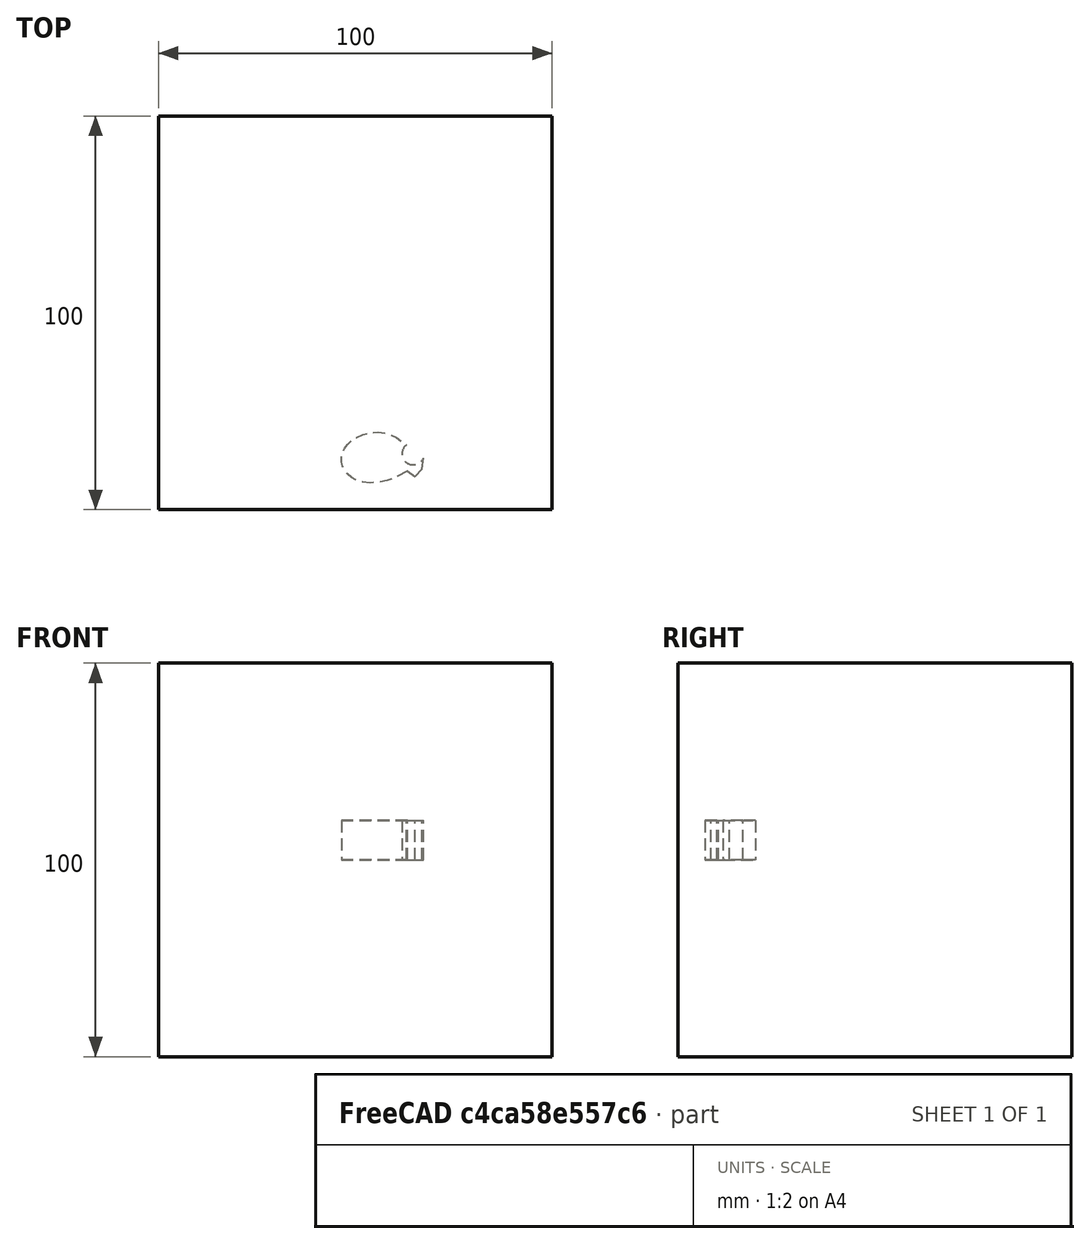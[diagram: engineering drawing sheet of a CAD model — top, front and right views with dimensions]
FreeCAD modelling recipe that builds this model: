
FCSTD DOCUMENT  (FreeCAD 0.19RUnknown)
Label: mirrorTest-3b
License: All rights reserved
LicenseURL: http://en.wikipedia.org/wiki/All_rights_reserved
objects: App::DocumentObjectGroupPython×1248, Part::Mirroring×2, App::Part×2, Part::FeaturePython×1, Sketcher::SketchObject×1, Part::Extrusion×1
note: 5 computed .brp shape members not serialized (recipe doc carries the construction recipe); baked Part::Feature solids carry a one-line shape summary decoded from their .brp

FEATURE [App::DocumentObjectGroupPython] HALFPI  # scripted group (container) (typed FeaturePython)
  name = HALFPI
  value = pi/2.
FEATURE [App::DocumentObjectGroupPython] PI  # scripted group (container) (typed FeaturePython)
  name = PI
  value = 1.*pi
FEATURE [App::DocumentObjectGroupPython] TWOPI  # scripted group (container) (typed FeaturePython)
  name = TWOPI
  value = 2.*pi
FEATURE [App::DocumentObjectGroupPython] Constants  # scripted group (container) (typed FeaturePython)
  Group = -> [HALFPI,PI,TWOPI]
FEATURE [App::DocumentObjectGroupPython] Variables  # scripted group (container) (typed FeaturePython)
FEATURE [App::DocumentObjectGroupPython] Quantities  # scripted group (container) (typed FeaturePython)
FEATURE [App::DocumentObjectGroupPython] Isotopes  # scripted group (container) (typed FeaturePython)
FEATURE [App::DocumentObjectGroupPython] Elements  # scripted group (container) (typed FeaturePython)
FEATURE [App::DocumentObjectGroupPython] G4Isotopes  # scripted group (container) (typed FeaturePython)
FEATURE [App::DocumentObjectGroupPython] H_element  # scripted group (container) (typed FeaturePython)
  Z = 1
  atom_value = 1.008
  formula = H
  name = H_element
FEATURE [App::DocumentObjectGroupPython] He_element  # scripted group (container) (typed FeaturePython)
  Z = 2
  atom_value = 4.0026
  formula = He
  name = He_element
FEATURE [App::DocumentObjectGroupPython] Li_element  # scripted group (container) (typed FeaturePython)
  Z = 3
  atom_value = 6.94
  formula = Li
  name = Li_element
FEATURE [App::DocumentObjectGroupPython] Be_element  # scripted group (container) (typed FeaturePython)
  Z = 4
  atom_value = 9.01218
  formula = Be
  name = Be_element
FEATURE [App::DocumentObjectGroupPython] B_element  # scripted group (container) (typed FeaturePython)
  Z = 5
  atom_value = 10.81
  formula = B
  name = B_element
FEATURE [App::DocumentObjectGroupPython] C_element  # scripted group (container) (typed FeaturePython)
  Z = 6
  atom_value = 12.011
  formula = C
  name = C_element
FEATURE [App::DocumentObjectGroupPython] N_element  # scripted group (container) (typed FeaturePython)
  Z = 7
  atom_value = 14.007
  formula = N
  name = N_element
FEATURE [App::DocumentObjectGroupPython] O_element  # scripted group (container) (typed FeaturePython)
  Z = 8
  atom_value = 15.999
  formula = O
  name = O_element
FEATURE [App::DocumentObjectGroupPython] F_element  # scripted group (container) (typed FeaturePython)
  Z = 9
  atom_value = 18.9984
  formula = F
  name = F_element
FEATURE [App::DocumentObjectGroupPython] Ne_element  # scripted group (container) (typed FeaturePython)
  Z = 10
  atom_value = 20.1797
  formula = Ne
  name = Ne_element
FEATURE [App::DocumentObjectGroupPython] Na_element  # scripted group (container) (typed FeaturePython)
  Z = 11
  atom_value = 22.9898
  formula = Na
  name = Na_element
FEATURE [App::DocumentObjectGroupPython] Mg_element  # scripted group (container) (typed FeaturePython)
  Z = 12
  atom_value = 24.305
  formula = Mg
  name = Mg_element
FEATURE [App::DocumentObjectGroupPython] Al_element  # scripted group (container) (typed FeaturePython)
  Z = 13
  atom_value = 26.9815
  formula = Al
  name = Al_element
FEATURE [App::DocumentObjectGroupPython] Si_element  # scripted group (container) (typed FeaturePython)
  Z = 14
  atom_value = 28.085
  formula = Si
  name = Si_element
FEATURE [App::DocumentObjectGroupPython] P_element  # scripted group (container) (typed FeaturePython)
  Z = 15
  atom_value = 30.9738
  formula = P
  name = P_element
FEATURE [App::DocumentObjectGroupPython] S_element  # scripted group (container) (typed FeaturePython)
  Z = 16
  atom_value = 32.06
  formula = S
  name = S_element
FEATURE [App::DocumentObjectGroupPython] Cl_element  # scripted group (container) (typed FeaturePython)
  Z = 17
  atom_value = 35.45
  formula = Cl
  name = Cl_element
FEATURE [App::DocumentObjectGroupPython] Ar_element  # scripted group (container) (typed FeaturePython)
  Z = 18
  atom_value = 39.95
  formula = Ar
  name = Ar_element
FEATURE [App::DocumentObjectGroupPython] K_element  # scripted group (container) (typed FeaturePython)
  Z = 19
  atom_value = 39.0983
  formula = K
  name = K_element
FEATURE [App::DocumentObjectGroupPython] Ca_element  # scripted group (container) (typed FeaturePython)
  Z = 20
  atom_value = 40.078
  formula = Ca
  name = Ca_element
FEATURE [App::DocumentObjectGroupPython] Sc_element  # scripted group (container) (typed FeaturePython)
  Z = 21
  atom_value = 44.9559
  formula = Sc
  name = Sc_element
FEATURE [App::DocumentObjectGroupPython] Ti_element  # scripted group (container) (typed FeaturePython)
  Z = 22
  atom_value = 47.867
  formula = Ti
  name = Ti_element
FEATURE [App::DocumentObjectGroupPython] V_element  # scripted group (container) (typed FeaturePython)
  Z = 23
  atom_value = 50.9415
  formula = V
  name = V_element
FEATURE [App::DocumentObjectGroupPython] Cr_element  # scripted group (container) (typed FeaturePython)
  Z = 24
  atom_value = 51.9961
  formula = Cr
  name = Cr_element
FEATURE [App::DocumentObjectGroupPython] Mn_element  # scripted group (container) (typed FeaturePython)
  Z = 25
  atom_value = 54.938
  formula = Mn
  name = Mn_element
FEATURE [App::DocumentObjectGroupPython] Fe_element  # scripted group (container) (typed FeaturePython)
  Z = 26
  atom_value = 55.845
  formula = Fe
  name = Fe_element
FEATURE [App::DocumentObjectGroupPython] Co_element  # scripted group (container) (typed FeaturePython)
  Z = 27
  atom_value = 58.9332
  formula = Co
  name = Co_element
FEATURE [App::DocumentObjectGroupPython] Ni_element  # scripted group (container) (typed FeaturePython)
  Z = 28
  atom_value = 58.6934
  formula = Ni
  name = Ni_element
FEATURE [App::DocumentObjectGroupPython] Cu_element  # scripted group (container) (typed FeaturePython)
  Z = 29
  atom_value = 63.546
  formula = Cu
  name = Cu_element
FEATURE [App::DocumentObjectGroupPython] Zn_element  # scripted group (container) (typed FeaturePython)
  Z = 30
  atom_value = 65.38
  formula = Zn
  name = Zn_element
FEATURE [App::DocumentObjectGroupPython] Ga_element  # scripted group (container) (typed FeaturePython)
  Z = 31
  atom_value = 69.723
  formula = Ga
  name = Ga_element
FEATURE [App::DocumentObjectGroupPython] Ge_element  # scripted group (container) (typed FeaturePython)
  Z = 32
  atom_value = 72.63
  formula = Ge
  name = Ge_element
FEATURE [App::DocumentObjectGroupPython] As_element  # scripted group (container) (typed FeaturePython)
  Z = 33
  atom_value = 74.9216
  formula = As
  name = As_element
FEATURE [App::DocumentObjectGroupPython] Se_element  # scripted group (container) (typed FeaturePython)
  Z = 34
  atom_value = 78.971
  formula = Se
  name = Se_element
FEATURE [App::DocumentObjectGroupPython] Br_element  # scripted group (container) (typed FeaturePython)
  Z = 35
  atom_value = 79.904
  formula = Br
  name = Br_element
FEATURE [App::DocumentObjectGroupPython] Kr_element  # scripted group (container) (typed FeaturePython)
  Z = 36
  atom_value = 83.798
  formula = Kr
  name = Kr_element
FEATURE [App::DocumentObjectGroupPython] Rb_element  # scripted group (container) (typed FeaturePython)
  Z = 37
  atom_value = 85.4678
  formula = Rb
  name = Rb_element
FEATURE [App::DocumentObjectGroupPython] Sr_element  # scripted group (container) (typed FeaturePython)
  Z = 38
  atom_value = 87.62
  formula = Sr
  name = Sr_element
FEATURE [App::DocumentObjectGroupPython] Y_element  # scripted group (container) (typed FeaturePython)
  Z = 39
  atom_value = 88.9058
  formula = Y
  name = Y_element
FEATURE [App::DocumentObjectGroupPython] Zr_element  # scripted group (container) (typed FeaturePython)
  Z = 40
  atom_value = 91.224
  formula = Zr
  name = Zr_element
FEATURE [App::DocumentObjectGroupPython] Nb_element  # scripted group (container) (typed FeaturePython)
  Z = 41
  atom_value = 92.9064
  formula = Nb
  name = Nb_element
FEATURE [App::DocumentObjectGroupPython] Mo_element  # scripted group (container) (typed FeaturePython)
  Z = 42
  atom_value = 95.95
  formula = Mo
  name = Mo_element
FEATURE [App::DocumentObjectGroupPython] Tc_element  # scripted group (container) (typed FeaturePython)
  Z = 43
  atom_value = 97
  formula = Tc
  name = Tc_element
FEATURE [App::DocumentObjectGroupPython] Ru_element  # scripted group (container) (typed FeaturePython)
  Z = 44
  atom_value = 101.07
  formula = Ru
  name = Ru_element
FEATURE [App::DocumentObjectGroupPython] Rh_element  # scripted group (container) (typed FeaturePython)
  Z = 45
  atom_value = 102.905
  formula = Rh
  name = Rh_element
FEATURE [App::DocumentObjectGroupPython] Pd_element  # scripted group (container) (typed FeaturePython)
  Z = 46
  atom_value = 106.42
  formula = Pd
  name = Pd_element
FEATURE [App::DocumentObjectGroupPython] Ag_element  # scripted group (container) (typed FeaturePython)
  Z = 47
  atom_value = 107.868
  formula = Ag
  name = Ag_element
FEATURE [App::DocumentObjectGroupPython] Cd_element  # scripted group (container) (typed FeaturePython)
  Z = 48
  atom_value = 112.414
  formula = Cd
  name = Cd_element
FEATURE [App::DocumentObjectGroupPython] In_element  # scripted group (container) (typed FeaturePython)
  Z = 49
  atom_value = 114.818
  formula = In
  name = In_element
FEATURE [App::DocumentObjectGroupPython] Sn_element  # scripted group (container) (typed FeaturePython)
  Z = 50
  atom_value = 118.71
  formula = Sn
  name = Sn_element
FEATURE [App::DocumentObjectGroupPython] Sb_element  # scripted group (container) (typed FeaturePython)
  Z = 51
  atom_value = 121.76
  formula = Sb
  name = Sb_element
FEATURE [App::DocumentObjectGroupPython] Te_element  # scripted group (container) (typed FeaturePython)
  Z = 52
  atom_value = 127.6
  formula = Te
  name = Te_element
FEATURE [App::DocumentObjectGroupPython] I_element  # scripted group (container) (typed FeaturePython)
  Z = 53
  atom_value = 126.904
  formula = I
  name = I_element
FEATURE [App::DocumentObjectGroupPython] Xe_element  # scripted group (container) (typed FeaturePython)
  Z = 54
  atom_value = 131.293
  formula = Xe
  name = Xe_element
FEATURE [App::DocumentObjectGroupPython] Cs_element  # scripted group (container) (typed FeaturePython)
  Z = 55
  atom_value = 132.905
  formula = Cs
  name = Cs_element
FEATURE [App::DocumentObjectGroupPython] Ba_element  # scripted group (container) (typed FeaturePython)
  Z = 56
  atom_value = 137.327
  formula = Ba
  name = Ba_element
FEATURE [App::DocumentObjectGroupPython] La_element  # scripted group (container) (typed FeaturePython)
  Z = 57
  atom_value = 138.905
  formula = La
  name = La_element
FEATURE [App::DocumentObjectGroupPython] Ce_element  # scripted group (container) (typed FeaturePython)
  Z = 58
  atom_value = 140.116
  formula = Ce
  name = Ce_element
FEATURE [App::DocumentObjectGroupPython] Pr_element  # scripted group (container) (typed FeaturePython)
  Z = 59
  atom_value = 140.908
  formula = Pr
  name = Pr_element
FEATURE [App::DocumentObjectGroupPython] Nd_element  # scripted group (container) (typed FeaturePython)
  Z = 60
  atom_value = 144.242
  formula = Nd
  name = Nd_element
FEATURE [App::DocumentObjectGroupPython] Pm_element  # scripted group (container) (typed FeaturePython)
  Z = 61
  atom_value = 145
  formula = Pm
  name = Pm_element
FEATURE [App::DocumentObjectGroupPython] Sm_element  # scripted group (container) (typed FeaturePython)
  Z = 62
  atom_value = 150.36
  formula = Sm
  name = Sm_element
FEATURE [App::DocumentObjectGroupPython] Eu_element  # scripted group (container) (typed FeaturePython)
  Z = 63
  atom_value = 151.964
  formula = Eu
  name = Eu_element
FEATURE [App::DocumentObjectGroupPython] Gd_element  # scripted group (container) (typed FeaturePython)
  Z = 64
  atom_value = 157.25
  formula = Gd
  name = Gd_element
FEATURE [App::DocumentObjectGroupPython] Tb_element  # scripted group (container) (typed FeaturePython)
  Z = 65
  atom_value = 158.925
  formula = Tb
  name = Tb_element
FEATURE [App::DocumentObjectGroupPython] Dy_element  # scripted group (container) (typed FeaturePython)
  Z = 66
  atom_value = 162.5
  formula = Dy
  name = Dy_element
FEATURE [App::DocumentObjectGroupPython] Ho_element  # scripted group (container) (typed FeaturePython)
  Z = 67
  atom_value = 164.93
  formula = Ho
  name = Ho_element
FEATURE [App::DocumentObjectGroupPython] Er_element  # scripted group (container) (typed FeaturePython)
  Z = 68
  atom_value = 167.259
  formula = Er
  name = Er_element
FEATURE [App::DocumentObjectGroupPython] Tm_element  # scripted group (container) (typed FeaturePython)
  Z = 69
  atom_value = 168.934
  formula = Tm
  name = Tm_element
FEATURE [App::DocumentObjectGroupPython] Yb_element  # scripted group (container) (typed FeaturePython)
  Z = 70
  atom_value = 173.045
  formula = Yb
  name = Yb_element
FEATURE [App::DocumentObjectGroupPython] Lu_element  # scripted group (container) (typed FeaturePython)
  Z = 71
  atom_value = 174.967
  formula = Lu
  name = Lu_element
FEATURE [App::DocumentObjectGroupPython] Hf_element  # scripted group (container) (typed FeaturePython)
  Z = 72
  atom_value = 178.49
  formula = Hf
  name = Hf_element
FEATURE [App::DocumentObjectGroupPython] Ta_element  # scripted group (container) (typed FeaturePython)
  Z = 73
  atom_value = 180.948
  formula = Ta
  name = Ta_element
FEATURE [App::DocumentObjectGroupPython] W_element  # scripted group (container) (typed FeaturePython)
  Z = 74
  atom_value = 183.84
  formula = W
  name = W_element
FEATURE [App::DocumentObjectGroupPython] Re_element  # scripted group (container) (typed FeaturePython)
  Z = 75
  atom_value = 186.207
  formula = Re
  name = Re_element
FEATURE [App::DocumentObjectGroupPython] Os_element  # scripted group (container) (typed FeaturePython)
  Z = 76
  atom_value = 190.23
  formula = Os
  name = Os_element
FEATURE [App::DocumentObjectGroupPython] Ir_element  # scripted group (container) (typed FeaturePython)
  Z = 77
  atom_value = 192.217
  formula = Ir
  name = Ir_element
FEATURE [App::DocumentObjectGroupPython] Pt_element  # scripted group (container) (typed FeaturePython)
  Z = 78
  atom_value = 195.084
  formula = Pt
  name = Pt_element
FEATURE [App::DocumentObjectGroupPython] Au_element  # scripted group (container) (typed FeaturePython)
  Z = 79
  atom_value = 196.967
  formula = Au
  name = Au_element
FEATURE [App::DocumentObjectGroupPython] Hg_element  # scripted group (container) (typed FeaturePython)
  Z = 80
  atom_value = 200.592
  formula = Hg
  name = Hg_element
FEATURE [App::DocumentObjectGroupPython] Tl_element  # scripted group (container) (typed FeaturePython)
  Z = 81
  atom_value = 204.38
  formula = Tl
  name = Tl_element
FEATURE [App::DocumentObjectGroupPython] Pb_element  # scripted group (container) (typed FeaturePython)
  Z = 82
  atom_value = 207.2
  formula = Pb
  name = Pb_element
FEATURE [App::DocumentObjectGroupPython] Bi_element  # scripted group (container) (typed FeaturePython)
  Z = 83
  atom_value = 208.98
  formula = Bi
  name = Bi_element
FEATURE [App::DocumentObjectGroupPython] Po_element  # scripted group (container) (typed FeaturePython)
  Z = 84
  atom_value = 209
  formula = Po
  name = Po_element
FEATURE [App::DocumentObjectGroupPython] At_element  # scripted group (container) (typed FeaturePython)
  Z = 85
  atom_value = 210
  formula = At
  name = At_element
FEATURE [App::DocumentObjectGroupPython] Rn_element  # scripted group (container) (typed FeaturePython)
  Z = 86
  atom_value = 222
  formula = Rn
  name = Rn_element
FEATURE [App::DocumentObjectGroupPython] Fr_element  # scripted group (container) (typed FeaturePython)
  Z = 87
  atom_value = 223
  formula = Fr
  name = Fr_element
FEATURE [App::DocumentObjectGroupPython] Ra_element  # scripted group (container) (typed FeaturePython)
  Z = 88
  atom_value = 226
  formula = Ra
  name = Ra_element
FEATURE [App::DocumentObjectGroupPython] Ac_element  # scripted group (container) (typed FeaturePython)
  Z = 89
  atom_value = 227
  formula = Ac
  name = Ac_element
FEATURE [App::DocumentObjectGroupPython] Th_element  # scripted group (container) (typed FeaturePython)
  Z = 90
  atom_value = 232.038
  formula = Th
  name = Th_element
FEATURE [App::DocumentObjectGroupPython] Pa_element  # scripted group (container) (typed FeaturePython)
  Z = 91
  atom_value = 231.036
  formula = Pa
  name = Pa_element
FEATURE [App::DocumentObjectGroupPython] U_element  # scripted group (container) (typed FeaturePython)
  Z = 92
  atom_value = 238.029
  formula = U
  name = U_element
FEATURE [App::DocumentObjectGroupPython] Np_element  # scripted group (container) (typed FeaturePython)
  Z = 93
  atom_value = 237
  formula = Np
  name = Np_element
FEATURE [App::DocumentObjectGroupPython] Pu_element  # scripted group (container) (typed FeaturePython)
  Z = 94
  atom_value = 244
  formula = Pu
  name = Pu_element
FEATURE [App::DocumentObjectGroupPython] Am_element  # scripted group (container) (typed FeaturePython)
  Z = 95
  atom_value = 243
  formula = Am
  name = Am_element
FEATURE [App::DocumentObjectGroupPython] Cm_element  # scripted group (container) (typed FeaturePython)
  Z = 96
  atom_value = 247
  formula = Cm
  name = Cm_element
FEATURE [App::DocumentObjectGroupPython] Bk_element  # scripted group (container) (typed FeaturePython)
  Z = 97
  atom_value = 247
  formula = Bk
  name = Bk_element
FEATURE [App::DocumentObjectGroupPython] Cf_element  # scripted group (container) (typed FeaturePython)
  Z = 98
  atom_value = 251
  formula = Cf
  name = Cf_element
FEATURE [App::DocumentObjectGroupPython] G4Elements  # scripted group (container) (typed FeaturePython)
  Group = -> [H_element,He_element,Li_element,Be_element,B_element,C_element,N_element,O_element,F_element,Ne_element,Na_element,Mg_element,Al_element,Si_element,P_element,S_element,Cl_element,Ar_element,K_element,Ca_element,Sc_element,Ti_element,V_element,Cr_element,Mn_element,Fe_element,Co_element,Ni_element,Cu_element,Zn_element,Ga_element,Ge_element,As_element,Se_element,Br_element,Kr_element,Rb_element,+61 more]
FEATURE [App::DocumentObjectGroupPython] H_element001  label="H_element : 0.101"  # scripted group (container) (typed FeaturePython)
  n = 0.101327
FEATURE [App::DocumentObjectGroupPython] C_element001  label="C_element : 0.775"  # scripted group (container) (typed FeaturePython)
  n = 0.7755
FEATURE [App::DocumentObjectGroupPython] N_element001  label="N_element : 0.035"  # scripted group (container) (typed FeaturePython)
  n = 0.035057
FEATURE [App::DocumentObjectGroupPython] O_element001  label="O_element : 0.052"  # scripted group (container) (typed FeaturePython)
  n = 0.0523159
FEATURE [App::DocumentObjectGroupPython] F_element001  label="F_element : 0.017"  # scripted group (container) (typed FeaturePython)
  n = 0.017422
FEATURE [App::DocumentObjectGroupPython] Ca_element001  label="Ca_element : 0.018"  # scripted group (container) (typed FeaturePython)
  n = 0.018378
FEATURE [App::DocumentObjectGroupPython] G4_A_150_TISSUE  label="G4_A-150_TISSUE"  # scripted group (container) (typed FeaturePython)
  Dunit = g/cm3
  Dvalue = 1.127
  Group = -> [H_element001,C_element001,N_element001,O_element001,F_element001,Ca_element001]
  conduct = 2
  density = 1
  expand = 3
  formula = G4_A-150_TISSUE
  name = G4_A-150_TISSUE
  specific = 4
FEATURE [App::DocumentObjectGroupPython] C_element002  label="C_element : 3"  # scripted group (container) (typed FeaturePython)
  n = 3
  ref = C_element
FEATURE [App::DocumentObjectGroupPython] H_element002  label="H_element : 6"  # scripted group (container) (typed FeaturePython)
  n = 6
  ref = H_element
FEATURE [App::DocumentObjectGroupPython] O_element002  label="O_element : 1"  # scripted group (container) (typed FeaturePython)
  n = 1
  ref = O_element
FEATURE [App::DocumentObjectGroupPython] G4_ACETONE  # scripted group (container) (typed FeaturePython)
  Dunit = g/cm3
  Dvalue = 0.7899
  Group = -> [C_element002,H_element002,O_element002]
  conduct = 2
  density = 1
  expand = 3
  formula = G4_ACETONE
  name = G4_ACETONE
  specific = 4
FEATURE [App::DocumentObjectGroupPython] C_element003  label="C_element : 2"  # scripted group (container) (typed FeaturePython)
  n = 2
  ref = C_element
FEATURE [App::DocumentObjectGroupPython] H_element003  label="H_element : 2"  # scripted group (container) (typed FeaturePython)
  n = 2
  ref = H_element
FEATURE [App::DocumentObjectGroupPython] G4_ACETYLENE  # scripted group (container) (typed FeaturePython)
  Dunit = g/cm3
  Dvalue = 0.0010967
  Group = -> [C_element003,H_element003]
  conduct = 2
  density = 1
  expand = 3
  formula = G4_ACETYLENE
  name = G4_ACETYLENE
  specific = 4
FEATURE [App::DocumentObjectGroupPython] C_element004  label="C_element : 5"  # scripted group (container) (typed FeaturePython)
  n = 5
  ref = C_element
FEATURE [App::DocumentObjectGroupPython] H_element004  label="H_element : 5"  # scripted group (container) (typed FeaturePython)
  n = 5
  ref = H_element
FEATURE [App::DocumentObjectGroupPython] N_element002  label="N_element : 5"  # scripted group (container) (typed FeaturePython)
  n = 5
  ref = N_element
FEATURE [App::DocumentObjectGroupPython] G4_ADENINE  # scripted group (container) (typed FeaturePython)
  Dunit = g/cm3
  Dvalue = 1.6
  Group = -> [C_element004,H_element004,N_element002]
  conduct = 2
  density = 1
  expand = 3
  formula = G4_ADENINE
  name = G4_ADENINE
  specific = 4
FEATURE [App::DocumentObjectGroupPython] H_element005  label="H_element : 0.114"  # scripted group (container) (typed FeaturePython)
  n = 0.114
FEATURE [App::DocumentObjectGroupPython] C_element005  label="C_element : 0.598"  # scripted group (container) (typed FeaturePython)
  n = 0.598
FEATURE [App::DocumentObjectGroupPython] N_element003  label="N_element : 0.007"  # scripted group (container) (typed FeaturePython)
  n = 0.007
FEATURE [App::DocumentObjectGroupPython] O_element003  label="O_element : 0.278"  # scripted group (container) (typed FeaturePython)
  n = 0.278
FEATURE [App::DocumentObjectGroupPython] Na_element001  label="Na_element : 0.001"  # scripted group (container) (typed FeaturePython)
  n = 0.001
FEATURE [App::DocumentObjectGroupPython] S_element001  label="S_element : 0.001"  # scripted group (container) (typed FeaturePython)
  n = 0.001
FEATURE [App::DocumentObjectGroupPython] Cl_element001  label="Cl_element : 0.001"  # scripted group (container) (typed FeaturePython)
  n = 0.001
FEATURE [App::DocumentObjectGroupPython] G4_ADIPOSE_TISSUE_ICRP  # scripted group (container) (typed FeaturePython)
  Dunit = g/cm3
  Dvalue = 0.95
  Group = -> [H_element005,C_element005,N_element003,O_element003,Na_element001,S_element001,Cl_element001]
  conduct = 2
  density = 1
  expand = 3
  formula = G4_ADIPOSE_TISSUE_ICRP
  name = G4_ADIPOSE_TISSUE_ICRP
  specific = 4
FEATURE [App::DocumentObjectGroupPython] C_element006  label="C_element : 0.000"  # scripted group (container) (typed FeaturePython)
  n = 0.000124
FEATURE [App::DocumentObjectGroupPython] N_element004  label="N_element : 0.755"  # scripted group (container) (typed FeaturePython)
  n = 0.755268
FEATURE [App::DocumentObjectGroupPython] O_element004  label="O_element : 0.232"  # scripted group (container) (typed FeaturePython)
  n = 0.231781
FEATURE [App::DocumentObjectGroupPython] Ar_element001  label="Ar_element : 0.013"  # scripted group (container) (typed FeaturePython)
  n = 0.012827
FEATURE [App::DocumentObjectGroupPython] G4_AIR  # scripted group (container) (typed FeaturePython)
  Dunit = g/cm3
  Dvalue = 0.00120479
  Group = -> [C_element006,N_element004,O_element004,Ar_element001]
  conduct = 2
  density = 1
  expand = 3
  formula = G4_AIR
  name = G4_AIR
  specific = 4
FEATURE [App::DocumentObjectGroupPython] C_element007  label="C_element : 006"  # scripted group (container) (typed FeaturePython)
  n = 3
  ref = C_element
FEATURE [App::DocumentObjectGroupPython] H_element006  label="H_element : 7"  # scripted group (container) (typed FeaturePython)
  n = 7
  ref = H_element
FEATURE [App::DocumentObjectGroupPython] N_element005  label="N_element : 1"  # scripted group (container) (typed FeaturePython)
  n = 1
  ref = N_element
FEATURE [App::DocumentObjectGroupPython] O_element005  label="O_element : 2"  # scripted group (container) (typed FeaturePython)
  n = 2
  ref = O_element
FEATURE [App::DocumentObjectGroupPython] G4_ALANINE  # scripted group (container) (typed FeaturePython)
  Dunit = g/cm3
  Dvalue = 1.42
  Group = -> [C_element007,H_element006,N_element005,O_element005]
  conduct = 2
  density = 1
  expand = 3
  formula = G4_ALANINE
  name = G4_ALANINE
  specific = 4
FEATURE [App::DocumentObjectGroupPython] Al_element001  label="Al_element : 2"  # scripted group (container) (typed FeaturePython)
  n = 2
  ref = Al_element
FEATURE [App::DocumentObjectGroupPython] O_element006  label="O_element : 3"  # scripted group (container) (typed FeaturePython)
  n = 3
  ref = O_element
FEATURE [App::DocumentObjectGroupPython] G4_ALUMINUM_OXIDE  # scripted group (container) (typed FeaturePython)
  Dunit = g/cm3
  Dvalue = 3.97
  Group = -> [Al_element001,O_element006]
  conduct = 2
  density = 1
  expand = 3
  formula = G4_ALUMINUM_OXIDE
  name = G4_ALUMINUM_OXIDE
  specific = 4
FEATURE [App::DocumentObjectGroupPython] H_element007  label="H_element : 0.106"  # scripted group (container) (typed FeaturePython)
  n = 0.10593
FEATURE [App::DocumentObjectGroupPython] C_element008  label="C_element : 0.789"  # scripted group (container) (typed FeaturePython)
  n = 0.788974
FEATURE [App::DocumentObjectGroupPython] O_element007  label="O_element : 0.105"  # scripted group (container) (typed FeaturePython)
  n = 0.105096
FEATURE [App::DocumentObjectGroupPython] G4_AMBER  # scripted group (container) (typed FeaturePython)
  Dunit = g/cm3
  Dvalue = 1.1
  Group = -> [H_element007,C_element008,O_element007]
  conduct = 2
  density = 1
  expand = 3
  formula = G4_AMBER
  name = G4_AMBER
  specific = 4
FEATURE [App::DocumentObjectGroupPython] N_element006  label="N_element : 006"  # scripted group (container) (typed FeaturePython)
  n = 1
  ref = N_element
FEATURE [App::DocumentObjectGroupPython] H_element008  label="H_element : 3"  # scripted group (container) (typed FeaturePython)
  n = 3
  ref = H_element
FEATURE [App::DocumentObjectGroupPython] G4_AMMONIA  # scripted group (container) (typed FeaturePython)
  Dunit = g/cm3
  Dvalue = 0.000826019
  Group = -> [N_element006,H_element008]
  conduct = 2
  density = 1
  expand = 3
  formula = G4_AMMONIA
  name = G4_AMMONIA
  specific = 4
FEATURE [App::DocumentObjectGroupPython] C_element009  label="C_element : 6"  # scripted group (container) (typed FeaturePython)
  n = 6
  ref = C_element
FEATURE [App::DocumentObjectGroupPython] H_element009  label="H_element : 008"  # scripted group (container) (typed FeaturePython)
  n = 7
  ref = H_element
FEATURE [App::DocumentObjectGroupPython] N_element007  label="N_element : 007"  # scripted group (container) (typed FeaturePython)
  n = 1
  ref = N_element
FEATURE [App::DocumentObjectGroupPython] G4_ANILINE  # scripted group (container) (typed FeaturePython)
  Dunit = g/cm3
  Dvalue = 1.0235
  Group = -> [C_element009,H_element009,N_element007]
  conduct = 2
  density = 1
  expand = 3
  formula = G4_ANILINE
  name = G4_ANILINE
  specific = 4
FEATURE [App::DocumentObjectGroupPython] C_element010  label="C_element : 14"  # scripted group (container) (typed FeaturePython)
  n = 14
  ref = C_element
FEATURE [App::DocumentObjectGroupPython] H_element010  label="H_element : 10"  # scripted group (container) (typed FeaturePython)
  n = 10
  ref = H_element
FEATURE [App::DocumentObjectGroupPython] G4_ANTHRACENE  # scripted group (container) (typed FeaturePython)
  Dunit = g/cm3
  Dvalue = 1.283
  Group = -> [C_element010,H_element010]
  conduct = 2
  density = 1
  expand = 3
  formula = G4_ANTHRACENE
  name = G4_ANTHRACENE
  specific = 4
FEATURE [App::DocumentObjectGroupPython] H_element011  label="H_element : 0.065"  # scripted group (container) (typed FeaturePython)
  n = 0.0654709
FEATURE [App::DocumentObjectGroupPython] C_element011  label="C_element : 0.537"  # scripted group (container) (typed FeaturePython)
  n = 0.536944
FEATURE [App::DocumentObjectGroupPython] N_element008  label="N_element : 0.021"  # scripted group (container) (typed FeaturePython)
  n = 0.0215
FEATURE [App::DocumentObjectGroupPython] O_element008  label="O_element : 0.032"  # scripted group (container) (typed FeaturePython)
  n = 0.032085
FEATURE [App::DocumentObjectGroupPython] F_element002  label="F_element : 0.167"  # scripted group (container) (typed FeaturePython)
  n = 0.167411
FEATURE [App::DocumentObjectGroupPython] Ca_element002  label="Ca_element : 0.177"  # scripted group (container) (typed FeaturePython)
  n = 0.176589
FEATURE [App::DocumentObjectGroupPython] G4_B_100_BONE  label="G4_B-100_BONE"  # scripted group (container) (typed FeaturePython)
  Dunit = g/cm3
  Dvalue = 1.45
  Group = -> [H_element011,C_element011,N_element008,O_element008,F_element002,Ca_element002]
  conduct = 2
  density = 1
  expand = 3
  formula = G4_B-100_BONE
  name = G4_B-100_BONE
  specific = 4
FEATURE [App::DocumentObjectGroupPython] H_element012  label="H_element : 0.057"  # scripted group (container) (typed FeaturePython)
  n = 0.057441
FEATURE [App::DocumentObjectGroupPython] C_element012  label="C_element : 0.790"  # scripted group (container) (typed FeaturePython)
  n = 0.774591
FEATURE [App::DocumentObjectGroupPython] O_element009  label="O_element : 0.168"  # scripted group (container) (typed FeaturePython)
  n = 0.167968
FEATURE [App::DocumentObjectGroupPython] G4_BAKELITE  # scripted group (container) (typed FeaturePython)
  Dunit = g/cm3
  Dvalue = 1.25
  Group = -> [H_element012,C_element012,O_element009]
  conduct = 2
  density = 1
  expand = 3
  formula = G4_BAKELITE
  name = G4_BAKELITE
  specific = 4
FEATURE [App::DocumentObjectGroupPython] Ba_element001  label="Ba_element : 1"  # scripted group (container) (typed FeaturePython)
  n = 1
  ref = Ba_element
FEATURE [App::DocumentObjectGroupPython] F_element003  label="F_element : 2"  # scripted group (container) (typed FeaturePython)
  n = 2
  ref = F_element
FEATURE [App::DocumentObjectGroupPython] G4_BARIUM_FLUORIDE  # scripted group (container) (typed FeaturePython)
  Dunit = g/cm3
  Dvalue = 4.89
  Group = -> [Ba_element001,F_element003]
  conduct = 2
  density = 1
  expand = 3
  formula = G4_BARIUM_FLUORIDE
  name = G4_BARIUM_FLUORIDE
  specific = 4
FEATURE [App::DocumentObjectGroupPython] Ba_element002  label="Ba_element : 002"  # scripted group (container) (typed FeaturePython)
  n = 1
  ref = Ba_element
FEATURE [App::DocumentObjectGroupPython] S_element002  label="S_element : 1"  # scripted group (container) (typed FeaturePython)
  n = 1
  ref = S_element
FEATURE [App::DocumentObjectGroupPython] O_element010  label="O_element : 4"  # scripted group (container) (typed FeaturePython)
  n = 4
  ref = O_element
FEATURE [App::DocumentObjectGroupPython] G4_BARIUM_SULFATE  # scripted group (container) (typed FeaturePython)
  Dunit = g/cm3
  Dvalue = 4.5
  Group = -> [Ba_element002,S_element002,O_element010]
  conduct = 2
  density = 1
  expand = 3
  formula = G4_BARIUM_SULFATE
  name = G4_BARIUM_SULFATE
  specific = 4
FEATURE [App::DocumentObjectGroupPython] C_element013  label="C_element : 007"  # scripted group (container) (typed FeaturePython)
  n = 6
  ref = C_element
FEATURE [App::DocumentObjectGroupPython] H_element013  label="H_element : 009"  # scripted group (container) (typed FeaturePython)
  n = 6
  ref = H_element
FEATURE [App::DocumentObjectGroupPython] G4_BENZENE  # scripted group (container) (typed FeaturePython)
  Dunit = g/cm3
  Dvalue = 0.87865
  Group = -> [C_element013,H_element013]
  conduct = 2
  density = 1
  expand = 3
  formula = G4_BENZENE
  name = G4_BENZENE
  specific = 4
FEATURE [App::DocumentObjectGroupPython] Be_element001  label="Be_element : 1"  # scripted group (container) (typed FeaturePython)
  n = 1
  ref = Be_element
FEATURE [App::DocumentObjectGroupPython] O_element011  label="O_element : 005"  # scripted group (container) (typed FeaturePython)
  n = 1
  ref = O_element
FEATURE [App::DocumentObjectGroupPython] G4_BERYLLIUM_OXIDE  # scripted group (container) (typed FeaturePython)
  Dunit = g/cm3
  Dvalue = 3.01
  Group = -> [Be_element001,O_element011]
  conduct = 2
  density = 1
  expand = 3
  formula = G4_BERYLLIUM_OXIDE
  name = G4_BERYLLIUM_OXIDE
  specific = 4
FEATURE [App::DocumentObjectGroupPython] Bi_element001  label="Bi_element : 4"  # scripted group (container) (typed FeaturePython)
  n = 4
  ref = Bi_element
FEATURE [App::DocumentObjectGroupPython] Ge_element001  label="Ge_element : 3"  # scripted group (container) (typed FeaturePython)
  n = 3
  ref = Ge_element
FEATURE [App::DocumentObjectGroupPython] O_element012  label="O_element : 12"  # scripted group (container) (typed FeaturePython)
  n = 12
  ref = O_element
FEATURE [App::DocumentObjectGroupPython] G4_BGO  # scripted group (container) (typed FeaturePython)
  Dunit = g/cm3
  Dvalue = 7.13
  Group = -> [Bi_element001,Ge_element001,O_element012]
  conduct = 2
  density = 1
  expand = 3
  formula = G4_BGO
  name = G4_BGO
  specific = 4
FEATURE [App::DocumentObjectGroupPython] H_element014  label="H_element : 0.102"  # scripted group (container) (typed FeaturePython)
  n = 0.102
FEATURE [App::DocumentObjectGroupPython] C_element014  label="C_element : 0.110"  # scripted group (container) (typed FeaturePython)
  n = 0.11
FEATURE [App::DocumentObjectGroupPython] N_element009  label="N_element : 0.033"  # scripted group (container) (typed FeaturePython)
  n = 0.033
FEATURE [App::DocumentObjectGroupPython] O_element013  label="O_element : 0.745"  # scripted group (container) (typed FeaturePython)
  n = 0.745
FEATURE [App::DocumentObjectGroupPython] Na_element002  label="Na_element : 0.002"  # scripted group (container) (typed FeaturePython)
  n = 0.001
FEATURE [App::DocumentObjectGroupPython] P_element001  label="P_element : 0.001"  # scripted group (container) (typed FeaturePython)
  n = 0.001
FEATURE [App::DocumentObjectGroupPython] S_element003  label="S_element : 0.002"  # scripted group (container) (typed FeaturePython)
  n = 0.002
FEATURE [App::DocumentObjectGroupPython] Cl_element002  label="Cl_element : 0.003"  # scripted group (container) (typed FeaturePython)
  n = 0.003
FEATURE [App::DocumentObjectGroupPython] K_element001  label="K_element : 0.002"  # scripted group (container) (typed FeaturePython)
  n = 0.002
FEATURE [App::DocumentObjectGroupPython] Fe_element001  label="Fe_element : 0.001"  # scripted group (container) (typed FeaturePython)
  n = 0.001
FEATURE [App::DocumentObjectGroupPython] G4_BLOOD_ICRP  # scripted group (container) (typed FeaturePython)
  Dunit = g/cm3
  Dvalue = 1.06
  Group = -> [H_element014,C_element014,N_element009,O_element013,Na_element002,P_element001,S_element003,Cl_element002,K_element001,Fe_element001]
  conduct = 2
  density = 1
  expand = 3
  formula = G4_BLOOD_ICRP
  name = G4_BLOOD_ICRP
  specific = 4
FEATURE [App::DocumentObjectGroupPython] H_element015  label="H_element : 0.064"  # scripted group (container) (typed FeaturePython)
  n = 0.064
FEATURE [App::DocumentObjectGroupPython] C_element015  label="C_element : 0.278"  # scripted group (container) (typed FeaturePython)
  n = 0.278
FEATURE [App::DocumentObjectGroupPython] N_element010  label="N_element : 0.027"  # scripted group (container) (typed FeaturePython)
  n = 0.027
FEATURE [App::DocumentObjectGroupPython] O_element014  label="O_element : 0.410"  # scripted group (container) (typed FeaturePython)
  n = 0.41
FEATURE [App::DocumentObjectGroupPython] Mg_element001  label="Mg_element : 0.002"  # scripted group (container) (typed FeaturePython)
  n = 0.002
FEATURE [App::DocumentObjectGroupPython] P_element002  label="P_element : 0.070"  # scripted group (container) (typed FeaturePython)
  n = 0.07
FEATURE [App::DocumentObjectGroupPython] S_element004  label="S_element : 0.003"  # scripted group (container) (typed FeaturePython)
  n = 0.002
FEATURE [App::DocumentObjectGroupPython] Ca_element003  label="Ca_element : 0.147"  # scripted group (container) (typed FeaturePython)
  n = 0.147
FEATURE [App::DocumentObjectGroupPython] G4_BONE_COMPACT_ICRU  # scripted group (container) (typed FeaturePython)
  Dunit = g/cm3
  Dvalue = 1.85
  Group = -> [H_element015,C_element015,N_element010,O_element014,Mg_element001,P_element002,S_element004,Ca_element003]
  conduct = 2
  density = 1
  expand = 3
  formula = G4_BONE_COMPACT_ICRU
  name = G4_BONE_COMPACT_ICRU
  specific = 4
FEATURE [App::DocumentObjectGroupPython] H_element016  label="H_element : 0.034"  # scripted group (container) (typed FeaturePython)
  n = 0.034
FEATURE [App::DocumentObjectGroupPython] C_element016  label="C_element : 0.155"  # scripted group (container) (typed FeaturePython)
  n = 0.155
FEATURE [App::DocumentObjectGroupPython] N_element011  label="N_element : 0.042"  # scripted group (container) (typed FeaturePython)
  n = 0.042
FEATURE [App::DocumentObjectGroupPython] O_element015  label="O_element : 0.435"  # scripted group (container) (typed FeaturePython)
  n = 0.435
FEATURE [App::DocumentObjectGroupPython] Na_element003  label="Na_element : 0.003"  # scripted group (container) (typed FeaturePython)
  n = 0.001
FEATURE [App::DocumentObjectGroupPython] Mg_element002  label="Mg_element : 0.003"  # scripted group (container) (typed FeaturePython)
  n = 0.002
FEATURE [App::DocumentObjectGroupPython] P_element003  label="P_element : 0.103"  # scripted group (container) (typed FeaturePython)
  n = 0.103
FEATURE [App::DocumentObjectGroupPython] S_element005  label="S_element : 0.004"  # scripted group (container) (typed FeaturePython)
  n = 0.003
FEATURE [App::DocumentObjectGroupPython] Ca_element004  label="Ca_element : 0.225"  # scripted group (container) (typed FeaturePython)
  n = 0.225
FEATURE [App::DocumentObjectGroupPython] G4_BONE_CORTICAL_ICRP  # scripted group (container) (typed FeaturePython)
  Dunit = g/cm3
  Dvalue = 1.92
  Group = -> [H_element016,C_element016,N_element011,O_element015,Na_element003,Mg_element002,P_element003,S_element005,Ca_element004]
  conduct = 2
  density = 1
  expand = 3
  formula = G4_BONE_CORTICAL_ICRP
  name = G4_BONE_CORTICAL_ICRP
  specific = 4
FEATURE [App::DocumentObjectGroupPython] B_element001  label="B_element : 4"  # scripted group (container) (typed FeaturePython)
  n = 4
  ref = B_element
FEATURE [App::DocumentObjectGroupPython] C_element017  label="C_element : 1"  # scripted group (container) (typed FeaturePython)
  n = 1
  ref = C_element
FEATURE [App::DocumentObjectGroupPython] G4_BORON_CARBIDE  # scripted group (container) (typed FeaturePython)
  Dunit = g/cm3
  Dvalue = 2.52
  Group = -> [B_element001,C_element017]
  conduct = 2
  density = 1
  expand = 3
  formula = G4_BORON_CARBIDE
  name = G4_BORON_CARBIDE
  specific = 4
FEATURE [App::DocumentObjectGroupPython] B_element002  label="B_element : 2"  # scripted group (container) (typed FeaturePython)
  n = 2
  ref = B_element
FEATURE [App::DocumentObjectGroupPython] O_element016  label="O_element : 006"  # scripted group (container) (typed FeaturePython)
  n = 3
  ref = O_element
FEATURE [App::DocumentObjectGroupPython] G4_BORON_OXIDE  # scripted group (container) (typed FeaturePython)
  Dunit = g/cm3
  Dvalue = 1.812
  Group = -> [B_element002,O_element016]
  conduct = 2
  density = 1
  expand = 3
  formula = G4_BORON_OXIDE
  name = G4_BORON_OXIDE
  specific = 4
FEATURE [App::DocumentObjectGroupPython] H_element017  label="H_element : 0.107"  # scripted group (container) (typed FeaturePython)
  n = 0.107
FEATURE [App::DocumentObjectGroupPython] C_element018  label="C_element : 0.145"  # scripted group (container) (typed FeaturePython)
  n = 0.145
FEATURE [App::DocumentObjectGroupPython] N_element012  label="N_element : 0.022"  # scripted group (container) (typed FeaturePython)
  n = 0.022
FEATURE [App::DocumentObjectGroupPython] O_element017  label="O_element : 0.712"  # scripted group (container) (typed FeaturePython)
  n = 0.712
FEATURE [App::DocumentObjectGroupPython] Na_element004  label="Na_element : 0.004"  # scripted group (container) (typed FeaturePython)
  n = 0.002
FEATURE [App::DocumentObjectGroupPython] P_element004  label="P_element : 0.004"  # scripted group (container) (typed FeaturePython)
  n = 0.004
FEATURE [App::DocumentObjectGroupPython] S_element006  label="S_element : 0.005"  # scripted group (container) (typed FeaturePython)
  n = 0.002
FEATURE [App::DocumentObjectGroupPython] Cl_element003  label="Cl_element : 0.004"  # scripted group (container) (typed FeaturePython)
  n = 0.003
FEATURE [App::DocumentObjectGroupPython] K_element002  label="K_element : 0.003"  # scripted group (container) (typed FeaturePython)
  n = 0.003
FEATURE [App::DocumentObjectGroupPython] G4_BRAIN_ICRP  # scripted group (container) (typed FeaturePython)
  Dunit = g/cm3
  Dvalue = 1.04
  Group = -> [H_element017,C_element018,N_element012,O_element017,Na_element004,P_element004,S_element006,Cl_element003,K_element002]
  conduct = 2
  density = 1
  expand = 3
  formula = G4_BRAIN_ICRP
  name = G4_BRAIN_ICRP
  specific = 4
FEATURE [App::DocumentObjectGroupPython] C_element019  label="C_element : 4"  # scripted group (container) (typed FeaturePython)
  n = 4
  ref = C_element
FEATURE [App::DocumentObjectGroupPython] H_element018  label="H_element : 010"  # scripted group (container) (typed FeaturePython)
  n = 10
  ref = H_element
FEATURE [App::DocumentObjectGroupPython] G4_BUTANE  # scripted group (container) (typed FeaturePython)
  Dunit = g/cm3
  Dvalue = 0.00249343
  Group = -> [C_element019,H_element018]
  conduct = 2
  density = 1
  expand = 3
  formula = G4_BUTANE
  name = G4_BUTANE
  specific = 4
FEATURE [App::DocumentObjectGroupPython] C_element020  label="C_element : 008"  # scripted group (container) (typed FeaturePython)
  n = 4
  ref = C_element
FEATURE [App::DocumentObjectGroupPython] H_element019  label="H_element : 011"  # scripted group (container) (typed FeaturePython)
  n = 10
  ref = H_element
FEATURE [App::DocumentObjectGroupPython] O_element018  label="O_element : 007"  # scripted group (container) (typed FeaturePython)
  n = 1
  ref = O_element
FEATURE [App::DocumentObjectGroupPython] G4_N_BUTYL_ALCOHOL  label="G4_N-BUTYL_ALCOHOL"  # scripted group (container) (typed FeaturePython)
  Dunit = g/cm3
  Dvalue = 0.8098
  Group = -> [C_element020,H_element019,O_element018]
  conduct = 2
  density = 1
  expand = 3
  formula = G4_N-BUTYL_ALCOHOL
  name = G4_N-BUTYL_ALCOHOL
  specific = 4
FEATURE [App::DocumentObjectGroupPython] H_element020  label="H_element : 0.025"  # scripted group (container) (typed FeaturePython)
  n = 0.02468
FEATURE [App::DocumentObjectGroupPython] C_element021  label="C_element : 0.502"  # scripted group (container) (typed FeaturePython)
  n = 0.501611
FEATURE [App::DocumentObjectGroupPython] O_element019  label="O_element : 0.005"  # scripted group (container) (typed FeaturePython)
  n = 0.004527
FEATURE [App::DocumentObjectGroupPython] F_element004  label="F_element : 0.465"  # scripted group (container) (typed FeaturePython)
  n = 0.465209
FEATURE [App::DocumentObjectGroupPython] Si_element001  label="Si_element : 0.004"  # scripted group (container) (typed FeaturePython)
  n = 0.003973
FEATURE [App::DocumentObjectGroupPython] G4_C_552  label="G4_C-552"  # scripted group (container) (typed FeaturePython)
  Dunit = g/cm3
  Dvalue = 1.76
  Group = -> [H_element020,C_element021,O_element019,F_element004,Si_element001]
  conduct = 2
  density = 1
  expand = 3
  formula = G4_C-552
  name = G4_C-552
  specific = 4
FEATURE [App::DocumentObjectGroupPython] Cd_element001  label="Cd_element : 1"  # scripted group (container) (typed FeaturePython)
  n = 1
  ref = Cd_element
FEATURE [App::DocumentObjectGroupPython] Te_element001  label="Te_element : 1"  # scripted group (container) (typed FeaturePython)
  n = 1
  ref = Te_element
FEATURE [App::DocumentObjectGroupPython] G4_CADMIUM_TELLURIDE  # scripted group (container) (typed FeaturePython)
  Dunit = g/cm3
  Dvalue = 6.2
  Group = -> [Cd_element001,Te_element001]
  conduct = 2
  density = 1
  expand = 3
  formula = G4_CADMIUM_TELLURIDE
  name = G4_CADMIUM_TELLURIDE
  specific = 4
FEATURE [App::DocumentObjectGroupPython] Cd_element002  label="Cd_element : 002"  # scripted group (container) (typed FeaturePython)
  n = 1
  ref = Cd_element
FEATURE [App::DocumentObjectGroupPython] W_element001  label="W_element : 1"  # scripted group (container) (typed FeaturePython)
  n = 1
  ref = W_element
FEATURE [App::DocumentObjectGroupPython] O_element020  label="O_element : 008"  # scripted group (container) (typed FeaturePython)
  n = 4
  ref = O_element
FEATURE [App::DocumentObjectGroupPython] G4_CADMIUM_TUNGSTATE  # scripted group (container) (typed FeaturePython)
  Dunit = g/cm3
  Dvalue = 7.9
  Group = -> [Cd_element002,W_element001,O_element020]
  conduct = 2
  density = 1
  expand = 3
  formula = G4_CADMIUM_TUNGSTATE
  name = G4_CADMIUM_TUNGSTATE
  specific = 4
FEATURE [App::DocumentObjectGroupPython] Ca_element005  label="Ca_element : 1"  # scripted group (container) (typed FeaturePython)
  n = 1
  ref = Ca_element
FEATURE [App::DocumentObjectGroupPython] C_element022  label="C_element : 009"  # scripted group (container) (typed FeaturePython)
  n = 1
  ref = C_element
FEATURE [App::DocumentObjectGroupPython] O_element021  label="O_element : 009"  # scripted group (container) (typed FeaturePython)
  n = 3
  ref = O_element
FEATURE [App::DocumentObjectGroupPython] G4_CALCIUM_CARBONATE  # scripted group (container) (typed FeaturePython)
  Dunit = g/cm3
  Dvalue = 2.8
  Group = -> [Ca_element005,C_element022,O_element021]
  conduct = 2
  density = 1
  expand = 3
  formula = G4_CALCIUM_CARBONATE
  name = G4_CALCIUM_CARBONATE
  specific = 4
FEATURE [App::DocumentObjectGroupPython] Ca_element006  label="Ca_element : 002"  # scripted group (container) (typed FeaturePython)
  n = 1
  ref = Ca_element
FEATURE [App::DocumentObjectGroupPython] F_element005  label="F_element : 003"  # scripted group (container) (typed FeaturePython)
  n = 2
  ref = F_element
FEATURE [App::DocumentObjectGroupPython] G4_CALCIUM_FLUORIDE  # scripted group (container) (typed FeaturePython)
  Dunit = g/cm3
  Dvalue = 3.18
  Group = -> [Ca_element006,F_element005]
  conduct = 2
  density = 1
  expand = 3
  formula = G4_CALCIUM_FLUORIDE
  name = G4_CALCIUM_FLUORIDE
  specific = 4
FEATURE [App::DocumentObjectGroupPython] Ca_element007  label="Ca_element : 003"  # scripted group (container) (typed FeaturePython)
  n = 1
  ref = Ca_element
FEATURE [App::DocumentObjectGroupPython] O_element022  label="O_element : 010"  # scripted group (container) (typed FeaturePython)
  n = 1
  ref = O_element
FEATURE [App::DocumentObjectGroupPython] G4_CALCIUM_OXIDE  # scripted group (container) (typed FeaturePython)
  Dunit = g/cm3
  Dvalue = 3.3
  Group = -> [Ca_element007,O_element022]
  conduct = 2
  density = 1
  expand = 3
  formula = G4_CALCIUM_OXIDE
  name = G4_CALCIUM_OXIDE
  specific = 4
FEATURE [App::DocumentObjectGroupPython] Ca_element008  label="Ca_element : 004"  # scripted group (container) (typed FeaturePython)
  n = 1
  ref = Ca_element
FEATURE [App::DocumentObjectGroupPython] S_element007  label="S_element : 002"  # scripted group (container) (typed FeaturePython)
  n = 1
  ref = S_element
FEATURE [App::DocumentObjectGroupPython] O_element023  label="O_element : 011"  # scripted group (container) (typed FeaturePython)
  n = 4
  ref = O_element
FEATURE [App::DocumentObjectGroupPython] G4_CALCIUM_SULFATE  # scripted group (container) (typed FeaturePython)
  Dunit = g/cm3
  Dvalue = 2.96
  Group = -> [Ca_element008,S_element007,O_element023]
  conduct = 2
  density = 1
  expand = 3
  formula = G4_CALCIUM_SULFATE
  name = G4_CALCIUM_SULFATE
  specific = 4
FEATURE [App::DocumentObjectGroupPython] Ca_element009  label="Ca_element : 005"  # scripted group (container) (typed FeaturePython)
  n = 1
  ref = Ca_element
FEATURE [App::DocumentObjectGroupPython] W_element002  label="W_element : 002"  # scripted group (container) (typed FeaturePython)
  n = 1
  ref = W_element
FEATURE [App::DocumentObjectGroupPython] O_element024  label="O_element : 012"  # scripted group (container) (typed FeaturePython)
  n = 4
  ref = O_element
FEATURE [App::DocumentObjectGroupPython] G4_CALCIUM_TUNGSTATE  # scripted group (container) (typed FeaturePython)
  Dunit = g/cm3
  Dvalue = 6.062
  Group = -> [Ca_element009,W_element002,O_element024]
  conduct = 2
  density = 1
  expand = 3
  formula = G4_CALCIUM_TUNGSTATE
  name = G4_CALCIUM_TUNGSTATE
  specific = 4
FEATURE [App::DocumentObjectGroupPython] C_element023  label="C_element : 010"  # scripted group (container) (typed FeaturePython)
  n = 1
  ref = C_element
FEATURE [App::DocumentObjectGroupPython] O_element025  label="O_element : 013"  # scripted group (container) (typed FeaturePython)
  n = 2
  ref = O_element
FEATURE [App::DocumentObjectGroupPython] G4_CARBON_DIOXIDE  # scripted group (container) (typed FeaturePython)
  Dunit = g/cm3
  Dvalue = 0.00184212
  Group = -> [C_element023,O_element025]
  conduct = 2
  density = 1
  expand = 3
  formula = G4_CARBON_DIOXIDE
  name = G4_CARBON_DIOXIDE
  specific = 4
FEATURE [App::DocumentObjectGroupPython] C_element024  label="C_element : 011"  # scripted group (container) (typed FeaturePython)
  n = 1
  ref = C_element
FEATURE [App::DocumentObjectGroupPython] Cl_element004  label="Cl_element : 4"  # scripted group (container) (typed FeaturePython)
  n = 4
  ref = Cl_element
FEATURE [App::DocumentObjectGroupPython] G4_CARBON_TETRACHLORIDE  # scripted group (container) (typed FeaturePython)
  Dunit = g/cm3
  Dvalue = 1.594
  Group = -> [C_element024,Cl_element004]
  conduct = 2
  density = 1
  expand = 3
  formula = G4_CARBON_TETRACHLORIDE
  name = G4_CARBON_TETRACHLORIDE
  specific = 4
FEATURE [App::DocumentObjectGroupPython] C_element025  label="C_element : 012"  # scripted group (container) (typed FeaturePython)
  n = 6
  ref = C_element
FEATURE [App::DocumentObjectGroupPython] H_element021  label="H_element : 012"  # scripted group (container) (typed FeaturePython)
  n = 10
  ref = H_element
FEATURE [App::DocumentObjectGroupPython] O_element026  label="O_element : 5"  # scripted group (container) (typed FeaturePython)
  n = 5
  ref = O_element
FEATURE [App::DocumentObjectGroupPython] G4_CELLULOSE_CELLOPHANE  # scripted group (container) (typed FeaturePython)
  Dunit = g/cm3
  Dvalue = 1.42
  Group = -> [C_element025,H_element021,O_element026]
  conduct = 2
  density = 1
  expand = 3
  formula = G4_CELLULOSE_CELLOPHANE
  name = G4_CELLULOSE_CELLOPHANE
  specific = 4
FEATURE [App::DocumentObjectGroupPython] H_element022  label="H_element : 0.067"  # scripted group (container) (typed FeaturePython)
  n = 0.067125
FEATURE [App::DocumentObjectGroupPython] C_element026  label="C_element : 0.545"  # scripted group (container) (typed FeaturePython)
  n = 0.545403
FEATURE [App::DocumentObjectGroupPython] O_element027  label="O_element : 0.387"  # scripted group (container) (typed FeaturePython)
  n = 0.387472
FEATURE [App::DocumentObjectGroupPython] G4_CELLULOSE_BUTYRATE  # scripted group (container) (typed FeaturePython)
  Dunit = g/cm3
  Dvalue = 1.2
  Group = -> [H_element022,C_element026,O_element027]
  conduct = 2
  density = 1
  expand = 3
  formula = G4_CELLULOSE_BUTYRATE
  name = G4_CELLULOSE_BUTYRATE
  specific = 4
FEATURE [App::DocumentObjectGroupPython] H_element023  label="H_element : 0.029"  # scripted group (container) (typed FeaturePython)
  n = 0.029216
FEATURE [App::DocumentObjectGroupPython] C_element027  label="C_element : 0.271"  # scripted group (container) (typed FeaturePython)
  n = 0.271296
FEATURE [App::DocumentObjectGroupPython] N_element013  label="N_element : 0.121"  # scripted group (container) (typed FeaturePython)
  n = 0.121276
FEATURE [App::DocumentObjectGroupPython] O_element028  label="O_element : 0.578"  # scripted group (container) (typed FeaturePython)
  n = 0.578212
FEATURE [App::DocumentObjectGroupPython] G4_CELLULOSE_NITRATE  # scripted group (container) (typed FeaturePython)
  Dunit = g/cm3
  Dvalue = 1.49
  Group = -> [H_element023,C_element027,N_element013,O_element028]
  conduct = 2
  density = 1
  expand = 3
  formula = G4_CELLULOSE_NITRATE
  name = G4_CELLULOSE_NITRATE
  specific = 4
FEATURE [App::DocumentObjectGroupPython] H_element024  label="H_element : 0.108"  # scripted group (container) (typed FeaturePython)
  n = 0.107596
FEATURE [App::DocumentObjectGroupPython] N_element014  label="N_element : 0.001"  # scripted group (container) (typed FeaturePython)
  n = 0.0008
FEATURE [App::DocumentObjectGroupPython] O_element029  label="O_element : 0.875"  # scripted group (container) (typed FeaturePython)
  n = 0.874976
FEATURE [App::DocumentObjectGroupPython] S_element008  label="S_element : 0.015"  # scripted group (container) (typed FeaturePython)
  n = 0.014627
FEATURE [App::DocumentObjectGroupPython] Ce_element001  label="Ce_element : 0.002"  # scripted group (container) (typed FeaturePython)
  n = 0.002001
FEATURE [App::DocumentObjectGroupPython] G4_CERIC_SULFATE  # scripted group (container) (typed FeaturePython)
  Dunit = g/cm3
  Dvalue = 1.03
  Group = -> [H_element024,N_element014,O_element029,S_element008,Ce_element001]
  conduct = 2
  density = 1
  expand = 3
  formula = G4_CERIC_SULFATE
  name = G4_CERIC_SULFATE
  specific = 4
FEATURE [App::DocumentObjectGroupPython] Cs_element001  label="Cs_element : 1"  # scripted group (container) (typed FeaturePython)
  n = 1
  ref = Cs_element
FEATURE [App::DocumentObjectGroupPython] F_element006  label="F_element : 1"  # scripted group (container) (typed FeaturePython)
  n = 1
  ref = F_element
FEATURE [App::DocumentObjectGroupPython] G4_CESIUM_FLUORIDE  # scripted group (container) (typed FeaturePython)
  Dunit = g/cm3
  Dvalue = 4.115
  Group = -> [Cs_element001,F_element006]
  conduct = 2
  density = 1
  expand = 3
  formula = G4_CESIUM_FLUORIDE
  name = G4_CESIUM_FLUORIDE
  specific = 4
FEATURE [App::DocumentObjectGroupPython] Cs_element002  label="Cs_element : 002"  # scripted group (container) (typed FeaturePython)
  n = 1
  ref = Cs_element
FEATURE [App::DocumentObjectGroupPython] I_element001  label="I_element : 1"  # scripted group (container) (typed FeaturePython)
  n = 1
  ref = I_element
FEATURE [App::DocumentObjectGroupPython] G4_CESIUM_IODIDE  # scripted group (container) (typed FeaturePython)
  Dunit = g/cm3
  Dvalue = 4.51
  Group = -> [Cs_element002,I_element001]
  conduct = 2
  density = 1
  expand = 3
  formula = G4_CESIUM_IODIDE
  name = G4_CESIUM_IODIDE
  specific = 4
FEATURE [App::DocumentObjectGroupPython] C_element028  label="C_element : 013"  # scripted group (container) (typed FeaturePython)
  n = 6
  ref = C_element
FEATURE [App::DocumentObjectGroupPython] H_element025  label="H_element : 013"  # scripted group (container) (typed FeaturePython)
  n = 5
  ref = H_element
FEATURE [App::DocumentObjectGroupPython] Cl_element005  label="Cl_element : 1"  # scripted group (container) (typed FeaturePython)
  n = 1
  ref = Cl_element
FEATURE [App::DocumentObjectGroupPython] G4_CHLOROBENZENE  # scripted group (container) (typed FeaturePython)
  Dunit = g/cm3
  Dvalue = 1.1058
  Group = -> [C_element028,H_element025,Cl_element005]
  conduct = 2
  density = 1
  expand = 3
  formula = G4_CHLOROBENZENE
  name = G4_CHLOROBENZENE
  specific = 4
FEATURE [App::DocumentObjectGroupPython] C_element029  label="C_element : 014"  # scripted group (container) (typed FeaturePython)
  n = 1
  ref = C_element
FEATURE [App::DocumentObjectGroupPython] H_element026  label="H_element : 1"  # scripted group (container) (typed FeaturePython)
  n = 1
  ref = H_element
FEATURE [App::DocumentObjectGroupPython] Cl_element006  label="Cl_element : 3"  # scripted group (container) (typed FeaturePython)
  n = 3
  ref = Cl_element
FEATURE [App::DocumentObjectGroupPython] G4_CHLOROFORM  # scripted group (container) (typed FeaturePython)
  Dunit = g/cm3
  Dvalue = 1.4832
  Group = -> [C_element029,H_element026,Cl_element006]
  conduct = 2
  density = 1
  expand = 3
  formula = G4_CHLOROFORM
  name = G4_CHLOROFORM
  specific = 4
FEATURE [App::DocumentObjectGroupPython] H_element027  label="H_element : 0.010"  # scripted group (container) (typed FeaturePython)
  n = 0.01
FEATURE [App::DocumentObjectGroupPython] C_element030  label="C_element : 0.001"  # scripted group (container) (typed FeaturePython)
  n = 0.001
FEATURE [App::DocumentObjectGroupPython] O_element030  label="O_element : 0.529"  # scripted group (container) (typed FeaturePython)
  n = 0.529107
FEATURE [App::DocumentObjectGroupPython] Na_element005  label="Na_element : 0.016"  # scripted group (container) (typed FeaturePython)
  n = 0.016
FEATURE [App::DocumentObjectGroupPython] Mg_element003  label="Mg_element : 0.004"  # scripted group (container) (typed FeaturePython)
  n = 0.002
FEATURE [App::DocumentObjectGroupPython] Al_element002  label="Al_element : 0.034"  # scripted group (container) (typed FeaturePython)
  n = 0.033872
FEATURE [App::DocumentObjectGroupPython] Si_element002  label="Si_element : 0.337"  # scripted group (container) (typed FeaturePython)
  n = 0.337021
FEATURE [App::DocumentObjectGroupPython] K_element003  label="K_element : 0.013"  # scripted group (container) (typed FeaturePython)
  n = 0.013
FEATURE [App::DocumentObjectGroupPython] Ca_element010  label="Ca_element : 0.044"  # scripted group (container) (typed FeaturePython)
  n = 0.044
FEATURE [App::DocumentObjectGroupPython] Fe_element002  label="Fe_element : 0.014"  # scripted group (container) (typed FeaturePython)
  n = 0.014
FEATURE [App::DocumentObjectGroupPython] G4_CONCRETE  # scripted group (container) (typed FeaturePython)
  Dunit = g/cm3
  Dvalue = 2.3
  Group = -> [H_element027,C_element030,O_element030,Na_element005,Mg_element003,Al_element002,Si_element002,K_element003,Ca_element010,Fe_element002]
  conduct = 2
  density = 1
  expand = 3
  formula = G4_CONCRETE
  name = G4_CONCRETE
  specific = 4
FEATURE [App::DocumentObjectGroupPython] C_element031  label="C_element : 015"  # scripted group (container) (typed FeaturePython)
  n = 6
  ref = C_element
FEATURE [App::DocumentObjectGroupPython] H_element028  label="H_element : 12"  # scripted group (container) (typed FeaturePython)
  n = 12
  ref = H_element
FEATURE [App::DocumentObjectGroupPython] G4_CYCLOHEXANE  # scripted group (container) (typed FeaturePython)
  Dunit = g/cm3
  Dvalue = 0.779
  Group = -> [C_element031,H_element028]
  conduct = 2
  density = 1
  expand = 3
  formula = G4_CYCLOHEXANE
  name = G4_CYCLOHEXANE
  specific = 4
FEATURE [App::DocumentObjectGroupPython] C_element032  label="C_element : 016"  # scripted group (container) (typed FeaturePython)
  n = 6
  ref = C_element
FEATURE [App::DocumentObjectGroupPython] H_element029  label="H_element : 4"  # scripted group (container) (typed FeaturePython)
  n = 4
  ref = H_element
FEATURE [App::DocumentObjectGroupPython] Cl_element007  label="Cl_element : 2"  # scripted group (container) (typed FeaturePython)
  n = 2
  ref = Cl_element
FEATURE [App::DocumentObjectGroupPython] G4_1_2_DICHLOROBENZENE  label="G4_1.2-DICHLOROBENZENE"  # scripted group (container) (typed FeaturePython)
  Dunit = g/cm3
  Dvalue = 1.3048
  Group = -> [C_element032,H_element029,Cl_element007]
  conduct = 2
  density = 1
  expand = 3
  formula = G4_1.2-DICHLOROBENZENE
  name = G4_1.2-DICHLOROBENZENE
  specific = 4
FEATURE [App::DocumentObjectGroupPython] C_element033  label="C_element : 017"  # scripted group (container) (typed FeaturePython)
  n = 4
  ref = C_element
FEATURE [App::DocumentObjectGroupPython] H_element030  label="H_element : 8"  # scripted group (container) (typed FeaturePython)
  n = 8
  ref = H_element
FEATURE [App::DocumentObjectGroupPython] O_element031  label="O_element : 014"  # scripted group (container) (typed FeaturePython)
  n = 1
  ref = O_element
FEATURE [App::DocumentObjectGroupPython] Cl_element008  label="Cl_element : 005"  # scripted group (container) (typed FeaturePython)
  n = 2
  ref = Cl_element
FEATURE [App::DocumentObjectGroupPython] G4_DICHLORODIETHYL_ETHER  # scripted group (container) (typed FeaturePython)
  Dunit = g/cm3
  Dvalue = 1.2199
  Group = -> [C_element033,H_element030,O_element031,Cl_element008]
  conduct = 2
  density = 1
  expand = 3
  formula = G4_DICHLORODIETHYL_ETHER
  name = G4_DICHLORODIETHYL_ETHER
  specific = 4
FEATURE [App::DocumentObjectGroupPython] C_element034  label="C_element : 018"  # scripted group (container) (typed FeaturePython)
  n = 2
  ref = C_element
FEATURE [App::DocumentObjectGroupPython] H_element031  label="H_element : 014"  # scripted group (container) (typed FeaturePython)
  n = 4
  ref = H_element
FEATURE [App::DocumentObjectGroupPython] Cl_element009  label="Cl_element : 006"  # scripted group (container) (typed FeaturePython)
  n = 2
  ref = Cl_element
FEATURE [App::DocumentObjectGroupPython] G4_1_2_DICHLOROETHANE  label="G4_1.2-DICHLOROETHANE"  # scripted group (container) (typed FeaturePython)
  Dunit = g/cm3
  Dvalue = 1.2351
  Group = -> [C_element034,H_element031,Cl_element009]
  conduct = 2
  density = 1
  expand = 3
  formula = G4_1.2-DICHLOROETHANE
  name = G4_1.2-DICHLOROETHANE
  specific = 4
FEATURE [App::DocumentObjectGroupPython] C_element035  label="C_element : 019"  # scripted group (container) (typed FeaturePython)
  n = 4
  ref = C_element
FEATURE [App::DocumentObjectGroupPython] H_element032  label="H_element : 015"  # scripted group (container) (typed FeaturePython)
  n = 10
  ref = H_element
FEATURE [App::DocumentObjectGroupPython] O_element032  label="O_element : 015"  # scripted group (container) (typed FeaturePython)
  n = 1
  ref = O_element
FEATURE [App::DocumentObjectGroupPython] G4_DIETHYL_ETHER  # scripted group (container) (typed FeaturePython)
  Dunit = g/cm3
  Dvalue = 0.71378
  Group = -> [C_element035,H_element032,O_element032]
  conduct = 2
  density = 1
  expand = 3
  formula = G4_DIETHYL_ETHER
  name = G4_DIETHYL_ETHER
  specific = 4
FEATURE [App::DocumentObjectGroupPython] C_element036  label="C_element : 020"  # scripted group (container) (typed FeaturePython)
  n = 3
  ref = C_element
FEATURE [App::DocumentObjectGroupPython] H_element033  label="H_element : 016"  # scripted group (container) (typed FeaturePython)
  n = 7
  ref = H_element
FEATURE [App::DocumentObjectGroupPython] N_element015  label="N_element : 008"  # scripted group (container) (typed FeaturePython)
  n = 1
  ref = N_element
FEATURE [App::DocumentObjectGroupPython] O_element033  label="O_element : 016"  # scripted group (container) (typed FeaturePython)
  n = 1
  ref = O_element
FEATURE [App::DocumentObjectGroupPython] G4_N_N_DIMETHYL_FORMAMIDE  label="G4_N.N-DIMETHYL_FORMAMIDE"  # scripted group (container) (typed FeaturePython)
  Dunit = g/cm3
  Dvalue = 0.9487
  Group = -> [C_element036,H_element033,N_element015,O_element033]
  conduct = 2
  density = 1
  expand = 3
  formula = G4_N.N-DIMETHYL_FORMAMIDE
  name = G4_N.N-DIMETHYL_FORMAMIDE
  specific = 4
FEATURE [App::DocumentObjectGroupPython] C_element037  label="C_element : 021"  # scripted group (container) (typed FeaturePython)
  n = 2
  ref = C_element
FEATURE [App::DocumentObjectGroupPython] H_element034  label="H_element : 017"  # scripted group (container) (typed FeaturePython)
  n = 6
  ref = H_element
FEATURE [App::DocumentObjectGroupPython] O_element034  label="O_element : 017"  # scripted group (container) (typed FeaturePython)
  n = 1
  ref = O_element
FEATURE [App::DocumentObjectGroupPython] S_element009  label="S_element : 003"  # scripted group (container) (typed FeaturePython)
  n = 1
  ref = S_element
FEATURE [App::DocumentObjectGroupPython] G4_DIMETHYL_SULFOXIDE  # scripted group (container) (typed FeaturePython)
  Dunit = g/cm3
  Dvalue = 1.1014
  Group = -> [C_element037,H_element034,O_element034,S_element009]
  conduct = 2
  density = 1
  expand = 3
  formula = G4_DIMETHYL_SULFOXIDE
  name = G4_DIMETHYL_SULFOXIDE
  specific = 4
FEATURE [App::DocumentObjectGroupPython] C_element038  label="C_element : 022"  # scripted group (container) (typed FeaturePython)
  n = 2
  ref = C_element
FEATURE [App::DocumentObjectGroupPython] H_element035  label="H_element : 018"  # scripted group (container) (typed FeaturePython)
  n = 6
  ref = H_element
FEATURE [App::DocumentObjectGroupPython] G4_ETHANE  # scripted group (container) (typed FeaturePython)
  Dunit = g/cm3
  Dvalue = 0.00125324
  Group = -> [C_element038,H_element035]
  conduct = 2
  density = 1
  expand = 3
  formula = G4_ETHANE
  name = G4_ETHANE
  specific = 4
FEATURE [App::DocumentObjectGroupPython] C_element039  label="C_element : 023"  # scripted group (container) (typed FeaturePython)
  n = 2
  ref = C_element
FEATURE [App::DocumentObjectGroupPython] H_element036  label="H_element : 019"  # scripted group (container) (typed FeaturePython)
  n = 6
  ref = H_element
FEATURE [App::DocumentObjectGroupPython] O_element035  label="O_element : 018"  # scripted group (container) (typed FeaturePython)
  n = 1
  ref = O_element
FEATURE [App::DocumentObjectGroupPython] G4_ETHYL_ALCOHOL  # scripted group (container) (typed FeaturePython)
  Dunit = g/cm3
  Dvalue = 0.7893
  Group = -> [C_element039,H_element036,O_element035]
  conduct = 2
  density = 1
  expand = 3
  formula = G4_ETHYL_ALCOHOL
  name = G4_ETHYL_ALCOHOL
  specific = 4
FEATURE [App::DocumentObjectGroupPython] H_element037  label="H_element : 0.090"  # scripted group (container) (typed FeaturePython)
  n = 0.090027
FEATURE [App::DocumentObjectGroupPython] C_element040  label="C_element : 0.585"  # scripted group (container) (typed FeaturePython)
  n = 0.585182
FEATURE [App::DocumentObjectGroupPython] O_element036  label="O_element : 0.325"  # scripted group (container) (typed FeaturePython)
  n = 0.324791
FEATURE [App::DocumentObjectGroupPython] G4_ETHYL_CELLULOSE  # scripted group (container) (typed FeaturePython)
  Dunit = g/cm3
  Dvalue = 1.13
  Group = -> [H_element037,C_element040,O_element036]
  conduct = 2
  density = 1
  expand = 3
  formula = G4_ETHYL_CELLULOSE
  name = G4_ETHYL_CELLULOSE
  specific = 4
FEATURE [App::DocumentObjectGroupPython] C_element041  label="C_element : 024"  # scripted group (container) (typed FeaturePython)
  n = 2
  ref = C_element
FEATURE [App::DocumentObjectGroupPython] H_element038  label="H_element : 020"  # scripted group (container) (typed FeaturePython)
  n = 4
  ref = H_element
FEATURE [App::DocumentObjectGroupPython] G4_ETHYLENE  # scripted group (container) (typed FeaturePython)
  Dunit = g/cm3
  Dvalue = 0.00117497
  Group = -> [C_element041,H_element038]
  conduct = 2
  density = 1
  expand = 3
  formula = G4_ETHYLENE
  name = G4_ETHYLENE
  specific = 4
FEATURE [App::DocumentObjectGroupPython] H_element039  label="H_element : 0.096"  # scripted group (container) (typed FeaturePython)
  n = 0.096
FEATURE [App::DocumentObjectGroupPython] C_element042  label="C_element : 0.195"  # scripted group (container) (typed FeaturePython)
  n = 0.195
FEATURE [App::DocumentObjectGroupPython] N_element016  label="N_element : 0.057"  # scripted group (container) (typed FeaturePython)
  n = 0.057
FEATURE [App::DocumentObjectGroupPython] O_element037  label="O_element : 0.646"  # scripted group (container) (typed FeaturePython)
  n = 0.646
FEATURE [App::DocumentObjectGroupPython] Na_element006  label="Na_element : 0.017"  # scripted group (container) (typed FeaturePython)
  n = 0.001
FEATURE [App::DocumentObjectGroupPython] P_element005  label="P_element : 0.104"  # scripted group (container) (typed FeaturePython)
  n = 0.001
FEATURE [App::DocumentObjectGroupPython] S_element010  label="S_element : 0.016"  # scripted group (container) (typed FeaturePython)
  n = 0.003
FEATURE [App::DocumentObjectGroupPython] Cl_element010  label="Cl_element : 0.005"  # scripted group (container) (typed FeaturePython)
  n = 0.001
FEATURE [App::DocumentObjectGroupPython] G4_EYE_LENS_ICRP  # scripted group (container) (typed FeaturePython)
  Dunit = g/cm3
  Dvalue = 1.07
  Group = -> [H_element039,C_element042,N_element016,O_element037,Na_element006,P_element005,S_element010,Cl_element010]
  conduct = 2
  density = 1
  expand = 3
  formula = G4_EYE_LENS_ICRP
  name = G4_EYE_LENS_ICRP
  specific = 4
FEATURE [App::DocumentObjectGroupPython] Fe_element003  label="Fe_element : 2"  # scripted group (container) (typed FeaturePython)
  n = 2
  ref = Fe_element
FEATURE [App::DocumentObjectGroupPython] O_element038  label="O_element : 019"  # scripted group (container) (typed FeaturePython)
  n = 3
  ref = O_element
FEATURE [App::DocumentObjectGroupPython] G4_FERRIC_OXIDE  # scripted group (container) (typed FeaturePython)
  Dunit = g/cm3
  Dvalue = 5.2
  Group = -> [Fe_element003,O_element038]
  conduct = 2
  density = 1
  expand = 3
  formula = G4_FERRIC_OXIDE
  name = G4_FERRIC_OXIDE
  specific = 4
FEATURE [App::DocumentObjectGroupPython] Fe_element004  label="Fe_element : 1"  # scripted group (container) (typed FeaturePython)
  n = 1
  ref = Fe_element
FEATURE [App::DocumentObjectGroupPython] B_element003  label="B_element : 1"  # scripted group (container) (typed FeaturePython)
  n = 1
  ref = B_element
FEATURE [App::DocumentObjectGroupPython] G4_FERROBORIDE  # scripted group (container) (typed FeaturePython)
  Dunit = g/cm3
  Dvalue = 7.15
  Group = -> [Fe_element004,B_element003]
  conduct = 2
  density = 1
  expand = 3
  formula = G4_FERROBORIDE
  name = G4_FERROBORIDE
  specific = 4
FEATURE [App::DocumentObjectGroupPython] Fe_element005  label="Fe_element : 003"  # scripted group (container) (typed FeaturePython)
  n = 1
  ref = Fe_element
FEATURE [App::DocumentObjectGroupPython] O_element039  label="O_element : 020"  # scripted group (container) (typed FeaturePython)
  n = 1
  ref = O_element
FEATURE [App::DocumentObjectGroupPython] G4_FERROUS_OXIDE  # scripted group (container) (typed FeaturePython)
  Dunit = g/cm3
  Dvalue = 5.7
  Group = -> [Fe_element005,O_element039]
  conduct = 2
  density = 1
  expand = 3
  formula = G4_FERROUS_OXIDE
  name = G4_FERROUS_OXIDE
  specific = 4
FEATURE [App::DocumentObjectGroupPython] H_element040  label="H_element : 0.115"  # scripted group (container) (typed FeaturePython)
  n = 0.108259
FEATURE [App::DocumentObjectGroupPython] N_element017  label="N_element : 0.000"  # scripted group (container) (typed FeaturePython)
  n = 2.7e-05
FEATURE [App::DocumentObjectGroupPython] O_element040  label="O_element : 0.879"  # scripted group (container) (typed FeaturePython)
  n = 0.878636
FEATURE [App::DocumentObjectGroupPython] Na_element007  label="Na_element : 0.000"  # scripted group (container) (typed FeaturePython)
  n = 2.2e-05
FEATURE [App::DocumentObjectGroupPython] S_element011  label="S_element : 0.013"  # scripted group (container) (typed FeaturePython)
  n = 0.012968
FEATURE [App::DocumentObjectGroupPython] Cl_element011  label="Cl_element : 0.000"  # scripted group (container) (typed FeaturePython)
  n = 3.4e-05
FEATURE [App::DocumentObjectGroupPython] Fe_element006  label="Fe_element : 0.000"  # scripted group (container) (typed FeaturePython)
  n = 5.4e-05
FEATURE [App::DocumentObjectGroupPython] G4_FERROUS_SULFATE  # scripted group (container) (typed FeaturePython)
  Dunit = g/cm3
  Dvalue = 1.024
  Group = -> [H_element040,N_element017,O_element040,Na_element007,S_element011,Cl_element011,Fe_element006]
  conduct = 2
  density = 1
  expand = 3
  formula = G4_FERROUS_SULFATE
  name = G4_FERROUS_SULFATE
  specific = 4
FEATURE [App::DocumentObjectGroupPython] C_element043  label="C_element : 0.099"  # scripted group (container) (typed FeaturePython)
  n = 0.099335
FEATURE [App::DocumentObjectGroupPython] F_element007  label="F_element : 0.314"  # scripted group (container) (typed FeaturePython)
  n = 0.314247
FEATURE [App::DocumentObjectGroupPython] Cl_element012  label="Cl_element : 0.586"  # scripted group (container) (typed FeaturePython)
  n = 0.586418
FEATURE [App::DocumentObjectGroupPython] G4_FREON_12  label="G4_FREON-12"  # scripted group (container) (typed FeaturePython)
  Dunit = g/cm3
  Dvalue = 1.12
  Group = -> [C_element043,F_element007,Cl_element012]
  conduct = 2
  density = 1
  expand = 3
  formula = G4_FREON-12
  name = G4_FREON-12
  specific = 4
FEATURE [App::DocumentObjectGroupPython] C_element044  label="C_element : 0.057"  # scripted group (container) (typed FeaturePython)
  n = 0.057245
FEATURE [App::DocumentObjectGroupPython] F_element008  label="F_element : 0.181"  # scripted group (container) (typed FeaturePython)
  n = 0.181096
FEATURE [App::DocumentObjectGroupPython] Br_element001  label="Br_element : 0.762"  # scripted group (container) (typed FeaturePython)
  n = 0.761659
FEATURE [App::DocumentObjectGroupPython] G4_FREON_12B2  label="G4_FREON-12B2"  # scripted group (container) (typed FeaturePython)
  Dunit = g/cm3
  Dvalue = 1.8
  Group = -> [C_element044,F_element008,Br_element001]
  conduct = 2
  density = 1
  expand = 3
  formula = G4_FREON-12B2
  name = G4_FREON-12B2
  specific = 4
FEATURE [App::DocumentObjectGroupPython] C_element045  label="C_element : 0.115"  # scripted group (container) (typed FeaturePython)
  n = 0.114983
FEATURE [App::DocumentObjectGroupPython] F_element009  label="F_element : 0.546"  # scripted group (container) (typed FeaturePython)
  n = 0.545621
FEATURE [App::DocumentObjectGroupPython] Cl_element013  label="Cl_element : 0.339"  # scripted group (container) (typed FeaturePython)
  n = 0.339396
FEATURE [App::DocumentObjectGroupPython] G4_FREON_13  label="G4_FREON-13"  # scripted group (container) (typed FeaturePython)
  Dunit = g/cm3
  Dvalue = 0.95
  Group = -> [C_element045,F_element009,Cl_element013]
  conduct = 2
  density = 1
  expand = 3
  formula = G4_FREON-13
  name = G4_FREON-13
  specific = 4
FEATURE [App::DocumentObjectGroupPython] C_element046  label="C_element : 025"  # scripted group (container) (typed FeaturePython)
  n = 1
  ref = C_element
FEATURE [App::DocumentObjectGroupPython] F_element010  label="F_element : 3"  # scripted group (container) (typed FeaturePython)
  n = 3
  ref = F_element
FEATURE [App::DocumentObjectGroupPython] Br_element002  label="Br_element : 1"  # scripted group (container) (typed FeaturePython)
  n = 1
  ref = Br_element
FEATURE [App::DocumentObjectGroupPython] G4_FREON_13B1  label="G4_FREON-13B1"  # scripted group (container) (typed FeaturePython)
  Dunit = g/cm3
  Dvalue = 1.5
  Group = -> [C_element046,F_element010,Br_element002]
  conduct = 2
  density = 1
  expand = 3
  formula = G4_FREON-13B1
  name = G4_FREON-13B1
  specific = 4
FEATURE [App::DocumentObjectGroupPython] C_element047  label="C_element : 0.061"  # scripted group (container) (typed FeaturePython)
  n = 0.061309
FEATURE [App::DocumentObjectGroupPython] F_element011  label="F_element : 0.291"  # scripted group (container) (typed FeaturePython)
  n = 0.290924
FEATURE [App::DocumentObjectGroupPython] I_element002  label="I_element : 0.648"  # scripted group (container) (typed FeaturePython)
  n = 0.647767
FEATURE [App::DocumentObjectGroupPython] G4_FREON_13I1  label="G4_FREON-13I1"  # scripted group (container) (typed FeaturePython)
  Dunit = g/cm3
  Dvalue = 1.8
  Group = -> [C_element047,F_element011,I_element002]
  conduct = 2
  density = 1
  expand = 3
  formula = G4_FREON-13I1
  name = G4_FREON-13I1
  specific = 4
FEATURE [App::DocumentObjectGroupPython] Gd_element001  label="Gd_element : 2"  # scripted group (container) (typed FeaturePython)
  n = 2
  ref = Gd_element
FEATURE [App::DocumentObjectGroupPython] O_element041  label="O_element : 021"  # scripted group (container) (typed FeaturePython)
  n = 2
  ref = O_element
FEATURE [App::DocumentObjectGroupPython] S_element012  label="S_element : 004"  # scripted group (container) (typed FeaturePython)
  n = 1
  ref = S_element
FEATURE [App::DocumentObjectGroupPython] G4_GADOLINIUM_OXYSULFIDE  # scripted group (container) (typed FeaturePython)
  Dunit = g/cm3
  Dvalue = 7.44
  Group = -> [Gd_element001,O_element041,S_element012]
  conduct = 2
  density = 1
  expand = 3
  formula = G4_GADOLINIUM_OXYSULFIDE
  name = G4_GADOLINIUM_OXYSULFIDE
  specific = 4
FEATURE [App::DocumentObjectGroupPython] Ga_element001  label="Ga_element : 1"  # scripted group (container) (typed FeaturePython)
  n = 1
  ref = Ga_element
FEATURE [App::DocumentObjectGroupPython] As_element001  label="As_element : 1"  # scripted group (container) (typed FeaturePython)
  n = 1
  ref = As_element
FEATURE [App::DocumentObjectGroupPython] G4_GALLIUM_ARSENIDE  # scripted group (container) (typed FeaturePython)
  Dunit = g/cm3
  Dvalue = 5.31
  Group = -> [Ga_element001,As_element001]
  conduct = 2
  density = 1
  expand = 3
  formula = G4_GALLIUM_ARSENIDE
  name = G4_GALLIUM_ARSENIDE
  specific = 4
FEATURE [App::DocumentObjectGroupPython] H_element041  label="H_element : 0.081"  # scripted group (container) (typed FeaturePython)
  n = 0.08118
FEATURE [App::DocumentObjectGroupPython] C_element048  label="C_element : 0.416"  # scripted group (container) (typed FeaturePython)
  n = 0.41606
FEATURE [App::DocumentObjectGroupPython] N_element018  label="N_element : 0.111"  # scripted group (container) (typed FeaturePython)
  n = 0.11124
FEATURE [App::DocumentObjectGroupPython] O_element042  label="O_element : 0.381"  # scripted group (container) (typed FeaturePython)
  n = 0.38064
FEATURE [App::DocumentObjectGroupPython] S_element013  label="S_element : 0.011"  # scripted group (container) (typed FeaturePython)
  n = 0.01088
FEATURE [App::DocumentObjectGroupPython] G4_GEL_PHOTO_EMULSION  # scripted group (container) (typed FeaturePython)
  Dunit = g/cm3
  Dvalue = 1.2914
  Group = -> [H_element041,C_element048,N_element018,O_element042,S_element013]
  conduct = 2
  density = 1
  expand = 3
  formula = G4_GEL_PHOTO_EMULSION
  name = G4_GEL_PHOTO_EMULSION
  specific = 4
FEATURE [App::DocumentObjectGroupPython] B_element004  label="B_element : 0.040"  # scripted group (container) (typed FeaturePython)
  n = 0.0400639
FEATURE [App::DocumentObjectGroupPython] O_element043  label="O_element : 0.540"  # scripted group (container) (typed FeaturePython)
  n = 0.539561
FEATURE [App::DocumentObjectGroupPython] Na_element008  label="Na_element : 0.028"  # scripted group (container) (typed FeaturePython)
  n = 0.0281909
FEATURE [App::DocumentObjectGroupPython] Al_element003  label="Al_element : 0.012"  # scripted group (container) (typed FeaturePython)
  n = 0.011644
FEATURE [App::DocumentObjectGroupPython] Si_element003  label="Si_element : 0.377"  # scripted group (container) (typed FeaturePython)
  n = 0.377219
FEATURE [App::DocumentObjectGroupPython] K_element004  label="K_element : 0.014"  # scripted group (container) (typed FeaturePython)
  n = 0.00332099
FEATURE [App::DocumentObjectGroupPython] G4_Pyrex_Glass  # scripted group (container) (typed FeaturePython)
  Dunit = g/cm3
  Dvalue = 2.23
  Group = -> [B_element004,O_element043,Na_element008,Al_element003,Si_element003,K_element004]
  conduct = 2
  density = 1
  expand = 3
  formula = G4_Pyrex_Glass
  name = G4_Pyrex_Glass
  specific = 4
FEATURE [App::DocumentObjectGroupPython] O_element044  label="O_element : 0.156"  # scripted group (container) (typed FeaturePython)
  n = 0.156453
FEATURE [App::DocumentObjectGroupPython] Si_element004  label="Si_element : 0.081"  # scripted group (container) (typed FeaturePython)
  n = 0.080866
FEATURE [App::DocumentObjectGroupPython] Ti_element001  label="Ti_element : 0.008"  # scripted group (container) (typed FeaturePython)
  n = 0.008092
FEATURE [App::DocumentObjectGroupPython] As_element002  label="As_element : 0.003"  # scripted group (container) (typed FeaturePython)
  n = 0.002651
FEATURE [App::DocumentObjectGroupPython] Pb_element001  label="Pb_element : 0.752"  # scripted group (container) (typed FeaturePython)
  n = 0.751938
FEATURE [App::DocumentObjectGroupPython] G4_GLASS_LEAD  # scripted group (container) (typed FeaturePython)
  Dunit = g/cm3
  Dvalue = 6.22
  Group = -> [O_element044,Si_element004,Ti_element001,As_element002,Pb_element001]
  conduct = 2
  density = 1
  expand = 3
  formula = G4_GLASS_LEAD
  name = G4_GLASS_LEAD
  specific = 4
FEATURE [App::DocumentObjectGroupPython] O_element045  label="O_element : 0.460"  # scripted group (container) (typed FeaturePython)
  n = 0.4598
FEATURE [App::DocumentObjectGroupPython] Na_element009  label="Na_element : 0.096"  # scripted group (container) (typed FeaturePython)
  n = 0.0964411
FEATURE [App::DocumentObjectGroupPython] Si_element005  label="Si_element : 0.378"  # scripted group (container) (typed FeaturePython)
  n = 0.336553
FEATURE [App::DocumentObjectGroupPython] Ca_element011  label="Ca_element : 0.107"  # scripted group (container) (typed FeaturePython)
  n = 0.107205
FEATURE [App::DocumentObjectGroupPython] G4_GLASS_PLATE  # scripted group (container) (typed FeaturePython)
  Dunit = g/cm3
  Dvalue = 2.4
  Group = -> [O_element045,Na_element009,Si_element005,Ca_element011]
  conduct = 2
  density = 1
  expand = 3
  formula = G4_GLASS_PLATE
  name = G4_GLASS_PLATE
  specific = 4
FEATURE [App::DocumentObjectGroupPython] C_element049  label="C_element : 026"  # scripted group (container) (typed FeaturePython)
  n = 5
  ref = C_element
FEATURE [App::DocumentObjectGroupPython] H_element042  label="H_element : 021"  # scripted group (container) (typed FeaturePython)
  n = 10
  ref = H_element
FEATURE [App::DocumentObjectGroupPython] N_element019  label="N_element : 2"  # scripted group (container) (typed FeaturePython)
  n = 2
  ref = N_element
FEATURE [App::DocumentObjectGroupPython] O_element046  label="O_element : 022"  # scripted group (container) (typed FeaturePython)
  n = 3
  ref = O_element
FEATURE [App::DocumentObjectGroupPython] G4_GLUTAMINE  # scripted group (container) (typed FeaturePython)
  Dunit = g/cm3
  Dvalue = 1.46
  Group = -> [C_element049,H_element042,N_element019,O_element046]
  conduct = 2
  density = 1
  expand = 3
  formula = G4_GLUTAMINE
  name = G4_GLUTAMINE
  specific = 4
FEATURE [App::DocumentObjectGroupPython] C_element050  label="C_element : 027"  # scripted group (container) (typed FeaturePython)
  n = 3
  ref = C_element
FEATURE [App::DocumentObjectGroupPython] H_element043  label="H_element : 022"  # scripted group (container) (typed FeaturePython)
  n = 8
  ref = H_element
FEATURE [App::DocumentObjectGroupPython] O_element047  label="O_element : 023"  # scripted group (container) (typed FeaturePython)
  n = 3
  ref = O_element
FEATURE [App::DocumentObjectGroupPython] G4_GLYCEROL  # scripted group (container) (typed FeaturePython)
  Dunit = g/cm3
  Dvalue = 1.2613
  Group = -> [C_element050,H_element043,O_element047]
  conduct = 2
  density = 1
  expand = 3
  formula = G4_GLYCEROL
  name = G4_GLYCEROL
  specific = 4
FEATURE [App::DocumentObjectGroupPython] C_element051  label="C_element : 028"  # scripted group (container) (typed FeaturePython)
  n = 5
  ref = C_element
FEATURE [App::DocumentObjectGroupPython] H_element044  label="H_element : 023"  # scripted group (container) (typed FeaturePython)
  n = 5
  ref = H_element
FEATURE [App::DocumentObjectGroupPython] N_element020  label="N_element : 009"  # scripted group (container) (typed FeaturePython)
  n = 5
  ref = N_element
FEATURE [App::DocumentObjectGroupPython] O_element048  label="O_element : 024"  # scripted group (container) (typed FeaturePython)
  n = 1
  ref = O_element
FEATURE [App::DocumentObjectGroupPython] G4_GUANINE  # scripted group (container) (typed FeaturePython)
  Dunit = g/cm3
  Dvalue = 2.2
  Group = -> [C_element051,H_element044,N_element020,O_element048]
  conduct = 2
  density = 1
  expand = 3
  formula = G4_GUANINE
  name = G4_GUANINE
  specific = 4
FEATURE [App::DocumentObjectGroupPython] Ca_element012  label="Ca_element : 006"  # scripted group (container) (typed FeaturePython)
  n = 1
  ref = Ca_element
FEATURE [App::DocumentObjectGroupPython] S_element014  label="S_element : 005"  # scripted group (container) (typed FeaturePython)
  n = 1
  ref = S_element
FEATURE [App::DocumentObjectGroupPython] O_element049  label="O_element : 6"  # scripted group (container) (typed FeaturePython)
  n = 6
  ref = O_element
FEATURE [App::DocumentObjectGroupPython] H_element045  label="H_element : 024"  # scripted group (container) (typed FeaturePython)
  n = 4
  ref = H_element
FEATURE [App::DocumentObjectGroupPython] G4_GYPSUM  # scripted group (container) (typed FeaturePython)
  Dunit = g/cm3
  Dvalue = 2.32
  Group = -> [Ca_element012,S_element014,O_element049,H_element045]
  conduct = 2
  density = 1
  expand = 3
  formula = G4_GYPSUM
  name = G4_GYPSUM
  specific = 4
FEATURE [App::DocumentObjectGroupPython] C_element052  label="C_element : 7"  # scripted group (container) (typed FeaturePython)
  n = 7
  ref = C_element
FEATURE [App::DocumentObjectGroupPython] H_element046  label="H_element : 16"  # scripted group (container) (typed FeaturePython)
  n = 16
  ref = H_element
FEATURE [App::DocumentObjectGroupPython] G4_N_HEPTANE  label="G4_N-HEPTANE"  # scripted group (container) (typed FeaturePython)
  Dunit = g/cm3
  Dvalue = 0.68376
  Group = -> [C_element052,H_element046]
  conduct = 2
  density = 1
  expand = 3
  formula = G4_N-HEPTANE
  name = G4_N-HEPTANE
  specific = 4
FEATURE [App::DocumentObjectGroupPython] C_element053  label="C_element : 029"  # scripted group (container) (typed FeaturePython)
  n = 6
  ref = C_element
FEATURE [App::DocumentObjectGroupPython] H_element047  label="H_element : 14"  # scripted group (container) (typed FeaturePython)
  n = 14
  ref = H_element
FEATURE [App::DocumentObjectGroupPython] G4_N_HEXANE  label="G4_N-HEXANE"  # scripted group (container) (typed FeaturePython)
  Dunit = g/cm3
  Dvalue = 0.6603
  Group = -> [C_element053,H_element047]
  conduct = 2
  density = 1
  expand = 3
  formula = G4_N-HEXANE
  name = G4_N-HEXANE
  specific = 4
FEATURE [App::DocumentObjectGroupPython] C_element054  label="C_element : 22"  # scripted group (container) (typed FeaturePython)
  n = 22
  ref = C_element
FEATURE [App::DocumentObjectGroupPython] H_element048  label="H_element : 025"  # scripted group (container) (typed FeaturePython)
  n = 10
  ref = H_element
FEATURE [App::DocumentObjectGroupPython] N_element021  label="N_element : 010"  # scripted group (container) (typed FeaturePython)
  n = 2
  ref = N_element
FEATURE [App::DocumentObjectGroupPython] O_element050  label="O_element : 025"  # scripted group (container) (typed FeaturePython)
  n = 5
  ref = O_element
FEATURE [App::DocumentObjectGroupPython] G4_KAPTON  # scripted group (container) (typed FeaturePython)
  Dunit = g/cm3
  Dvalue = 1.42
  Group = -> [C_element054,H_element048,N_element021,O_element050]
  conduct = 2
  density = 1
  expand = 3
  formula = G4_KAPTON
  name = G4_KAPTON
  specific = 4
FEATURE [App::DocumentObjectGroupPython] La_element001  label="La_element : 1"  # scripted group (container) (typed FeaturePython)
  n = 1
  ref = La_element
FEATURE [App::DocumentObjectGroupPython] Br_element003  label="Br_element : 002"  # scripted group (container) (typed FeaturePython)
  n = 1
  ref = Br_element
FEATURE [App::DocumentObjectGroupPython] O_element051  label="O_element : 026"  # scripted group (container) (typed FeaturePython)
  n = 1
  ref = O_element
FEATURE [App::DocumentObjectGroupPython] G4_LANTHANUM_OXYBROMIDE  # scripted group (container) (typed FeaturePython)
  Dunit = g/cm3
  Dvalue = 6.28
  Group = -> [La_element001,Br_element003,O_element051]
  conduct = 2
  density = 1
  expand = 3
  formula = G4_LANTHANUM_OXYBROMIDE
  name = G4_LANTHANUM_OXYBROMIDE
  specific = 4
FEATURE [App::DocumentObjectGroupPython] La_element002  label="La_element : 2"  # scripted group (container) (typed FeaturePython)
  n = 2
  ref = La_element
FEATURE [App::DocumentObjectGroupPython] O_element052  label="O_element : 027"  # scripted group (container) (typed FeaturePython)
  n = 2
  ref = O_element
FEATURE [App::DocumentObjectGroupPython] S_element015  label="S_element : 006"  # scripted group (container) (typed FeaturePython)
  n = 1
  ref = S_element
FEATURE [App::DocumentObjectGroupPython] G4_LANTHANUM_OXYSULFIDE  # scripted group (container) (typed FeaturePython)
  Dunit = g/cm3
  Dvalue = 5.86
  Group = -> [La_element002,O_element052,S_element015]
  conduct = 2
  density = 1
  expand = 3
  formula = G4_LANTHANUM_OXYSULFIDE
  name = G4_LANTHANUM_OXYSULFIDE
  specific = 4
FEATURE [App::DocumentObjectGroupPython] O_element053  label="O_element : 0.072"  # scripted group (container) (typed FeaturePython)
  n = 0.071682
FEATURE [App::DocumentObjectGroupPython] Pb_element002  label="Pb_element : 0.928"  # scripted group (container) (typed FeaturePython)
  n = 0.928318
FEATURE [App::DocumentObjectGroupPython] G4_LEAD_OXIDE  # scripted group (container) (typed FeaturePython)
  Dunit = g/cm3
  Dvalue = 9.53
  Group = -> [O_element053,Pb_element002]
  conduct = 2
  density = 1
  expand = 3
  formula = G4_LEAD_OXIDE
  name = G4_LEAD_OXIDE
  specific = 4
FEATURE [App::DocumentObjectGroupPython] Li_element001  label="Li_element : 1"  # scripted group (container) (typed FeaturePython)
  n = 1
  ref = Li_element
FEATURE [App::DocumentObjectGroupPython] N_element022  label="N_element : 011"  # scripted group (container) (typed FeaturePython)
  n = 1
  ref = N_element
FEATURE [App::DocumentObjectGroupPython] H_element049  label="H_element : 026"  # scripted group (container) (typed FeaturePython)
  n = 2
  ref = H_element
FEATURE [App::DocumentObjectGroupPython] G4_LITHIUM_AMIDE  # scripted group (container) (typed FeaturePython)
  Dunit = g/cm3
  Dvalue = 1.178
  Group = -> [Li_element001,N_element022,H_element049]
  conduct = 2
  density = 1
  expand = 3
  formula = G4_LITHIUM_AMIDE
  name = G4_LITHIUM_AMIDE
  specific = 4
FEATURE [App::DocumentObjectGroupPython] Li_element002  label="Li_element : 2"  # scripted group (container) (typed FeaturePython)
  n = 2
  ref = Li_element
FEATURE [App::DocumentObjectGroupPython] C_element055  label="C_element : 030"  # scripted group (container) (typed FeaturePython)
  n = 1
  ref = C_element
FEATURE [App::DocumentObjectGroupPython] O_element054  label="O_element : 028"  # scripted group (container) (typed FeaturePython)
  n = 3
  ref = O_element
FEATURE [App::DocumentObjectGroupPython] G4_LITHIUM_CARBONATE  # scripted group (container) (typed FeaturePython)
  Dunit = g/cm3
  Dvalue = 2.11
  Group = -> [Li_element002,C_element055,O_element054]
  conduct = 2
  density = 1
  expand = 3
  formula = G4_LITHIUM_CARBONATE
  name = G4_LITHIUM_CARBONATE
  specific = 4
FEATURE [App::DocumentObjectGroupPython] Li_element003  label="Li_element : 003"  # scripted group (container) (typed FeaturePython)
  n = 1
  ref = Li_element
FEATURE [App::DocumentObjectGroupPython] F_element012  label="F_element : 004"  # scripted group (container) (typed FeaturePython)
  n = 1
  ref = F_element
FEATURE [App::DocumentObjectGroupPython] G4_LITHIUM_FLUORIDE  # scripted group (container) (typed FeaturePython)
  Dunit = g/cm3
  Dvalue = 2.635
  Group = -> [Li_element003,F_element012]
  conduct = 2
  density = 1
  expand = 3
  formula = G4_LITHIUM_FLUORIDE
  name = G4_LITHIUM_FLUORIDE
  specific = 4
FEATURE [App::DocumentObjectGroupPython] Li_element004  label="Li_element : 004"  # scripted group (container) (typed FeaturePython)
  n = 1
  ref = Li_element
FEATURE [App::DocumentObjectGroupPython] H_element050  label="H_element : 027"  # scripted group (container) (typed FeaturePython)
  n = 1
  ref = H_element
FEATURE [App::DocumentObjectGroupPython] G4_LITHIUM_HYDRIDE  # scripted group (container) (typed FeaturePython)
  Dunit = g/cm3
  Dvalue = 0.82
  Group = -> [Li_element004,H_element050]
  conduct = 2
  density = 1
  expand = 3
  formula = G4_LITHIUM_HYDRIDE
  name = G4_LITHIUM_HYDRIDE
  specific = 4
FEATURE [App::DocumentObjectGroupPython] Li_element005  label="Li_element : 005"  # scripted group (container) (typed FeaturePython)
  n = 1
  ref = Li_element
FEATURE [App::DocumentObjectGroupPython] I_element003  label="I_element : 002"  # scripted group (container) (typed FeaturePython)
  n = 1
  ref = I_element
FEATURE [App::DocumentObjectGroupPython] G4_LITHIUM_IODIDE  # scripted group (container) (typed FeaturePython)
  Dunit = g/cm3
  Dvalue = 3.494
  Group = -> [Li_element005,I_element003]
  conduct = 2
  density = 1
  expand = 3
  formula = G4_LITHIUM_IODIDE
  name = G4_LITHIUM_IODIDE
  specific = 4
FEATURE [App::DocumentObjectGroupPython] Li_element006  label="Li_element : 006"  # scripted group (container) (typed FeaturePython)
  n = 2
  ref = Li_element
FEATURE [App::DocumentObjectGroupPython] O_element055  label="O_element : 029"  # scripted group (container) (typed FeaturePython)
  n = 1
  ref = O_element
FEATURE [App::DocumentObjectGroupPython] G4_LITHIUM_OXIDE  # scripted group (container) (typed FeaturePython)
  Dunit = g/cm3
  Dvalue = 2.013
  Group = -> [Li_element006,O_element055]
  conduct = 2
  density = 1
  expand = 3
  formula = G4_LITHIUM_OXIDE
  name = G4_LITHIUM_OXIDE
  specific = 4
FEATURE [App::DocumentObjectGroupPython] Li_element007  label="Li_element : 007"  # scripted group (container) (typed FeaturePython)
  n = 2
  ref = Li_element
FEATURE [App::DocumentObjectGroupPython] B_element005  label="B_element : 005"  # scripted group (container) (typed FeaturePython)
  n = 4
  ref = B_element
FEATURE [App::DocumentObjectGroupPython] O_element056  label="O_element : 7"  # scripted group (container) (typed FeaturePython)
  n = 7
  ref = O_element
FEATURE [App::DocumentObjectGroupPython] G4_LITHIUM_TETRABORATE  # scripted group (container) (typed FeaturePython)
  Dunit = g/cm3
  Dvalue = 2.44
  Group = -> [Li_element007,B_element005,O_element056]
  conduct = 2
  density = 1
  expand = 3
  formula = G4_LITHIUM_TETRABORATE
  name = G4_LITHIUM_TETRABORATE
  specific = 4
FEATURE [App::DocumentObjectGroupPython] H_element051  label="H_element : 0.105"  # scripted group (container) (typed FeaturePython)
  n = 0.105
FEATURE [App::DocumentObjectGroupPython] C_element056  label="C_element : 0.083"  # scripted group (container) (typed FeaturePython)
  n = 0.083
FEATURE [App::DocumentObjectGroupPython] N_element023  label="N_element : 0.023"  # scripted group (container) (typed FeaturePython)
  n = 0.023
FEATURE [App::DocumentObjectGroupPython] O_element057  label="O_element : 0.779"  # scripted group (container) (typed FeaturePython)
  n = 0.779
FEATURE [App::DocumentObjectGroupPython] Na_element010  label="Na_element : 0.097"  # scripted group (container) (typed FeaturePython)
  n = 0.002
FEATURE [App::DocumentObjectGroupPython] P_element006  label="P_element : 0.105"  # scripted group (container) (typed FeaturePython)
  n = 0.001
FEATURE [App::DocumentObjectGroupPython] S_element016  label="S_element : 0.017"  # scripted group (container) (typed FeaturePython)
  n = 0.002
FEATURE [App::DocumentObjectGroupPython] Cl_element014  label="Cl_element : 0.587"  # scripted group (container) (typed FeaturePython)
  n = 0.003
FEATURE [App::DocumentObjectGroupPython] K_element005  label="K_element : 0.015"  # scripted group (container) (typed FeaturePython)
  n = 0.002
FEATURE [App::DocumentObjectGroupPython] G4_LUNG_ICRP  # scripted group (container) (typed FeaturePython)
  Dunit = g/cm3
  Dvalue = 1.04
  Group = -> [H_element051,C_element056,N_element023,O_element057,Na_element010,P_element006,S_element016,Cl_element014,K_element005]
  conduct = 2
  density = 1
  expand = 3
  formula = G4_LUNG_ICRP
  name = G4_LUNG_ICRP
  specific = 4
FEATURE [App::DocumentObjectGroupPython] H_element052  label="H_element : 0.116"  # scripted group (container) (typed FeaturePython)
  n = 0.114318
FEATURE [App::DocumentObjectGroupPython] C_element057  label="C_element : 0.656"  # scripted group (container) (typed FeaturePython)
  n = 0.655824
FEATURE [App::DocumentObjectGroupPython] O_element058  label="O_element : 0.092"  # scripted group (container) (typed FeaturePython)
  n = 0.0921831
FEATURE [App::DocumentObjectGroupPython] Mg_element004  label="Mg_element : 0.135"  # scripted group (container) (typed FeaturePython)
  n = 0.134792
FEATURE [App::DocumentObjectGroupPython] Ca_element013  label="Ca_element : 0.003"  # scripted group (container) (typed FeaturePython)
  n = 0.002883
FEATURE [App::DocumentObjectGroupPython] G4_M3_WAX  # scripted group (container) (typed FeaturePython)
  Dunit = g/cm3
  Dvalue = 1.05
  Group = -> [H_element052,C_element057,O_element058,Mg_element004,Ca_element013]
  conduct = 2
  density = 1
  expand = 3
  formula = G4_M3_WAX
  name = G4_M3_WAX
  specific = 4
FEATURE [App::DocumentObjectGroupPython] Mg_element005  label="Mg_element : 1"  # scripted group (container) (typed FeaturePython)
  n = 1
  ref = Mg_element
FEATURE [App::DocumentObjectGroupPython] C_element058  label="C_element : 031"  # scripted group (container) (typed FeaturePython)
  n = 1
  ref = C_element
FEATURE [App::DocumentObjectGroupPython] O_element059  label="O_element : 030"  # scripted group (container) (typed FeaturePython)
  n = 3
  ref = O_element
FEATURE [App::DocumentObjectGroupPython] G4_MAGNESIUM_CARBONATE  # scripted group (container) (typed FeaturePython)
  Dunit = g/cm3
  Dvalue = 2.958
  Group = -> [Mg_element005,C_element058,O_element059]
  conduct = 2
  density = 1
  expand = 3
  formula = G4_MAGNESIUM_CARBONATE
  name = G4_MAGNESIUM_CARBONATE
  specific = 4
FEATURE [App::DocumentObjectGroupPython] Mg_element006  label="Mg_element : 002"  # scripted group (container) (typed FeaturePython)
  n = 1
  ref = Mg_element
FEATURE [App::DocumentObjectGroupPython] F_element013  label="F_element : 005"  # scripted group (container) (typed FeaturePython)
  n = 2
  ref = F_element
FEATURE [App::DocumentObjectGroupPython] G4_MAGNESIUM_FLUORIDE  # scripted group (container) (typed FeaturePython)
  Dunit = g/cm3
  Dvalue = 3
  Group = -> [Mg_element006,F_element013]
  conduct = 2
  density = 1
  expand = 3
  formula = G4_MAGNESIUM_FLUORIDE
  name = G4_MAGNESIUM_FLUORIDE
  specific = 4
FEATURE [App::DocumentObjectGroupPython] Mg_element007  label="Mg_element : 003"  # scripted group (container) (typed FeaturePython)
  n = 1
  ref = Mg_element
FEATURE [App::DocumentObjectGroupPython] O_element060  label="O_element : 031"  # scripted group (container) (typed FeaturePython)
  n = 1
  ref = O_element
FEATURE [App::DocumentObjectGroupPython] G4_MAGNESIUM_OXIDE  # scripted group (container) (typed FeaturePython)
  Dunit = g/cm3
  Dvalue = 3.58
  Group = -> [Mg_element007,O_element060]
  conduct = 2
  density = 1
  expand = 3
  formula = G4_MAGNESIUM_OXIDE
  name = G4_MAGNESIUM_OXIDE
  specific = 4
FEATURE [App::DocumentObjectGroupPython] Mg_element008  label="Mg_element : 004"  # scripted group (container) (typed FeaturePython)
  n = 1
  ref = Mg_element
FEATURE [App::DocumentObjectGroupPython] B_element006  label="B_element : 006"  # scripted group (container) (typed FeaturePython)
  n = 4
  ref = B_element
FEATURE [App::DocumentObjectGroupPython] O_element061  label="O_element : 032"  # scripted group (container) (typed FeaturePython)
  n = 7
  ref = O_element
FEATURE [App::DocumentObjectGroupPython] G4_MAGNESIUM_TETRABORATE  # scripted group (container) (typed FeaturePython)
  Dunit = g/cm3
  Dvalue = 2.53
  Group = -> [Mg_element008,B_element006,O_element061]
  conduct = 2
  density = 1
  expand = 3
  formula = G4_MAGNESIUM_TETRABORATE
  name = G4_MAGNESIUM_TETRABORATE
  specific = 4
FEATURE [App::DocumentObjectGroupPython] Hg_element001  label="Hg_element : 1"  # scripted group (container) (typed FeaturePython)
  n = 1
  ref = Hg_element
FEATURE [App::DocumentObjectGroupPython] I_element004  label="I_element : 2"  # scripted group (container) (typed FeaturePython)
  n = 2
  ref = I_element
FEATURE [App::DocumentObjectGroupPython] G4_MERCURIC_IODIDE  # scripted group (container) (typed FeaturePython)
  Dunit = g/cm3
  Dvalue = 6.36
  Group = -> [Hg_element001,I_element004]
  conduct = 2
  density = 1
  expand = 3
  formula = G4_MERCURIC_IODIDE
  name = G4_MERCURIC_IODIDE
  specific = 4
FEATURE [App::DocumentObjectGroupPython] C_element059  label="C_element : 032"  # scripted group (container) (typed FeaturePython)
  n = 1
  ref = C_element
FEATURE [App::DocumentObjectGroupPython] H_element053  label="H_element : 028"  # scripted group (container) (typed FeaturePython)
  n = 4
  ref = H_element
FEATURE [App::DocumentObjectGroupPython] G4_METHANE  # scripted group (container) (typed FeaturePython)
  Dunit = g/cm3
  Dvalue = 0.000667151
  Group = -> [C_element059,H_element053]
  conduct = 2
  density = 1
  expand = 3
  formula = G4_METHANE
  name = G4_METHANE
  specific = 4
FEATURE [App::DocumentObjectGroupPython] C_element060  label="C_element : 033"  # scripted group (container) (typed FeaturePython)
  n = 1
  ref = C_element
FEATURE [App::DocumentObjectGroupPython] H_element054  label="H_element : 029"  # scripted group (container) (typed FeaturePython)
  n = 4
  ref = H_element
FEATURE [App::DocumentObjectGroupPython] O_element062  label="O_element : 033"  # scripted group (container) (typed FeaturePython)
  n = 1
  ref = O_element
FEATURE [App::DocumentObjectGroupPython] G4_METHANOL  # scripted group (container) (typed FeaturePython)
  Dunit = g/cm3
  Dvalue = 0.7914
  Group = -> [C_element060,H_element054,O_element062]
  conduct = 2
  density = 1
  expand = 3
  formula = G4_METHANOL
  name = G4_METHANOL
  specific = 4
FEATURE [App::DocumentObjectGroupPython] H_element055  label="H_element : 0.134"  # scripted group (container) (typed FeaturePython)
  n = 0.13404
FEATURE [App::DocumentObjectGroupPython] C_element061  label="C_element : 0.778"  # scripted group (container) (typed FeaturePython)
  n = 0.77796
FEATURE [App::DocumentObjectGroupPython] O_element063  label="O_element : 0.035"  # scripted group (container) (typed FeaturePython)
  n = 0.03502
FEATURE [App::DocumentObjectGroupPython] Mg_element009  label="Mg_element : 0.039"  # scripted group (container) (typed FeaturePython)
  n = 0.038594
FEATURE [App::DocumentObjectGroupPython] Ti_element002  label="Ti_element : 0.014"  # scripted group (container) (typed FeaturePython)
  n = 0.014386
FEATURE [App::DocumentObjectGroupPython] G4_MIX_D_WAX  # scripted group (container) (typed FeaturePython)
  Dunit = g/cm3
  Dvalue = 0.99
  Group = -> [H_element055,C_element061,O_element063,Mg_element009,Ti_element002]
  conduct = 2
  density = 1
  expand = 3
  formula = G4_MIX_D_WAX
  name = G4_MIX_D_WAX
  specific = 4
FEATURE [App::DocumentObjectGroupPython] H_element056  label="H_element : 0.135"  # scripted group (container) (typed FeaturePython)
  n = 0.081192
FEATURE [App::DocumentObjectGroupPython] C_element062  label="C_element : 0.583"  # scripted group (container) (typed FeaturePython)
  n = 0.583442
FEATURE [App::DocumentObjectGroupPython] N_element024  label="N_element : 0.018"  # scripted group (container) (typed FeaturePython)
  n = 0.017798
FEATURE [App::DocumentObjectGroupPython] O_element064  label="O_element : 0.186"  # scripted group (container) (typed FeaturePython)
  n = 0.186381
FEATURE [App::DocumentObjectGroupPython] Mg_element010  label="Mg_element : 0.130"  # scripted group (container) (typed FeaturePython)
  n = 0.130287
FEATURE [App::DocumentObjectGroupPython] Cl_element015  label="Cl_element : 0.588"  # scripted group (container) (typed FeaturePython)
  n = 0.0009
FEATURE [App::DocumentObjectGroupPython] G4_MS20_TISSUE  # scripted group (container) (typed FeaturePython)
  Dunit = g/cm3
  Dvalue = 1
  Group = -> [H_element056,C_element062,N_element024,O_element064,Mg_element010,Cl_element015]
  conduct = 2
  density = 1
  expand = 3
  formula = G4_MS20_TISSUE
  name = G4_MS20_TISSUE
  specific = 4
FEATURE [App::DocumentObjectGroupPython] H_element057  label="H_element : 0.136"  # scripted group (container) (typed FeaturePython)
  n = 0.102
FEATURE [App::DocumentObjectGroupPython] C_element063  label="C_element : 0.143"  # scripted group (container) (typed FeaturePython)
  n = 0.143
FEATURE [App::DocumentObjectGroupPython] N_element025  label="N_element : 0.034"  # scripted group (container) (typed FeaturePython)
  n = 0.034
FEATURE [App::DocumentObjectGroupPython] O_element065  label="O_element : 0.710"  # scripted group (container) (typed FeaturePython)
  n = 0.71
FEATURE [App::DocumentObjectGroupPython] Na_element011  label="Na_element : 0.098"  # scripted group (container) (typed FeaturePython)
  n = 0.001
FEATURE [App::DocumentObjectGroupPython] P_element007  label="P_element : 0.002"  # scripted group (container) (typed FeaturePython)
  n = 0.002
FEATURE [App::DocumentObjectGroupPython] S_element017  label="S_element : 0.018"  # scripted group (container) (typed FeaturePython)
  n = 0.003
FEATURE [App::DocumentObjectGroupPython] Cl_element016  label="Cl_element : 0.589"  # scripted group (container) (typed FeaturePython)
  n = 0.001
FEATURE [App::DocumentObjectGroupPython] K_element006  label="K_element : 0.004"  # scripted group (container) (typed FeaturePython)
  n = 0.004
FEATURE [App::DocumentObjectGroupPython] G4_MUSCLE_SKELETAL_ICRP  # scripted group (container) (typed FeaturePython)
  Dunit = g/cm3
  Dvalue = 1.05
  Group = -> [H_element057,C_element063,N_element025,O_element065,Na_element011,P_element007,S_element017,Cl_element016,K_element006]
  conduct = 2
  density = 1
  expand = 3
  formula = G4_MUSCLE_SKELETAL_ICRP
  name = G4_MUSCLE_SKELETAL_ICRP
  specific = 4
FEATURE [App::DocumentObjectGroupPython] H_element058  label="H_element : 0.137"  # scripted group (container) (typed FeaturePython)
  n = 0.102102
FEATURE [App::DocumentObjectGroupPython] C_element064  label="C_element : 0.123"  # scripted group (container) (typed FeaturePython)
  n = 0.123123
FEATURE [App::DocumentObjectGroupPython] N_element026  label="N_element : 0.756"  # scripted group (container) (typed FeaturePython)
  n = 0.035035
FEATURE [App::DocumentObjectGroupPython] O_element066  label="O_element : 0.730"  # scripted group (container) (typed FeaturePython)
  n = 0.72973
FEATURE [App::DocumentObjectGroupPython] Na_element012  label="Na_element : 0.099"  # scripted group (container) (typed FeaturePython)
  n = 0.001001
FEATURE [App::DocumentObjectGroupPython] P_element008  label="P_element : 0.106"  # scripted group (container) (typed FeaturePython)
  n = 0.002002
FEATURE [App::DocumentObjectGroupPython] S_element018  label="S_element : 0.019"  # scripted group (container) (typed FeaturePython)
  n = 0.004004
FEATURE [App::DocumentObjectGroupPython] K_element007  label="K_element : 0.016"  # scripted group (container) (typed FeaturePython)
  n = 0.003003
FEATURE [App::DocumentObjectGroupPython] G4_MUSCLE_STRIATED_ICRU  # scripted group (container) (typed FeaturePython)
  Dunit = g/cm3
  Dvalue = 1.04
  Group = -> [H_element058,C_element064,N_element026,O_element066,Na_element012,P_element008,S_element018,K_element007]
  conduct = 2
  density = 1
  expand = 3
  formula = G4_MUSCLE_STRIATED_ICRU
  name = G4_MUSCLE_STRIATED_ICRU
  specific = 4
FEATURE [App::DocumentObjectGroupPython] H_element059  label="H_element : 0.098"  # scripted group (container) (typed FeaturePython)
  n = 0.0982341
FEATURE [App::DocumentObjectGroupPython] C_element065  label="C_element : 0.156"  # scripted group (container) (typed FeaturePython)
  n = 0.156214
FEATURE [App::DocumentObjectGroupPython] N_element027  label="N_element : 0.757"  # scripted group (container) (typed FeaturePython)
  n = 0.035451
FEATURE [App::DocumentObjectGroupPython] O_element067  label="O_element : 0.880"  # scripted group (container) (typed FeaturePython)
  n = 0.710101
FEATURE [App::DocumentObjectGroupPython] G4_MUSCLE_WITH_SUCROSE  # scripted group (container) (typed FeaturePython)
  Dunit = g/cm3
  Dvalue = 1.11
  Group = -> [H_element059,C_element065,N_element027,O_element067]
  conduct = 2
  density = 1
  expand = 3
  formula = G4_MUSCLE_WITH_SUCROSE
  name = G4_MUSCLE_WITH_SUCROSE
  specific = 4
FEATURE [App::DocumentObjectGroupPython] H_element060  label="H_element : 0.138"  # scripted group (container) (typed FeaturePython)
  n = 0.101969
FEATURE [App::DocumentObjectGroupPython] C_element066  label="C_element : 0.120"  # scripted group (container) (typed FeaturePython)
  n = 0.120058
FEATURE [App::DocumentObjectGroupPython] N_element028  label="N_element : 0.758"  # scripted group (container) (typed FeaturePython)
  n = 0.035451
FEATURE [App::DocumentObjectGroupPython] O_element068  label="O_element : 0.743"  # scripted group (container) (typed FeaturePython)
  n = 0.742522
FEATURE [App::DocumentObjectGroupPython] G4_MUSCLE_WITHOUT_SUCROSE  # scripted group (container) (typed FeaturePython)
  Dunit = g/cm3
  Dvalue = 1.07
  Group = -> [H_element060,C_element066,N_element028,O_element068]
  conduct = 2
  density = 1
  expand = 3
  formula = G4_MUSCLE_WITHOUT_SUCROSE
  name = G4_MUSCLE_WITHOUT_SUCROSE
  specific = 4
FEATURE [App::DocumentObjectGroupPython] C_element067  label="C_element : 10"  # scripted group (container) (typed FeaturePython)
  n = 10
  ref = C_element
FEATURE [App::DocumentObjectGroupPython] H_element061  label="H_element : 030"  # scripted group (container) (typed FeaturePython)
  n = 8
  ref = H_element
FEATURE [App::DocumentObjectGroupPython] G4_NAPHTHALENE  # scripted group (container) (typed FeaturePython)
  Dunit = g/cm3
  Dvalue = 1.145
  Group = -> [C_element067,H_element061]
  conduct = 2
  density = 1
  expand = 3
  formula = G4_NAPHTHALENE
  name = G4_NAPHTHALENE
  specific = 4
FEATURE [App::DocumentObjectGroupPython] C_element068  label="C_element : 034"  # scripted group (container) (typed FeaturePython)
  n = 6
  ref = C_element
FEATURE [App::DocumentObjectGroupPython] H_element062  label="H_element : 031"  # scripted group (container) (typed FeaturePython)
  n = 5
  ref = H_element
FEATURE [App::DocumentObjectGroupPython] N_element029  label="N_element : 012"  # scripted group (container) (typed FeaturePython)
  n = 1
  ref = N_element
FEATURE [App::DocumentObjectGroupPython] O_element069  label="O_element : 034"  # scripted group (container) (typed FeaturePython)
  n = 2
  ref = O_element
FEATURE [App::DocumentObjectGroupPython] G4_NITROBENZENE  # scripted group (container) (typed FeaturePython)
  Dunit = g/cm3
  Dvalue = 1.19867
  Group = -> [C_element068,H_element062,N_element029,O_element069]
  conduct = 2
  density = 1
  expand = 3
  formula = G4_NITROBENZENE
  name = G4_NITROBENZENE
  specific = 4
FEATURE [App::DocumentObjectGroupPython] N_element030  label="N_element : 013"  # scripted group (container) (typed FeaturePython)
  n = 2
  ref = N_element
FEATURE [App::DocumentObjectGroupPython] O_element070  label="O_element : 035"  # scripted group (container) (typed FeaturePython)
  n = 1
  ref = O_element
FEATURE [App::DocumentObjectGroupPython] G4_NITROUS_OXIDE  # scripted group (container) (typed FeaturePython)
  Dunit = g/cm3
  Dvalue = 0.00183094
  Group = -> [N_element030,O_element070]
  conduct = 2
  density = 1
  expand = 3
  formula = G4_NITROUS_OXIDE
  name = G4_NITROUS_OXIDE
  specific = 4
FEATURE [App::DocumentObjectGroupPython] H_element063  label="H_element : 0.104"  # scripted group (container) (typed FeaturePython)
  n = 0.103509
FEATURE [App::DocumentObjectGroupPython] C_element069  label="C_element : 0.648"  # scripted group (container) (typed FeaturePython)
  n = 0.648416
FEATURE [App::DocumentObjectGroupPython] N_element031  label="N_element : 0.100"  # scripted group (container) (typed FeaturePython)
  n = 0.0995361
FEATURE [App::DocumentObjectGroupPython] O_element071  label="O_element : 0.149"  # scripted group (container) (typed FeaturePython)
  n = 0.148539
FEATURE [App::DocumentObjectGroupPython] G4_NYLON_8062  label="G4_NYLON-8062"  # scripted group (container) (typed FeaturePython)
  Dunit = g/cm3
  Dvalue = 1.08
  Group = -> [H_element063,C_element069,N_element031,O_element071]
  conduct = 2
  density = 1
  expand = 3
  formula = G4_NYLON-8062
  name = G4_NYLON-8062
  specific = 4
FEATURE [App::DocumentObjectGroupPython] C_element070  label="C_element : 035"  # scripted group (container) (typed FeaturePython)
  n = 6
  ref = C_element
FEATURE [App::DocumentObjectGroupPython] H_element064  label="H_element : 11"  # scripted group (container) (typed FeaturePython)
  n = 11
  ref = H_element
FEATURE [App::DocumentObjectGroupPython] N_element032  label="N_element : 014"  # scripted group (container) (typed FeaturePython)
  n = 1
  ref = N_element
FEATURE [App::DocumentObjectGroupPython] O_element072  label="O_element : 036"  # scripted group (container) (typed FeaturePython)
  n = 1
  ref = O_element
FEATURE [App::DocumentObjectGroupPython] G4_NYLON_6_6  label="G4_NYLON-6-6"  # scripted group (container) (typed FeaturePython)
  Dunit = g/cm3
  Dvalue = 1.14
  Group = -> [C_element070,H_element064,N_element032,O_element072]
  conduct = 2
  density = 1
  expand = 3
  formula = G4_NYLON-6-6
  name = G4_NYLON-6-6
  specific = 4
FEATURE [App::DocumentObjectGroupPython] H_element065  label="H_element : 0.139"  # scripted group (container) (typed FeaturePython)
  n = 0.107062
FEATURE [App::DocumentObjectGroupPython] C_element071  label="C_element : 0.680"  # scripted group (container) (typed FeaturePython)
  n = 0.680449
FEATURE [App::DocumentObjectGroupPython] N_element033  label="N_element : 0.099"  # scripted group (container) (typed FeaturePython)
  n = 0.099189
FEATURE [App::DocumentObjectGroupPython] O_element073  label="O_element : 0.113"  # scripted group (container) (typed FeaturePython)
  n = 0.1133
FEATURE [App::DocumentObjectGroupPython] G4_NYLON_6_10  label="G4_NYLON-6-10"  # scripted group (container) (typed FeaturePython)
  Dunit = g/cm3
  Dvalue = 1.14
  Group = -> [H_element065,C_element071,N_element033,O_element073]
  conduct = 2
  density = 1
  expand = 3
  formula = G4_NYLON-6-10
  name = G4_NYLON-6-10
  specific = 4
FEATURE [App::DocumentObjectGroupPython] H_element066  label="H_element : 0.140"  # scripted group (container) (typed FeaturePython)
  n = 0.115476
FEATURE [App::DocumentObjectGroupPython] C_element072  label="C_element : 0.721"  # scripted group (container) (typed FeaturePython)
  n = 0.720818
FEATURE [App::DocumentObjectGroupPython] N_element034  label="N_element : 0.076"  # scripted group (container) (typed FeaturePython)
  n = 0.0764169
FEATURE [App::DocumentObjectGroupPython] O_element074  label="O_element : 0.087"  # scripted group (container) (typed FeaturePython)
  n = 0.0872889
FEATURE [App::DocumentObjectGroupPython] G4_NYLON_11_RILSAN  label="G4_NYLON-11_RILSAN"  # scripted group (container) (typed FeaturePython)
  Dunit = g/cm3
  Dvalue = 1.425
  Group = -> [H_element066,C_element072,N_element034,O_element074]
  conduct = 2
  density = 1
  expand = 3
  formula = G4_NYLON-11_RILSAN
  name = G4_NYLON-11_RILSAN
  specific = 4
FEATURE [App::DocumentObjectGroupPython] C_element073  label="C_element : 8"  # scripted group (container) (typed FeaturePython)
  n = 8
  ref = C_element
FEATURE [App::DocumentObjectGroupPython] H_element067  label="H_element : 18"  # scripted group (container) (typed FeaturePython)
  n = 18
  ref = H_element
FEATURE [App::DocumentObjectGroupPython] G4_OCTANE  # scripted group (container) (typed FeaturePython)
  Dunit = g/cm3
  Dvalue = 0.7026
  Group = -> [C_element073,H_element067]
  conduct = 2
  density = 1
  expand = 3
  formula = G4_OCTANE
  name = G4_OCTANE
  specific = 4
FEATURE [App::DocumentObjectGroupPython] C_element074  label="C_element : 25"  # scripted group (container) (typed FeaturePython)
  n = 25
  ref = C_element
FEATURE [App::DocumentObjectGroupPython] H_element068  label="H_element : 52"  # scripted group (container) (typed FeaturePython)
  n = 52
  ref = H_element
FEATURE [App::DocumentObjectGroupPython] G4_PARAFFIN  # scripted group (container) (typed FeaturePython)
  Dunit = g/cm3
  Dvalue = 0.93
  Group = -> [C_element074,H_element068]
  conduct = 2
  density = 1
  expand = 3
  formula = G4_PARAFFIN
  name = G4_PARAFFIN
  specific = 4
FEATURE [App::DocumentObjectGroupPython] C_element075  label="C_element : 036"  # scripted group (container) (typed FeaturePython)
  n = 5
  ref = C_element
FEATURE [App::DocumentObjectGroupPython] H_element069  label="H_element : 032"  # scripted group (container) (typed FeaturePython)
  n = 12
  ref = H_element
FEATURE [App::DocumentObjectGroupPython] G4_N_PENTANE  label="G4_N-PENTANE"  # scripted group (container) (typed FeaturePython)
  Dunit = g/cm3
  Dvalue = 0.6262
  Group = -> [C_element075,H_element069]
  conduct = 2
  density = 1
  expand = 3
  formula = G4_N-PENTANE
  name = G4_N-PENTANE
  specific = 4
FEATURE [App::DocumentObjectGroupPython] H_element070  label="H_element : 0.014"  # scripted group (container) (typed FeaturePython)
  n = 0.0141
FEATURE [App::DocumentObjectGroupPython] C_element076  label="C_element : 0.072"  # scripted group (container) (typed FeaturePython)
  n = 0.072261
FEATURE [App::DocumentObjectGroupPython] N_element035  label="N_element : 0.019"  # scripted group (container) (typed FeaturePython)
  n = 0.01932
FEATURE [App::DocumentObjectGroupPython] O_element075  label="O_element : 0.066"  # scripted group (container) (typed FeaturePython)
  n = 0.066101
FEATURE [App::DocumentObjectGroupPython] S_element019  label="S_element : 0.020"  # scripted group (container) (typed FeaturePython)
  n = 0.00189
FEATURE [App::DocumentObjectGroupPython] Br_element004  label="Br_element : 0.349"  # scripted group (container) (typed FeaturePython)
  n = 0.349103
FEATURE [App::DocumentObjectGroupPython] Ag_element001  label="Ag_element : 0.474"  # scripted group (container) (typed FeaturePython)
  n = 0.474105
FEATURE [App::DocumentObjectGroupPython] I_element005  label="I_element : 0.003"  # scripted group (container) (typed FeaturePython)
  n = 0.00312
FEATURE [App::DocumentObjectGroupPython] G4_PHOTO_EMULSION  # scripted group (container) (typed FeaturePython)
  Dunit = g/cm3
  Dvalue = 3.815
  Group = -> [H_element070,C_element076,N_element035,O_element075,S_element019,Br_element004,Ag_element001,I_element005]
  conduct = 2
  density = 1
  expand = 3
  formula = G4_PHOTO_EMULSION
  name = G4_PHOTO_EMULSION
  specific = 4
FEATURE [App::DocumentObjectGroupPython] C_element077  label="C_element : 9"  # scripted group (container) (typed FeaturePython)
  n = 9
  ref = C_element
FEATURE [App::DocumentObjectGroupPython] H_element071  label="H_element : 033"  # scripted group (container) (typed FeaturePython)
  n = 10
  ref = H_element
FEATURE [App::DocumentObjectGroupPython] G4_PLASTIC_SC_VINYLTOLUENE  # scripted group (container) (typed FeaturePython)
  Dunit = g/cm3
  Dvalue = 1.032
  Group = -> [C_element077,H_element071]
  conduct = 2
  density = 1
  expand = 3
  formula = G4_PLASTIC_SC_VINYLTOLUENE
  name = G4_PLASTIC_SC_VINYLTOLUENE
  specific = 4
FEATURE [App::DocumentObjectGroupPython] Pu_element001  label="Pu_element : 1"  # scripted group (container) (typed FeaturePython)
  n = 1
  ref = Pu_element
FEATURE [App::DocumentObjectGroupPython] O_element076  label="O_element : 037"  # scripted group (container) (typed FeaturePython)
  n = 2
  ref = O_element
FEATURE [App::DocumentObjectGroupPython] G4_PLUTONIUM_DIOXIDE  # scripted group (container) (typed FeaturePython)
  Dunit = g/cm3
  Dvalue = 11.46
  Group = -> [Pu_element001,O_element076]
  conduct = 2
  density = 1
  expand = 3
  formula = G4_PLUTONIUM_DIOXIDE
  name = G4_PLUTONIUM_DIOXIDE
  specific = 4
FEATURE [App::DocumentObjectGroupPython] C_element078  label="C_element : 037"  # scripted group (container) (typed FeaturePython)
  n = 3
  ref = C_element
FEATURE [App::DocumentObjectGroupPython] H_element072  label="H_element : 034"  # scripted group (container) (typed FeaturePython)
  n = 3
  ref = H_element
FEATURE [App::DocumentObjectGroupPython] N_element036  label="N_element : 015"  # scripted group (container) (typed FeaturePython)
  n = 1
  ref = N_element
FEATURE [App::DocumentObjectGroupPython] G4_POLYACRYLONITRILE  # scripted group (container) (typed FeaturePython)
  Dunit = g/cm3
  Dvalue = 1.17
  Group = -> [C_element078,H_element072,N_element036]
  conduct = 2
  density = 1
  expand = 3
  formula = G4_POLYACRYLONITRILE
  name = G4_POLYACRYLONITRILE
  specific = 4
FEATURE [App::DocumentObjectGroupPython] C_element079  label="C_element : 16"  # scripted group (container) (typed FeaturePython)
  n = 16
  ref = C_element
FEATURE [App::DocumentObjectGroupPython] H_element073  label="H_element : 035"  # scripted group (container) (typed FeaturePython)
  n = 14
  ref = H_element
FEATURE [App::DocumentObjectGroupPython] O_element077  label="O_element : 038"  # scripted group (container) (typed FeaturePython)
  n = 3
  ref = O_element
FEATURE [App::DocumentObjectGroupPython] G4_POLYCARBONATE  # scripted group (container) (typed FeaturePython)
  Dunit = g/cm3
  Dvalue = 1.2
  Group = -> [C_element079,H_element073,O_element077]
  conduct = 2
  density = 1
  expand = 3
  formula = G4_POLYCARBONATE
  name = G4_POLYCARBONATE
  specific = 4
FEATURE [App::DocumentObjectGroupPython] C_element080  label="C_element : 038"  # scripted group (container) (typed FeaturePython)
  n = 8
  ref = C_element
FEATURE [App::DocumentObjectGroupPython] H_element074  label="H_element : 036"  # scripted group (container) (typed FeaturePython)
  n = 7
  ref = H_element
FEATURE [App::DocumentObjectGroupPython] Cl_element017  label="Cl_element : 007"  # scripted group (container) (typed FeaturePython)
  n = 1
  ref = Cl_element
FEATURE [App::DocumentObjectGroupPython] G4_POLYCHLOROSTYRENE  # scripted group (container) (typed FeaturePython)
  Dunit = g/cm3
  Dvalue = 1.3
  Group = -> [C_element080,H_element074,Cl_element017]
  conduct = 2
  density = 1
  expand = 3
  formula = G4_POLYCHLOROSTYRENE
  name = G4_POLYCHLOROSTYRENE
  specific = 4
FEATURE [App::DocumentObjectGroupPython] C_element081  label="C_element : 039"  # scripted group (container) (typed FeaturePython)
  n = 1
  ref = C_element
FEATURE [App::DocumentObjectGroupPython] H_element075  label="H_element : 037"  # scripted group (container) (typed FeaturePython)
  n = 2
  ref = H_element
FEATURE [App::DocumentObjectGroupPython] G4_POLYETHYLENE  # scripted group (container) (typed FeaturePython)
  Dunit = g/cm3
  Dvalue = 0.94
  Group = -> [C_element081,H_element075]
  conduct = 2
  density = 1
  expand = 3
  formula = G4_POLYETHYLENE
  name = G4_POLYETHYLENE
  specific = 4
FEATURE [App::DocumentObjectGroupPython] C_element082  label="C_element : 040"  # scripted group (container) (typed FeaturePython)
  n = 10
  ref = C_element
FEATURE [App::DocumentObjectGroupPython] H_element076  label="H_element : 038"  # scripted group (container) (typed FeaturePython)
  n = 8
  ref = H_element
FEATURE [App::DocumentObjectGroupPython] O_element078  label="O_element : 039"  # scripted group (container) (typed FeaturePython)
  n = 4
  ref = O_element
FEATURE [App::DocumentObjectGroupPython] G4_MYLAR  # scripted group (container) (typed FeaturePython)
  Dunit = g/cm3
  Dvalue = 1.4
  Group = -> [C_element082,H_element076,O_element078]
  conduct = 2
  density = 1
  expand = 3
  formula = G4_MYLAR
  name = G4_MYLAR
  specific = 4
FEATURE [App::DocumentObjectGroupPython] C_element083  label="C_element : 041"  # scripted group (container) (typed FeaturePython)
  n = 5
  ref = C_element
FEATURE [App::DocumentObjectGroupPython] H_element077  label="H_element : 039"  # scripted group (container) (typed FeaturePython)
  n = 8
  ref = H_element
FEATURE [App::DocumentObjectGroupPython] O_element079  label="O_element : 040"  # scripted group (container) (typed FeaturePython)
  n = 2
  ref = O_element
FEATURE [App::DocumentObjectGroupPython] G4_PLEXIGLASS  # scripted group (container) (typed FeaturePython)
  Dunit = g/cm3
  Dvalue = 1.19
  Group = -> [C_element083,H_element077,O_element079]
  conduct = 2
  density = 1
  expand = 3
  formula = G4_PLEXIGLASS
  name = G4_PLEXIGLASS
  specific = 4
FEATURE [App::DocumentObjectGroupPython] C_element084  label="C_element : 042"  # scripted group (container) (typed FeaturePython)
  n = 1
  ref = C_element
FEATURE [App::DocumentObjectGroupPython] H_element078  label="H_element : 040"  # scripted group (container) (typed FeaturePython)
  n = 2
  ref = H_element
FEATURE [App::DocumentObjectGroupPython] O_element080  label="O_element : 041"  # scripted group (container) (typed FeaturePython)
  n = 1
  ref = O_element
FEATURE [App::DocumentObjectGroupPython] G4_POLYOXYMETHYLENE  # scripted group (container) (typed FeaturePython)
  Dunit = g/cm3
  Dvalue = 1.425
  Group = -> [C_element084,H_element078,O_element080]
  conduct = 2
  density = 1
  expand = 3
  formula = G4_POLYOXYMETHYLENE
  name = G4_POLYOXYMETHYLENE
  specific = 4
FEATURE [App::DocumentObjectGroupPython] C_element085  label="C_element : 043"  # scripted group (container) (typed FeaturePython)
  n = 2
  ref = C_element
FEATURE [App::DocumentObjectGroupPython] H_element079  label="H_element : 041"  # scripted group (container) (typed FeaturePython)
  n = 4
  ref = H_element
FEATURE [App::DocumentObjectGroupPython] G4_POLYPROPYLENE  # scripted group (container) (typed FeaturePython)
  Dunit = g/cm3
  Dvalue = 0.9
  Group = -> [C_element085,H_element079]
  conduct = 2
  density = 1
  expand = 3
  formula = G4_POLYPROPYLENE
  name = G4_POLYPROPYLENE
  specific = 4
FEATURE [App::DocumentObjectGroupPython] C_element086  label="C_element : 044"  # scripted group (container) (typed FeaturePython)
  n = 8
  ref = C_element
FEATURE [App::DocumentObjectGroupPython] H_element080  label="H_element : 042"  # scripted group (container) (typed FeaturePython)
  n = 8
  ref = H_element
FEATURE [App::DocumentObjectGroupPython] G4_POLYSTYRENE  # scripted group (container) (typed FeaturePython)
  Dunit = g/cm3
  Dvalue = 1.06
  Group = -> [C_element086,H_element080]
  conduct = 2
  density = 1
  expand = 3
  formula = G4_POLYSTYRENE
  name = G4_POLYSTYRENE
  specific = 4
FEATURE [App::DocumentObjectGroupPython] C_element087  label="C_element : 045"  # scripted group (container) (typed FeaturePython)
  n = 2
  ref = C_element
FEATURE [App::DocumentObjectGroupPython] F_element014  label="F_element : 4"  # scripted group (container) (typed FeaturePython)
  n = 4
  ref = F_element
FEATURE [App::DocumentObjectGroupPython] G4_TEFLON  # scripted group (container) (typed FeaturePython)
  Dunit = g/cm3
  Dvalue = 2.2
  Group = -> [C_element087,F_element014]
  conduct = 2
  density = 1
  expand = 3
  formula = G4_TEFLON
  name = G4_TEFLON
  specific = 4
FEATURE [App::DocumentObjectGroupPython] C_element088  label="C_element : 046"  # scripted group (container) (typed FeaturePython)
  n = 2
  ref = C_element
FEATURE [App::DocumentObjectGroupPython] F_element015  label="F_element : 006"  # scripted group (container) (typed FeaturePython)
  n = 3
  ref = F_element
FEATURE [App::DocumentObjectGroupPython] Cl_element018  label="Cl_element : 008"  # scripted group (container) (typed FeaturePython)
  n = 1
  ref = Cl_element
FEATURE [App::DocumentObjectGroupPython] G4_POLYTRIFLUOROCHLOROETHYLENE  # scripted group (container) (typed FeaturePython)
  Dunit = g/cm3
  Dvalue = 2.1
  Group = -> [C_element088,F_element015,Cl_element018]
  conduct = 2
  density = 1
  expand = 3
  formula = G4_POLYTRIFLUOROCHLOROETHYLENE
  name = G4_POLYTRIFLUOROCHLOROETHYLENE
  specific = 4
FEATURE [App::DocumentObjectGroupPython] C_element089  label="C_element : 047"  # scripted group (container) (typed FeaturePython)
  n = 4
  ref = C_element
FEATURE [App::DocumentObjectGroupPython] H_element081  label="H_element : 043"  # scripted group (container) (typed FeaturePython)
  n = 6
  ref = H_element
FEATURE [App::DocumentObjectGroupPython] O_element081  label="O_element : 042"  # scripted group (container) (typed FeaturePython)
  n = 2
  ref = O_element
FEATURE [App::DocumentObjectGroupPython] G4_POLYVINYL_ACETATE  # scripted group (container) (typed FeaturePython)
  Dunit = g/cm3
  Dvalue = 1.19
  Group = -> [C_element089,H_element081,O_element081]
  conduct = 2
  density = 1
  expand = 3
  formula = G4_POLYVINYL_ACETATE
  name = G4_POLYVINYL_ACETATE
  specific = 4
FEATURE [App::DocumentObjectGroupPython] C_element090  label="C_element : 048"  # scripted group (container) (typed FeaturePython)
  n = 2
  ref = C_element
FEATURE [App::DocumentObjectGroupPython] H_element082  label="H_element : 044"  # scripted group (container) (typed FeaturePython)
  n = 4
  ref = H_element
FEATURE [App::DocumentObjectGroupPython] O_element082  label="O_element : 043"  # scripted group (container) (typed FeaturePython)
  n = 1
  ref = O_element
FEATURE [App::DocumentObjectGroupPython] G4_POLYVINYL_ALCOHOL  # scripted group (container) (typed FeaturePython)
  Dunit = g/cm3
  Dvalue = 1.3
  Group = -> [C_element090,H_element082,O_element082]
  conduct = 2
  density = 1
  expand = 3
  formula = G4_POLYVINYL_ALCOHOL
  name = G4_POLYVINYL_ALCOHOL
  specific = 4
FEATURE [App::DocumentObjectGroupPython] C_element091  label="C_element : 049"  # scripted group (container) (typed FeaturePython)
  n = 8
  ref = C_element
FEATURE [App::DocumentObjectGroupPython] H_element083  label="H_element : 045"  # scripted group (container) (typed FeaturePython)
  n = 14
  ref = H_element
FEATURE [App::DocumentObjectGroupPython] O_element083  label="O_element : 044"  # scripted group (container) (typed FeaturePython)
  n = 2
  ref = O_element
FEATURE [App::DocumentObjectGroupPython] G4_POLYVINYL_BUTYRAL  # scripted group (container) (typed FeaturePython)
  Dunit = g/cm3
  Dvalue = 1.12
  Group = -> [C_element091,H_element083,O_element083]
  conduct = 2
  density = 1
  expand = 3
  formula = G4_POLYVINYL_BUTYRAL
  name = G4_POLYVINYL_BUTYRAL
  specific = 4
FEATURE [App::DocumentObjectGroupPython] C_element092  label="C_element : 050"  # scripted group (container) (typed FeaturePython)
  n = 2
  ref = C_element
FEATURE [App::DocumentObjectGroupPython] H_element084  label="H_element : 046"  # scripted group (container) (typed FeaturePython)
  n = 3
  ref = H_element
FEATURE [App::DocumentObjectGroupPython] Cl_element019  label="Cl_element : 009"  # scripted group (container) (typed FeaturePython)
  n = 1
  ref = Cl_element
FEATURE [App::DocumentObjectGroupPython] G4_POLYVINYL_CHLORIDE  # scripted group (container) (typed FeaturePython)
  Dunit = g/cm3
  Dvalue = 1.3
  Group = -> [C_element092,H_element084,Cl_element019]
  conduct = 2
  density = 1
  expand = 3
  formula = G4_POLYVINYL_CHLORIDE
  name = G4_POLYVINYL_CHLORIDE
  specific = 4
FEATURE [App::DocumentObjectGroupPython] C_element093  label="C_element : 051"  # scripted group (container) (typed FeaturePython)
  n = 2
  ref = C_element
FEATURE [App::DocumentObjectGroupPython] H_element085  label="H_element : 047"  # scripted group (container) (typed FeaturePython)
  n = 2
  ref = H_element
FEATURE [App::DocumentObjectGroupPython] Cl_element020  label="Cl_element : 010"  # scripted group (container) (typed FeaturePython)
  n = 2
  ref = Cl_element
FEATURE [App::DocumentObjectGroupPython] G4_POLYVINYLIDENE_CHLORIDE  # scripted group (container) (typed FeaturePython)
  Dunit = g/cm3
  Dvalue = 1.7
  Group = -> [C_element093,H_element085,Cl_element020]
  conduct = 2
  density = 1
  expand = 3
  formula = G4_POLYVINYLIDENE_CHLORIDE
  name = G4_POLYVINYLIDENE_CHLORIDE
  specific = 4
FEATURE [App::DocumentObjectGroupPython] C_element094  label="C_element : 052"  # scripted group (container) (typed FeaturePython)
  n = 2
  ref = C_element
FEATURE [App::DocumentObjectGroupPython] H_element086  label="H_element : 048"  # scripted group (container) (typed FeaturePython)
  n = 2
  ref = H_element
FEATURE [App::DocumentObjectGroupPython] F_element016  label="F_element : 007"  # scripted group (container) (typed FeaturePython)
  n = 2
  ref = F_element
FEATURE [App::DocumentObjectGroupPython] G4_POLYVINYLIDENE_FLUORIDE  # scripted group (container) (typed FeaturePython)
  Dunit = g/cm3
  Dvalue = 1.76
  Group = -> [C_element094,H_element086,F_element016]
  conduct = 2
  density = 1
  expand = 3
  formula = G4_POLYVINYLIDENE_FLUORIDE
  name = G4_POLYVINYLIDENE_FLUORIDE
  specific = 4
FEATURE [App::DocumentObjectGroupPython] C_element095  label="C_element : 053"  # scripted group (container) (typed FeaturePython)
  n = 6
  ref = C_element
FEATURE [App::DocumentObjectGroupPython] H_element087  label="H_element : 9"  # scripted group (container) (typed FeaturePython)
  n = 9
  ref = H_element
FEATURE [App::DocumentObjectGroupPython] N_element037  label="N_element : 016"  # scripted group (container) (typed FeaturePython)
  n = 1
  ref = N_element
FEATURE [App::DocumentObjectGroupPython] O_element084  label="O_element : 045"  # scripted group (container) (typed FeaturePython)
  n = 1
  ref = O_element
FEATURE [App::DocumentObjectGroupPython] G4_POLYVINYL_PYRROLIDONE  # scripted group (container) (typed FeaturePython)
  Dunit = g/cm3
  Dvalue = 1.25
  Group = -> [C_element095,H_element087,N_element037,O_element084]
  conduct = 2
  density = 1
  expand = 3
  formula = G4_POLYVINYL_PYRROLIDONE
  name = G4_POLYVINYL_PYRROLIDONE
  specific = 4
FEATURE [App::DocumentObjectGroupPython] K_element008  label="K_element : 1"  # scripted group (container) (typed FeaturePython)
  n = 1
  ref = K_element
FEATURE [App::DocumentObjectGroupPython] I_element006  label="I_element : 003"  # scripted group (container) (typed FeaturePython)
  n = 1
  ref = I_element
FEATURE [App::DocumentObjectGroupPython] G4_POTASSIUM_IODIDE  # scripted group (container) (typed FeaturePython)
  Dunit = g/cm3
  Dvalue = 3.13
  Group = -> [K_element008,I_element006]
  conduct = 2
  density = 1
  expand = 3
  formula = G4_POTASSIUM_IODIDE
  name = G4_POTASSIUM_IODIDE
  specific = 4
FEATURE [App::DocumentObjectGroupPython] K_element009  label="K_element : 2"  # scripted group (container) (typed FeaturePython)
  n = 2
  ref = K_element
FEATURE [App::DocumentObjectGroupPython] O_element085  label="O_element : 046"  # scripted group (container) (typed FeaturePython)
  n = 1
  ref = O_element
FEATURE [App::DocumentObjectGroupPython] G4_POTASSIUM_OXIDE  # scripted group (container) (typed FeaturePython)
  Dunit = g/cm3
  Dvalue = 2.32
  Group = -> [K_element009,O_element085]
  conduct = 2
  density = 1
  expand = 3
  formula = G4_POTASSIUM_OXIDE
  name = G4_POTASSIUM_OXIDE
  specific = 4
FEATURE [App::DocumentObjectGroupPython] C_element096  label="C_element : 054"  # scripted group (container) (typed FeaturePython)
  n = 3
  ref = C_element
FEATURE [App::DocumentObjectGroupPython] H_element088  label="H_element : 049"  # scripted group (container) (typed FeaturePython)
  n = 8
  ref = H_element
FEATURE [App::DocumentObjectGroupPython] G4_PROPANE  # scripted group (container) (typed FeaturePython)
  Dunit = g/cm3
  Dvalue = 0.00187939
  Group = -> [C_element096,H_element088]
  conduct = 2
  density = 1
  expand = 3
  formula = G4_PROPANE
  name = G4_PROPANE
  specific = 4
FEATURE [App::DocumentObjectGroupPython] C_element097  label="C_element : 055"  # scripted group (container) (typed FeaturePython)
  n = 3
  ref = C_element
FEATURE [App::DocumentObjectGroupPython] H_element089  label="H_element : 050"  # scripted group (container) (typed FeaturePython)
  n = 8
  ref = H_element
FEATURE [App::DocumentObjectGroupPython] G4_lPROPANE  # scripted group (container) (typed FeaturePython)
  Dunit = g/cm3
  Dvalue = 0.43
  Group = -> [C_element097,H_element089]
  conduct = 2
  density = 1
  expand = 3
  formula = G4_lPROPANE
  name = G4_lPROPANE
  specific = 4
FEATURE [App::DocumentObjectGroupPython] C_element098  label="C_element : 056"  # scripted group (container) (typed FeaturePython)
  n = 3
  ref = C_element
FEATURE [App::DocumentObjectGroupPython] H_element090  label="H_element : 051"  # scripted group (container) (typed FeaturePython)
  n = 8
  ref = H_element
FEATURE [App::DocumentObjectGroupPython] O_element086  label="O_element : 047"  # scripted group (container) (typed FeaturePython)
  n = 1
  ref = O_element
FEATURE [App::DocumentObjectGroupPython] G4_N_PROPYL_ALCOHOL  label="G4_N-PROPYL_ALCOHOL"  # scripted group (container) (typed FeaturePython)
  Dunit = g/cm3
  Dvalue = 0.8035
  Group = -> [C_element098,H_element090,O_element086]
  conduct = 2
  density = 1
  expand = 3
  formula = G4_N-PROPYL_ALCOHOL
  name = G4_N-PROPYL_ALCOHOL
  specific = 4
FEATURE [App::DocumentObjectGroupPython] C_element099  label="C_element : 057"  # scripted group (container) (typed FeaturePython)
  n = 5
  ref = C_element
FEATURE [App::DocumentObjectGroupPython] H_element091  label="H_element : 052"  # scripted group (container) (typed FeaturePython)
  n = 5
  ref = H_element
FEATURE [App::DocumentObjectGroupPython] N_element038  label="N_element : 017"  # scripted group (container) (typed FeaturePython)
  n = 1
  ref = N_element
FEATURE [App::DocumentObjectGroupPython] G4_PYRIDINE  # scripted group (container) (typed FeaturePython)
  Dunit = g/cm3
  Dvalue = 0.9819
  Group = -> [C_element099,H_element091,N_element038]
  conduct = 2
  density = 1
  expand = 3
  formula = G4_PYRIDINE
  name = G4_PYRIDINE
  specific = 4
FEATURE [App::DocumentObjectGroupPython] H_element092  label="H_element : 0.144"  # scripted group (container) (typed FeaturePython)
  n = 0.143711
FEATURE [App::DocumentObjectGroupPython] C_element100  label="C_element : 0.856"  # scripted group (container) (typed FeaturePython)
  n = 0.856289
FEATURE [App::DocumentObjectGroupPython] G4_RUBBER_BUTYL  # scripted group (container) (typed FeaturePython)
  Dunit = g/cm3
  Dvalue = 0.92
  Group = -> [H_element092,C_element100]
  conduct = 2
  density = 1
  expand = 3
  formula = G4_RUBBER_BUTYL
  name = G4_RUBBER_BUTYL
  specific = 4
FEATURE [App::DocumentObjectGroupPython] H_element093  label="H_element : 0.118"  # scripted group (container) (typed FeaturePython)
  n = 0.118371
FEATURE [App::DocumentObjectGroupPython] C_element101  label="C_element : 0.882"  # scripted group (container) (typed FeaturePython)
  n = 0.881629
FEATURE [App::DocumentObjectGroupPython] G4_RUBBER_NATURAL  # scripted group (container) (typed FeaturePython)
  Dunit = g/cm3
  Dvalue = 0.92
  Group = -> [H_element093,C_element101]
  conduct = 2
  density = 1
  expand = 3
  formula = G4_RUBBER_NATURAL
  name = G4_RUBBER_NATURAL
  specific = 4
FEATURE [App::DocumentObjectGroupPython] H_element094  label="H_element : 0.145"  # scripted group (container) (typed FeaturePython)
  n = 0.05692
FEATURE [App::DocumentObjectGroupPython] C_element102  label="C_element : 0.543"  # scripted group (container) (typed FeaturePython)
  n = 0.542646
FEATURE [App::DocumentObjectGroupPython] Cl_element021  label="Cl_element : 0.400"  # scripted group (container) (typed FeaturePython)
  n = 0.400434
FEATURE [App::DocumentObjectGroupPython] G4_RUBBER_NEOPRENE  # scripted group (container) (typed FeaturePython)
  Dunit = g/cm3
  Dvalue = 1.23
  Group = -> [H_element094,C_element102,Cl_element021]
  conduct = 2
  density = 1
  expand = 3
  formula = G4_RUBBER_NEOPRENE
  name = G4_RUBBER_NEOPRENE
  specific = 4
FEATURE [App::DocumentObjectGroupPython] Si_element006  label="Si_element : 1"  # scripted group (container) (typed FeaturePython)
  n = 1
  ref = Si_element
FEATURE [App::DocumentObjectGroupPython] O_element087  label="O_element : 048"  # scripted group (container) (typed FeaturePython)
  n = 2
  ref = O_element
FEATURE [App::DocumentObjectGroupPython] G4_SILICON_DIOXIDE  # scripted group (container) (typed FeaturePython)
  Dunit = g/cm3
  Dvalue = 2.32
  Group = -> [Si_element006,O_element087]
  conduct = 2
  density = 1
  expand = 3
  formula = G4_SILICON_DIOXIDE
  name = G4_SILICON_DIOXIDE
  specific = 4
FEATURE [App::DocumentObjectGroupPython] Ag_element002  label="Ag_element : 1"  # scripted group (container) (typed FeaturePython)
  n = 1
  ref = Ag_element
FEATURE [App::DocumentObjectGroupPython] Br_element005  label="Br_element : 003"  # scripted group (container) (typed FeaturePython)
  n = 1
  ref = Br_element
FEATURE [App::DocumentObjectGroupPython] G4_SILVER_BROMIDE  # scripted group (container) (typed FeaturePython)
  Dunit = g/cm3
  Dvalue = 6.473
  Group = -> [Ag_element002,Br_element005]
  conduct = 2
  density = 1
  expand = 3
  formula = G4_SILVER_BROMIDE
  name = G4_SILVER_BROMIDE
  specific = 4
FEATURE [App::DocumentObjectGroupPython] Ag_element003  label="Ag_element : 002"  # scripted group (container) (typed FeaturePython)
  n = 1
  ref = Ag_element
FEATURE [App::DocumentObjectGroupPython] Cl_element022  label="Cl_element : 011"  # scripted group (container) (typed FeaturePython)
  n = 1
  ref = Cl_element
FEATURE [App::DocumentObjectGroupPython] G4_SILVER_CHLORIDE  # scripted group (container) (typed FeaturePython)
  Dunit = g/cm3
  Dvalue = 5.56
  Group = -> [Ag_element003,Cl_element022]
  conduct = 2
  density = 1
  expand = 3
  formula = G4_SILVER_CHLORIDE
  name = G4_SILVER_CHLORIDE
  specific = 4
FEATURE [App::DocumentObjectGroupPython] Br_element006  label="Br_element : 0.423"  # scripted group (container) (typed FeaturePython)
  n = 0.422895
FEATURE [App::DocumentObjectGroupPython] Ag_element004  label="Ag_element : 0.574"  # scripted group (container) (typed FeaturePython)
  n = 0.573748
FEATURE [App::DocumentObjectGroupPython] I_element007  label="I_element : 0.649"  # scripted group (container) (typed FeaturePython)
  n = 0.003357
FEATURE [App::DocumentObjectGroupPython] G4_SILVER_HALIDES  # scripted group (container) (typed FeaturePython)
  Dunit = g/cm3
  Dvalue = 6.47
  Group = -> [Br_element006,Ag_element004,I_element007]
  conduct = 2
  density = 1
  expand = 3
  formula = G4_SILVER_HALIDES
  name = G4_SILVER_HALIDES
  specific = 4
FEATURE [App::DocumentObjectGroupPython] Ag_element005  label="Ag_element : 003"  # scripted group (container) (typed FeaturePython)
  n = 1
  ref = Ag_element
FEATURE [App::DocumentObjectGroupPython] I_element008  label="I_element : 004"  # scripted group (container) (typed FeaturePython)
  n = 1
  ref = I_element
FEATURE [App::DocumentObjectGroupPython] G4_SILVER_IODIDE  # scripted group (container) (typed FeaturePython)
  Dunit = g/cm3
  Dvalue = 6.01
  Group = -> [Ag_element005,I_element008]
  conduct = 2
  density = 1
  expand = 3
  formula = G4_SILVER_IODIDE
  name = G4_SILVER_IODIDE
  specific = 4
FEATURE [App::DocumentObjectGroupPython] H_element095  label="H_element : 0.100"  # scripted group (container) (typed FeaturePython)
  n = 0.1
FEATURE [App::DocumentObjectGroupPython] C_element103  label="C_element : 0.204"  # scripted group (container) (typed FeaturePython)
  n = 0.204
FEATURE [App::DocumentObjectGroupPython] N_element039  label="N_element : 0.759"  # scripted group (container) (typed FeaturePython)
  n = 0.042
FEATURE [App::DocumentObjectGroupPython] O_element088  label="O_element : 0.645"  # scripted group (container) (typed FeaturePython)
  n = 0.645
FEATURE [App::DocumentObjectGroupPython] Na_element013  label="Na_element : 0.100"  # scripted group (container) (typed FeaturePython)
  n = 0.002
FEATURE [App::DocumentObjectGroupPython] P_element009  label="P_element : 0.107"  # scripted group (container) (typed FeaturePython)
  n = 0.001
FEATURE [App::DocumentObjectGroupPython] S_element020  label="S_element : 0.021"  # scripted group (container) (typed FeaturePython)
  n = 0.002
FEATURE [App::DocumentObjectGroupPython] Cl_element023  label="Cl_element : 0.590"  # scripted group (container) (typed FeaturePython)
  n = 0.003
FEATURE [App::DocumentObjectGroupPython] K_element010  label="K_element : 0.001"  # scripted group (container) (typed FeaturePython)
  n = 0.001
FEATURE [App::DocumentObjectGroupPython] G4_SKIN_ICRP  # scripted group (container) (typed FeaturePython)
  Dunit = g/cm3
  Dvalue = 1.09
  Group = -> [H_element095,C_element103,N_element039,O_element088,Na_element013,P_element009,S_element020,Cl_element023,K_element010]
  conduct = 2
  density = 1
  expand = 3
  formula = G4_SKIN_ICRP
  name = G4_SKIN_ICRP
  specific = 4
FEATURE [App::DocumentObjectGroupPython] Na_element014  label="Na_element : 2"  # scripted group (container) (typed FeaturePython)
  n = 2
  ref = Na_element
FEATURE [App::DocumentObjectGroupPython] C_element104  label="C_element : 058"  # scripted group (container) (typed FeaturePython)
  n = 1
  ref = C_element
FEATURE [App::DocumentObjectGroupPython] O_element089  label="O_element : 049"  # scripted group (container) (typed FeaturePython)
  n = 3
  ref = O_element
FEATURE [App::DocumentObjectGroupPython] G4_SODIUM_CARBONATE  # scripted group (container) (typed FeaturePython)
  Dunit = g/cm3
  Dvalue = 2.532
  Group = -> [Na_element014,C_element104,O_element089]
  conduct = 2
  density = 1
  expand = 3
  formula = G4_SODIUM_CARBONATE
  name = G4_SODIUM_CARBONATE
  specific = 4
FEATURE [App::DocumentObjectGroupPython] Na_element015  label="Na_element : 1"  # scripted group (container) (typed FeaturePython)
  n = 1
  ref = Na_element
FEATURE [App::DocumentObjectGroupPython] I_element009  label="I_element : 005"  # scripted group (container) (typed FeaturePython)
  n = 1
  ref = I_element
FEATURE [App::DocumentObjectGroupPython] G4_SODIUM_IODIDE  # scripted group (container) (typed FeaturePython)
  Dunit = g/cm3
  Dvalue = 3.667
  Group = -> [Na_element015,I_element009]
  conduct = 2
  density = 1
  expand = 3
  formula = G4_SODIUM_IODIDE
  name = G4_SODIUM_IODIDE
  specific = 4
FEATURE [App::DocumentObjectGroupPython] Na_element016  label="Na_element : 003"  # scripted group (container) (typed FeaturePython)
  n = 2
  ref = Na_element
FEATURE [App::DocumentObjectGroupPython] O_element090  label="O_element : 050"  # scripted group (container) (typed FeaturePython)
  n = 1
  ref = O_element
FEATURE [App::DocumentObjectGroupPython] G4_SODIUM_MONOXIDE  # scripted group (container) (typed FeaturePython)
  Dunit = g/cm3
  Dvalue = 2.27
  Group = -> [Na_element016,O_element090]
  conduct = 2
  density = 1
  expand = 3
  formula = G4_SODIUM_MONOXIDE
  name = G4_SODIUM_MONOXIDE
  specific = 4
FEATURE [App::DocumentObjectGroupPython] Na_element017  label="Na_element : 004"  # scripted group (container) (typed FeaturePython)
  n = 1
  ref = Na_element
FEATURE [App::DocumentObjectGroupPython] N_element040  label="N_element : 018"  # scripted group (container) (typed FeaturePython)
  n = 1
  ref = N_element
FEATURE [App::DocumentObjectGroupPython] O_element091  label="O_element : 051"  # scripted group (container) (typed FeaturePython)
  n = 3
  ref = O_element
FEATURE [App::DocumentObjectGroupPython] G4_SODIUM_NITRATE  # scripted group (container) (typed FeaturePython)
  Dunit = g/cm3
  Dvalue = 2.261
  Group = -> [Na_element017,N_element040,O_element091]
  conduct = 2
  density = 1
  expand = 3
  formula = G4_SODIUM_NITRATE
  name = G4_SODIUM_NITRATE
  specific = 4
FEATURE [App::DocumentObjectGroupPython] C_element105  label="C_element : 059"  # scripted group (container) (typed FeaturePython)
  n = 14
  ref = C_element
FEATURE [App::DocumentObjectGroupPython] H_element096  label="H_element : 053"  # scripted group (container) (typed FeaturePython)
  n = 12
  ref = H_element
FEATURE [App::DocumentObjectGroupPython] G4_STILBENE  # scripted group (container) (typed FeaturePython)
  Dunit = g/cm3
  Dvalue = 0.9707
  Group = -> [C_element105,H_element096]
  conduct = 2
  density = 1
  expand = 3
  formula = G4_STILBENE
  name = G4_STILBENE
  specific = 4
FEATURE [App::DocumentObjectGroupPython] C_element106  label="C_element : 12"  # scripted group (container) (typed FeaturePython)
  n = 12
  ref = C_element
FEATURE [App::DocumentObjectGroupPython] H_element097  label="H_element : 22"  # scripted group (container) (typed FeaturePython)
  n = 22
  ref = H_element
FEATURE [App::DocumentObjectGroupPython] O_element092  label="O_element : 11"  # scripted group (container) (typed FeaturePython)
  n = 11
  ref = O_element
FEATURE [App::DocumentObjectGroupPython] G4_SUCROSE  # scripted group (container) (typed FeaturePython)
  Dunit = g/cm3
  Dvalue = 1.5805
  Group = -> [C_element106,H_element097,O_element092]
  conduct = 2
  density = 1
  expand = 3
  formula = G4_SUCROSE
  name = G4_SUCROSE
  specific = 4
FEATURE [App::DocumentObjectGroupPython] C_element107  label="C_element : 18"  # scripted group (container) (typed FeaturePython)
  n = 18
  ref = C_element
FEATURE [App::DocumentObjectGroupPython] H_element098  label="H_element : 054"  # scripted group (container) (typed FeaturePython)
  n = 14
  ref = H_element
FEATURE [App::DocumentObjectGroupPython] G4_TERPHENYL  # scripted group (container) (typed FeaturePython)
  Dunit = g/cm3
  Dvalue = 1.24
  Group = -> [C_element107,H_element098]
  conduct = 2
  density = 1
  expand = 3
  formula = G4_TERPHENYL
  name = G4_TERPHENYL
  specific = 4
FEATURE [App::DocumentObjectGroupPython] H_element099  label="H_element : 0.146"  # scripted group (container) (typed FeaturePython)
  n = 0.106
FEATURE [App::DocumentObjectGroupPython] C_element108  label="C_element : 0.883"  # scripted group (container) (typed FeaturePython)
  n = 0.099
FEATURE [App::DocumentObjectGroupPython] N_element041  label="N_element : 0.020"  # scripted group (container) (typed FeaturePython)
  n = 0.02
FEATURE [App::DocumentObjectGroupPython] O_element093  label="O_element : 0.766"  # scripted group (container) (typed FeaturePython)
  n = 0.766
FEATURE [App::DocumentObjectGroupPython] Na_element018  label="Na_element : 0.101"  # scripted group (container) (typed FeaturePython)
  n = 0.002
FEATURE [App::DocumentObjectGroupPython] P_element010  label="P_element : 0.108"  # scripted group (container) (typed FeaturePython)
  n = 0.001
FEATURE [App::DocumentObjectGroupPython] S_element021  label="S_element : 0.022"  # scripted group (container) (typed FeaturePython)
  n = 0.002
FEATURE [App::DocumentObjectGroupPython] Cl_element024  label="Cl_element : 0.002"  # scripted group (container) (typed FeaturePython)
  n = 0.002
FEATURE [App::DocumentObjectGroupPython] K_element011  label="K_element : 0.017"  # scripted group (container) (typed FeaturePython)
  n = 0.002
FEATURE [App::DocumentObjectGroupPython] G4_TESTIS_ICRP  # scripted group (container) (typed FeaturePython)
  Dunit = g/cm3
  Dvalue = 1.04
  Group = -> [H_element099,C_element108,N_element041,O_element093,Na_element018,P_element010,S_element021,Cl_element024,K_element011]
  conduct = 2
  density = 1
  expand = 3
  formula = G4_TESTIS_ICRP
  name = G4_TESTIS_ICRP
  specific = 4
FEATURE [App::DocumentObjectGroupPython] C_element109  label="C_element : 060"  # scripted group (container) (typed FeaturePython)
  n = 2
  ref = C_element
FEATURE [App::DocumentObjectGroupPython] Cl_element025  label="Cl_element : 012"  # scripted group (container) (typed FeaturePython)
  n = 4
  ref = Cl_element
FEATURE [App::DocumentObjectGroupPython] G4_TETRACHLOROETHYLENE  # scripted group (container) (typed FeaturePython)
  Dunit = g/cm3
  Dvalue = 1.625
  Group = -> [C_element109,Cl_element025]
  conduct = 2
  density = 1
  expand = 3
  formula = G4_TETRACHLOROETHYLENE
  name = G4_TETRACHLOROETHYLENE
  specific = 4
FEATURE [App::DocumentObjectGroupPython] Tl_element001  label="Tl_element : 1"  # scripted group (container) (typed FeaturePython)
  n = 1
  ref = Tl_element
FEATURE [App::DocumentObjectGroupPython] Cl_element026  label="Cl_element : 013"  # scripted group (container) (typed FeaturePython)
  n = 1
  ref = Cl_element
FEATURE [App::DocumentObjectGroupPython] G4_THALLIUM_CHLORIDE  # scripted group (container) (typed FeaturePython)
  Dunit = g/cm3
  Dvalue = 7.004
  Group = -> [Tl_element001,Cl_element026]
  conduct = 2
  density = 1
  expand = 3
  formula = G4_THALLIUM_CHLORIDE
  name = G4_THALLIUM_CHLORIDE
  specific = 4
FEATURE [App::DocumentObjectGroupPython] H_element100  label="H_element : 0.147"  # scripted group (container) (typed FeaturePython)
  n = 0.105
FEATURE [App::DocumentObjectGroupPython] C_element110  label="C_element : 0.256"  # scripted group (container) (typed FeaturePython)
  n = 0.256
FEATURE [App::DocumentObjectGroupPython] N_element042  label="N_element : 0.760"  # scripted group (container) (typed FeaturePython)
  n = 0.027
FEATURE [App::DocumentObjectGroupPython] O_element094  label="O_element : 0.602"  # scripted group (container) (typed FeaturePython)
  n = 0.602
FEATURE [App::DocumentObjectGroupPython] Na_element019  label="Na_element : 0.102"  # scripted group (container) (typed FeaturePython)
  n = 0.001
FEATURE [App::DocumentObjectGroupPython] P_element011  label="P_element : 0.109"  # scripted group (container) (typed FeaturePython)
  n = 0.002
FEATURE [App::DocumentObjectGroupPython] S_element022  label="S_element : 0.023"  # scripted group (container) (typed FeaturePython)
  n = 0.003
FEATURE [App::DocumentObjectGroupPython] Cl_element027  label="Cl_element : 0.591"  # scripted group (container) (typed FeaturePython)
  n = 0.002
FEATURE [App::DocumentObjectGroupPython] K_element012  label="K_element : 0.018"  # scripted group (container) (typed FeaturePython)
  n = 0.002
FEATURE [App::DocumentObjectGroupPython] G4_TISSUE_SOFT_ICRP  # scripted group (container) (typed FeaturePython)
  Dunit = g/cm3
  Dvalue = 1.03
  Group = -> [H_element100,C_element110,N_element042,O_element094,Na_element019,P_element011,S_element022,Cl_element027,K_element012]
  conduct = 2
  density = 1
  expand = 3
  formula = G4_TISSUE_SOFT_ICRP
  name = G4_TISSUE_SOFT_ICRP
  specific = 4
FEATURE [App::DocumentObjectGroupPython] H_element101  label="H_element : 0.148"  # scripted group (container) (typed FeaturePython)
  n = 0.101
FEATURE [App::DocumentObjectGroupPython] C_element111  label="C_element : 0.111"  # scripted group (container) (typed FeaturePython)
  n = 0.111
FEATURE [App::DocumentObjectGroupPython] N_element043  label="N_element : 0.026"  # scripted group (container) (typed FeaturePython)
  n = 0.026
FEATURE [App::DocumentObjectGroupPython] O_element095  label="O_element : 0.762"  # scripted group (container) (typed FeaturePython)
  n = 0.762
FEATURE [App::DocumentObjectGroupPython] G4_TISSUE_SOFT_ICRU_4  label="G4_TISSUE_SOFT_ICRU-4"  # scripted group (container) (typed FeaturePython)
  Dunit = g/cm3
  Dvalue = 1
  Group = -> [H_element101,C_element111,N_element043,O_element095]
  conduct = 2
  density = 1
  expand = 3
  formula = G4_TISSUE_SOFT_ICRU-4
  name = G4_TISSUE_SOFT_ICRU-4
  specific = 4
FEATURE [App::DocumentObjectGroupPython] H_element102  label="H_element : 0.149"  # scripted group (container) (typed FeaturePython)
  n = 0.101869
FEATURE [App::DocumentObjectGroupPython] C_element112  label="C_element : 0.456"  # scripted group (container) (typed FeaturePython)
  n = 0.456179
FEATURE [App::DocumentObjectGroupPython] N_element044  label="N_element : 0.761"  # scripted group (container) (typed FeaturePython)
  n = 0.035172
FEATURE [App::DocumentObjectGroupPython] O_element096  label="O_element : 0.407"  # scripted group (container) (typed FeaturePython)
  n = 0.40678
FEATURE [App::DocumentObjectGroupPython] G4_TISSUE_METHANE  label="G4_TISSUE-METHANE"  # scripted group (container) (typed FeaturePython)
  Dunit = g/cm3
  Dvalue = 0.00106409
  Group = -> [H_element102,C_element112,N_element044,O_element096]
  conduct = 2
  density = 1
  expand = 3
  formula = G4_TISSUE-METHANE
  name = G4_TISSUE-METHANE
  specific = 4
FEATURE [App::DocumentObjectGroupPython] H_element103  label="H_element : 0.103"  # scripted group (container) (typed FeaturePython)
  n = 0.102672
FEATURE [App::DocumentObjectGroupPython] C_element113  label="C_element : 0.569"  # scripted group (container) (typed FeaturePython)
  n = 0.56894
FEATURE [App::DocumentObjectGroupPython] N_element045  label="N_element : 0.762"  # scripted group (container) (typed FeaturePython)
  n = 0.035022
FEATURE [App::DocumentObjectGroupPython] O_element097  label="O_element : 0.293"  # scripted group (container) (typed FeaturePython)
  n = 0.293366
FEATURE [App::DocumentObjectGroupPython] G4_TISSUE_PROPANE  label="G4_TISSUE-PROPANE"  # scripted group (container) (typed FeaturePython)
  Dunit = g/cm3
  Dvalue = 0.00182628
  Group = -> [H_element103,C_element113,N_element045,O_element097]
  conduct = 2
  density = 1
  expand = 3
  formula = G4_TISSUE-PROPANE
  name = G4_TISSUE-PROPANE
  specific = 4
FEATURE [App::DocumentObjectGroupPython] Ti_element003  label="Ti_element : 1"  # scripted group (container) (typed FeaturePython)
  n = 1
  ref = Ti_element
FEATURE [App::DocumentObjectGroupPython] O_element098  label="O_element : 052"  # scripted group (container) (typed FeaturePython)
  n = 2
  ref = O_element
FEATURE [App::DocumentObjectGroupPython] G4_TITANIUM_DIOXIDE  # scripted group (container) (typed FeaturePython)
  Dunit = g/cm3
  Dvalue = 4.26
  Group = -> [Ti_element003,O_element098]
  conduct = 2
  density = 1
  expand = 3
  formula = G4_TITANIUM_DIOXIDE
  name = G4_TITANIUM_DIOXIDE
  specific = 4
FEATURE [App::DocumentObjectGroupPython] C_element114  label="C_element : 061"  # scripted group (container) (typed FeaturePython)
  n = 7
  ref = C_element
FEATURE [App::DocumentObjectGroupPython] H_element104  label="H_element : 055"  # scripted group (container) (typed FeaturePython)
  n = 8
  ref = H_element
FEATURE [App::DocumentObjectGroupPython] G4_TOLUENE  # scripted group (container) (typed FeaturePython)
  Dunit = g/cm3
  Dvalue = 0.8669
  Group = -> [C_element114,H_element104]
  conduct = 2
  density = 1
  expand = 3
  formula = G4_TOLUENE
  name = G4_TOLUENE
  specific = 4
FEATURE [App::DocumentObjectGroupPython] C_element115  label="C_element : 062"  # scripted group (container) (typed FeaturePython)
  n = 2
  ref = C_element
FEATURE [App::DocumentObjectGroupPython] H_element105  label="H_element : 056"  # scripted group (container) (typed FeaturePython)
  n = 1
  ref = H_element
FEATURE [App::DocumentObjectGroupPython] Cl_element028  label="Cl_element : 014"  # scripted group (container) (typed FeaturePython)
  n = 3
  ref = Cl_element
FEATURE [App::DocumentObjectGroupPython] G4_TRICHLOROETHYLENE  # scripted group (container) (typed FeaturePython)
  Dunit = g/cm3
  Dvalue = 1.46
  Group = -> [C_element115,H_element105,Cl_element028]
  conduct = 2
  density = 1
  expand = 3
  formula = G4_TRICHLOROETHYLENE
  name = G4_TRICHLOROETHYLENE
  specific = 4
FEATURE [App::DocumentObjectGroupPython] C_element116  label="C_element : 063"  # scripted group (container) (typed FeaturePython)
  n = 6
  ref = C_element
FEATURE [App::DocumentObjectGroupPython] H_element106  label="H_element : 15"  # scripted group (container) (typed FeaturePython)
  n = 15
  ref = H_element
FEATURE [App::DocumentObjectGroupPython] O_element099  label="O_element : 053"  # scripted group (container) (typed FeaturePython)
  n = 4
  ref = O_element
FEATURE [App::DocumentObjectGroupPython] P_element012  label="P_element : 1"  # scripted group (container) (typed FeaturePython)
  n = 1
  ref = P_element
FEATURE [App::DocumentObjectGroupPython] G4_TRIETHYL_PHOSPHATE  # scripted group (container) (typed FeaturePython)
  Dunit = g/cm3
  Dvalue = 1.07
  Group = -> [C_element116,H_element106,O_element099,P_element012]
  conduct = 2
  density = 1
  expand = 3
  formula = G4_TRIETHYL_PHOSPHATE
  name = G4_TRIETHYL_PHOSPHATE
  specific = 4
FEATURE [App::DocumentObjectGroupPython] W_element003  label="W_element : 003"  # scripted group (container) (typed FeaturePython)
  n = 1
  ref = W_element
FEATURE [App::DocumentObjectGroupPython] F_element017  label="F_element : 6"  # scripted group (container) (typed FeaturePython)
  n = 6
  ref = F_element
FEATURE [App::DocumentObjectGroupPython] G4_TUNGSTEN_HEXAFLUORIDE  # scripted group (container) (typed FeaturePython)
  Dunit = g/cm3
  Dvalue = 2.4
  Group = -> [W_element003,F_element017]
  conduct = 2
  density = 1
  expand = 3
  formula = G4_TUNGSTEN_HEXAFLUORIDE
  name = G4_TUNGSTEN_HEXAFLUORIDE
  specific = 4
FEATURE [App::DocumentObjectGroupPython] U_element001  label="U_element : 1"  # scripted group (container) (typed FeaturePython)
  n = 1
  ref = U_element
FEATURE [App::DocumentObjectGroupPython] C_element117  label="C_element : 064"  # scripted group (container) (typed FeaturePython)
  n = 2
  ref = C_element
FEATURE [App::DocumentObjectGroupPython] G4_URANIUM_DICARBIDE  # scripted group (container) (typed FeaturePython)
  Dunit = g/cm3
  Dvalue = 11.28
  Group = -> [U_element001,C_element117]
  conduct = 2
  density = 1
  expand = 3
  formula = G4_URANIUM_DICARBIDE
  name = G4_URANIUM_DICARBIDE
  specific = 4
FEATURE [App::DocumentObjectGroupPython] U_element002  label="U_element : 002"  # scripted group (container) (typed FeaturePython)
  n = 1
  ref = U_element
FEATURE [App::DocumentObjectGroupPython] C_element118  label="C_element : 065"  # scripted group (container) (typed FeaturePython)
  n = 1
  ref = C_element
FEATURE [App::DocumentObjectGroupPython] G4_URANIUM_MONOCARBIDE  # scripted group (container) (typed FeaturePython)
  Dunit = g/cm3
  Dvalue = 13.63
  Group = -> [U_element002,C_element118]
  conduct = 2
  density = 1
  expand = 3
  formula = G4_URANIUM_MONOCARBIDE
  name = G4_URANIUM_MONOCARBIDE
  specific = 4
FEATURE [App::DocumentObjectGroupPython] U_element003  label="U_element : 003"  # scripted group (container) (typed FeaturePython)
  n = 1
  ref = U_element
FEATURE [App::DocumentObjectGroupPython] O_element100  label="O_element : 054"  # scripted group (container) (typed FeaturePython)
  n = 2
  ref = O_element
FEATURE [App::DocumentObjectGroupPython] G4_URANIUM_OXIDE  # scripted group (container) (typed FeaturePython)
  Dunit = g/cm3
  Dvalue = 10.96
  Group = -> [U_element003,O_element100]
  conduct = 2
  density = 1
  expand = 3
  formula = G4_URANIUM_OXIDE
  name = G4_URANIUM_OXIDE
  specific = 4
FEATURE [App::DocumentObjectGroupPython] C_element119  label="C_element : 066"  # scripted group (container) (typed FeaturePython)
  n = 1
  ref = C_element
FEATURE [App::DocumentObjectGroupPython] H_element107  label="H_element : 057"  # scripted group (container) (typed FeaturePython)
  n = 4
  ref = H_element
FEATURE [App::DocumentObjectGroupPython] N_element046  label="N_element : 019"  # scripted group (container) (typed FeaturePython)
  n = 2
  ref = N_element
FEATURE [App::DocumentObjectGroupPython] O_element101  label="O_element : 055"  # scripted group (container) (typed FeaturePython)
  n = 1
  ref = O_element
FEATURE [App::DocumentObjectGroupPython] G4_UREA  # scripted group (container) (typed FeaturePython)
  Dunit = g/cm3
  Dvalue = 1.323
  Group = -> [C_element119,H_element107,N_element046,O_element101]
  conduct = 2
  density = 1
  expand = 3
  formula = G4_UREA
  name = G4_UREA
  specific = 4
FEATURE [App::DocumentObjectGroupPython] C_element120  label="C_element : 067"  # scripted group (container) (typed FeaturePython)
  n = 5
  ref = C_element
FEATURE [App::DocumentObjectGroupPython] H_element108  label="H_element : 058"  # scripted group (container) (typed FeaturePython)
  n = 11
  ref = H_element
FEATURE [App::DocumentObjectGroupPython] N_element047  label="N_element : 020"  # scripted group (container) (typed FeaturePython)
  n = 1
  ref = N_element
FEATURE [App::DocumentObjectGroupPython] O_element102  label="O_element : 056"  # scripted group (container) (typed FeaturePython)
  n = 2
  ref = O_element
FEATURE [App::DocumentObjectGroupPython] G4_VALINE  # scripted group (container) (typed FeaturePython)
  Dunit = g/cm3
  Dvalue = 1.23
  Group = -> [C_element120,H_element108,N_element047,O_element102]
  conduct = 2
  density = 1
  expand = 3
  formula = G4_VALINE
  name = G4_VALINE
  specific = 4
FEATURE [App::DocumentObjectGroupPython] H_element109  label="H_element : 0.009"  # scripted group (container) (typed FeaturePython)
  n = 0.009417
FEATURE [App::DocumentObjectGroupPython] C_element121  label="C_element : 0.281"  # scripted group (container) (typed FeaturePython)
  n = 0.280555
FEATURE [App::DocumentObjectGroupPython] F_element018  label="F_element : 0.710"  # scripted group (container) (typed FeaturePython)
  n = 0.710028
FEATURE [App::DocumentObjectGroupPython] G4_VITON  # scripted group (container) (typed FeaturePython)
  Dunit = g/cm3
  Dvalue = 1.8
  Group = -> [H_element109,C_element121,F_element018]
  conduct = 2
  density = 1
  expand = 3
  formula = G4_VITON
  name = G4_VITON
  specific = 4
FEATURE [App::DocumentObjectGroupPython] H_element110  label="H_element : 059"  # scripted group (container) (typed FeaturePython)
  n = 2
  ref = H_element
FEATURE [App::DocumentObjectGroupPython] O_element103  label="O_element : 057"  # scripted group (container) (typed FeaturePython)
  n = 1
  ref = O_element
FEATURE [App::DocumentObjectGroupPython] G4_WATER  # scripted group (container) (typed FeaturePython)
  Dunit = g/cm3
  Dvalue = 1
  Group = -> [H_element110,O_element103]
  conduct = 2
  density = 1
  expand = 3
  formula = G4_WATER
  name = G4_WATER
  specific = 4
FEATURE [App::DocumentObjectGroupPython] H_element111  label="H_element : 060"  # scripted group (container) (typed FeaturePython)
  n = 2
  ref = H_element
FEATURE [App::DocumentObjectGroupPython] O_element104  label="O_element : 058"  # scripted group (container) (typed FeaturePython)
  n = 1
  ref = O_element
FEATURE [App::DocumentObjectGroupPython] G4_WATER_VAPOR  # scripted group (container) (typed FeaturePython)
  Dunit = g/cm3
  Dvalue = 0.000756182
  Group = -> [H_element111,O_element104]
  conduct = 2
  density = 1
  expand = 3
  formula = G4_WATER_VAPOR
  name = G4_WATER_VAPOR
  specific = 4
FEATURE [App::DocumentObjectGroupPython] C_element122  label="C_element : 068"  # scripted group (container) (typed FeaturePython)
  n = 8
  ref = C_element
FEATURE [App::DocumentObjectGroupPython] H_element112  label="H_element : 061"  # scripted group (container) (typed FeaturePython)
  n = 10
  ref = H_element
FEATURE [App::DocumentObjectGroupPython] G4_XYLENE  # scripted group (container) (typed FeaturePython)
  Dunit = g/cm3
  Dvalue = 0.87
  Group = -> [C_element122,H_element112]
  conduct = 2
  density = 1
  expand = 3
  formula = G4_XYLENE
  name = G4_XYLENE
  specific = 4
FEATURE [App::DocumentObjectGroupPython] C_element123  label="C_element : 069"  # scripted group (container) (typed FeaturePython)
  n = 1
  ref = C_element
FEATURE [App::DocumentObjectGroupPython] G4_GRAPHITE  # scripted group (container) (typed FeaturePython)
  Dunit = g/cm3
  Dvalue = 2.21
  Group = -> [C_element123]
  conduct = 2
  density = 1
  expand = 3
  formula = G4_GRAPHITE
  name = G4_GRAPHITE
  specific = 4
FEATURE [App::DocumentObjectGroupPython] NIST  # scripted group (container) (typed FeaturePython)
  Group = -> [G4_A_150_TISSUE,G4_ACETONE,G4_ACETYLENE,G4_ADENINE,G4_ADIPOSE_TISSUE_ICRP,G4_AIR,G4_ALANINE,G4_ALUMINUM_OXIDE,G4_AMBER,G4_AMMONIA,G4_ANILINE,G4_ANTHRACENE,G4_B_100_BONE,G4_BAKELITE,G4_BARIUM_FLUORIDE,G4_BARIUM_SULFATE,G4_BENZENE,G4_BERYLLIUM_OXIDE,G4_BGO,G4_BLOOD_ICRP,G4_BONE_COMPACT_ICRU,G4_BONE_CORTICAL_ICRP,G4_BORON_CARBIDE,G4_BORON_OXIDE,G4_BRAIN_ICRP,G4_BUTANE,G4_N_BUTYL_ALCOHOL,G4_C_552,+152 more]
FEATURE [App::DocumentObjectGroupPython] H_element113  label="H_element : 062"  # scripted group (container) (typed FeaturePython)
  n = 1
  ref = H_element
FEATURE [App::DocumentObjectGroupPython] G4_H  # scripted group (container) (typed FeaturePython)
  Dunit = g/cm3
  Dvalue = 8.3748e-05
  Group = -> [H_element113]
  conduct = 2
  density = 1
  expand = 3
  formula = H
  name = G4_H
  specific = 4
FEATURE [App::DocumentObjectGroupPython] He_element001  label="He_element : 1"  # scripted group (container) (typed FeaturePython)
  n = 1
  ref = He_element
FEATURE [App::DocumentObjectGroupPython] G4_He  # scripted group (container) (typed FeaturePython)
  Dunit = g/cm3
  Dvalue = 0.000166322
  Group = -> [He_element001]
  conduct = 2
  density = 1
  expand = 3
  formula = He
  name = G4_He
  specific = 4
FEATURE [App::DocumentObjectGroupPython] Li_element008  label="Li_element : 008"  # scripted group (container) (typed FeaturePython)
  n = 1
  ref = Li_element
FEATURE [App::DocumentObjectGroupPython] G4_Li  # scripted group (container) (typed FeaturePython)
  Dunit = g/cm3
  Dvalue = 0.534
  Group = -> [Li_element008]
  conduct = 2
  density = 1
  expand = 3
  formula = Li
  name = G4_Li
  specific = 4
FEATURE [App::DocumentObjectGroupPython] Be_element002  label="Be_element : 002"  # scripted group (container) (typed FeaturePython)
  n = 1
  ref = Be_element
FEATURE [App::DocumentObjectGroupPython] G4_Be  # scripted group (container) (typed FeaturePython)
  Dunit = g/cm3
  Dvalue = 1.848
  Group = -> [Be_element002]
  conduct = 2
  density = 1
  expand = 3
  formula = Be
  name = G4_Be
  specific = 4
FEATURE [App::DocumentObjectGroupPython] B_element007  label="B_element : 007"  # scripted group (container) (typed FeaturePython)
  n = 1
  ref = B_element
FEATURE [App::DocumentObjectGroupPython] G4_B  # scripted group (container) (typed FeaturePython)
  Dunit = g/cm3
  Dvalue = 2.37
  Group = -> [B_element007]
  conduct = 2
  density = 1
  expand = 3
  formula = B
  name = G4_B
  specific = 4
FEATURE [App::DocumentObjectGroupPython] C_element124  label="C_element : 070"  # scripted group (container) (typed FeaturePython)
  n = 1
  ref = C_element
FEATURE [App::DocumentObjectGroupPython] G4_C  # scripted group (container) (typed FeaturePython)
  Dunit = g/cm3
  Dvalue = 2
  Group = -> [C_element124]
  conduct = 2
  density = 1
  expand = 3
  formula = C
  name = G4_C
  specific = 4
FEATURE [App::DocumentObjectGroupPython] N_element048  label="N_element : 021"  # scripted group (container) (typed FeaturePython)
  n = 1
  ref = N_element
FEATURE [App::DocumentObjectGroupPython] G4_N  # scripted group (container) (typed FeaturePython)
  Dunit = g/cm3
  Dvalue = 0.0011652
  Group = -> [N_element048]
  conduct = 2
  density = 1
  expand = 3
  formula = N
  name = G4_N
  specific = 4
FEATURE [App::DocumentObjectGroupPython] O_element105  label="O_element : 059"  # scripted group (container) (typed FeaturePython)
  n = 1
  ref = O_element
FEATURE [App::DocumentObjectGroupPython] G4_O  # scripted group (container) (typed FeaturePython)
  Dunit = g/cm3
  Dvalue = 0.00133151
  Group = -> [O_element105]
  conduct = 2
  density = 1
  expand = 3
  formula = O
  name = G4_O
  specific = 4
FEATURE [App::DocumentObjectGroupPython] F_element019  label="F_element : 008"  # scripted group (container) (typed FeaturePython)
  n = 1
  ref = F_element
FEATURE [App::DocumentObjectGroupPython] G4_F  # scripted group (container) (typed FeaturePython)
  Dunit = g/cm3
  Dvalue = 0.00158029
  Group = -> [F_element019]
  conduct = 2
  density = 1
  expand = 3
  formula = F
  name = G4_F
  specific = 4
FEATURE [App::DocumentObjectGroupPython] Ne_element001  label="Ne_element : 1"  # scripted group (container) (typed FeaturePython)
  n = 1
  ref = Ne_element
FEATURE [App::DocumentObjectGroupPython] G4_Ne  # scripted group (container) (typed FeaturePython)
  Dunit = g/cm3
  Dvalue = 0.000838505
  Group = -> [Ne_element001]
  conduct = 2
  density = 1
  expand = 3
  formula = Ne
  name = G4_Ne
  specific = 4
FEATURE [App::DocumentObjectGroupPython] Na_element020  label="Na_element : 005"  # scripted group (container) (typed FeaturePython)
  n = 1
  ref = Na_element
FEATURE [App::DocumentObjectGroupPython] G4_Na  # scripted group (container) (typed FeaturePython)
  Dunit = g/cm3
  Dvalue = 0.971
  Group = -> [Na_element020]
  conduct = 2
  density = 1
  expand = 3
  formula = Na
  name = G4_Na
  specific = 4
FEATURE [App::DocumentObjectGroupPython] Mg_element011  label="Mg_element : 005"  # scripted group (container) (typed FeaturePython)
  n = 1
  ref = Mg_element
FEATURE [App::DocumentObjectGroupPython] G4_Mg  # scripted group (container) (typed FeaturePython)
  Dunit = g/cm3
  Dvalue = 1.74
  Group = -> [Mg_element011]
  conduct = 2
  density = 1
  expand = 3
  formula = Mg
  name = G4_Mg
  specific = 4
FEATURE [App::DocumentObjectGroupPython] Al_element004  label="Al_element : 1"  # scripted group (container) (typed FeaturePython)
  n = 1
  ref = Al_element
FEATURE [App::DocumentObjectGroupPython] G4_Al  # scripted group (container) (typed FeaturePython)
  Dunit = g/cm3
  Dvalue = 2.699
  Group = -> [Al_element004]
  conduct = 2
  density = 1
  expand = 3
  formula = Al
  name = G4_Al
  specific = 4
FEATURE [App::DocumentObjectGroupPython] Si_element007  label="Si_element : 002"  # scripted group (container) (typed FeaturePython)
  n = 1
  ref = Si_element
FEATURE [App::DocumentObjectGroupPython] G4_Si  # scripted group (container) (typed FeaturePython)
  Dunit = g/cm3
  Dvalue = 2.33
  Group = -> [Si_element007]
  conduct = 2
  density = 1
  expand = 3
  formula = Si
  name = G4_Si
  specific = 4
FEATURE [App::DocumentObjectGroupPython] P_element013  label="P_element : 002"  # scripted group (container) (typed FeaturePython)
  n = 1
  ref = P_element
FEATURE [App::DocumentObjectGroupPython] G4_P  # scripted group (container) (typed FeaturePython)
  Dunit = g/cm3
  Dvalue = 2.2
  Group = -> [P_element013]
  conduct = 2
  density = 1
  expand = 3
  formula = P
  name = G4_P
  specific = 4
FEATURE [App::DocumentObjectGroupPython] S_element023  label="S_element : 007"  # scripted group (container) (typed FeaturePython)
  n = 1
  ref = S_element
FEATURE [App::DocumentObjectGroupPython] G4_S  # scripted group (container) (typed FeaturePython)
  Dunit = g/cm3
  Dvalue = 2
  Group = -> [S_element023]
  conduct = 2
  density = 1
  expand = 3
  formula = S
  name = G4_S
  specific = 4
FEATURE [App::DocumentObjectGroupPython] Cl_element029  label="Cl_element : 015"  # scripted group (container) (typed FeaturePython)
  n = 1
  ref = Cl_element
FEATURE [App::DocumentObjectGroupPython] G4_Cl  # scripted group (container) (typed FeaturePython)
  Dunit = g/cm3
  Dvalue = 0.00299473
  Group = -> [Cl_element029]
  conduct = 2
  density = 1
  expand = 3
  formula = Cl
  name = G4_Cl
  specific = 4
FEATURE [App::DocumentObjectGroupPython] Ar_element002  label="Ar_element : 1"  # scripted group (container) (typed FeaturePython)
  n = 1
  ref = Ar_element
FEATURE [App::DocumentObjectGroupPython] G4_Ar  # scripted group (container) (typed FeaturePython)
  Dunit = g/cm3
  Dvalue = 0.00166201
  Group = -> [Ar_element002]
  conduct = 2
  density = 1
  expand = 3
  formula = Ar
  name = G4_Ar
  specific = 4
FEATURE [App::DocumentObjectGroupPython] K_element013  label="K_element : 003"  # scripted group (container) (typed FeaturePython)
  n = 1
  ref = K_element
FEATURE [App::DocumentObjectGroupPython] G4_K  # scripted group (container) (typed FeaturePython)
  Dunit = g/cm3
  Dvalue = 0.862
  Group = -> [K_element013]
  conduct = 2
  density = 1
  expand = 3
  formula = K
  name = G4_K
  specific = 4
FEATURE [App::DocumentObjectGroupPython] Ca_element014  label="Ca_element : 007"  # scripted group (container) (typed FeaturePython)
  n = 1
  ref = Ca_element
FEATURE [App::DocumentObjectGroupPython] G4_Ca  # scripted group (container) (typed FeaturePython)
  Dunit = g/cm3
  Dvalue = 1.55
  Group = -> [Ca_element014]
  conduct = 2
  density = 1
  expand = 3
  formula = Ca
  name = G4_Ca
  specific = 4
FEATURE [App::DocumentObjectGroupPython] Sc_element001  label="Sc_element : 1"  # scripted group (container) (typed FeaturePython)
  n = 1
  ref = Sc_element
FEATURE [App::DocumentObjectGroupPython] G4_Sc  # scripted group (container) (typed FeaturePython)
  Dunit = g/cm3
  Dvalue = 2.989
  Group = -> [Sc_element001]
  conduct = 2
  density = 1
  expand = 3
  formula = Sc
  name = G4_Sc
  specific = 4
FEATURE [App::DocumentObjectGroupPython] Ti_element004  label="Ti_element : 002"  # scripted group (container) (typed FeaturePython)
  n = 1
  ref = Ti_element
FEATURE [App::DocumentObjectGroupPython] G4_Ti  # scripted group (container) (typed FeaturePython)
  Dunit = g/cm3
  Dvalue = 4.54
  Group = -> [Ti_element004]
  conduct = 2
  density = 1
  expand = 3
  formula = Ti
  name = G4_Ti
  specific = 4
FEATURE [App::DocumentObjectGroupPython] V_element001  label="V_element : 1"  # scripted group (container) (typed FeaturePython)
  n = 1
  ref = V_element
FEATURE [App::DocumentObjectGroupPython] G4_V  # scripted group (container) (typed FeaturePython)
  Dunit = g/cm3
  Dvalue = 6.11
  Group = -> [V_element001]
  conduct = 2
  density = 1
  expand = 3
  formula = V
  name = G4_V
  specific = 4
FEATURE [App::DocumentObjectGroupPython] Cr_element001  label="Cr_element : 1"  # scripted group (container) (typed FeaturePython)
  n = 1
  ref = Cr_element
FEATURE [App::DocumentObjectGroupPython] G4_Cr  # scripted group (container) (typed FeaturePython)
  Dunit = g/cm3
  Dvalue = 7.18
  Group = -> [Cr_element001]
  conduct = 2
  density = 1
  expand = 3
  formula = Cr
  name = G4_Cr
  specific = 4
FEATURE [App::DocumentObjectGroupPython] Mn_element001  label="Mn_element : 1"  # scripted group (container) (typed FeaturePython)
  n = 1
  ref = Mn_element
FEATURE [App::DocumentObjectGroupPython] G4_Mn  # scripted group (container) (typed FeaturePython)
  Dunit = g/cm3
  Dvalue = 7.44
  Group = -> [Mn_element001]
  conduct = 2
  density = 1
  expand = 3
  formula = Mn
  name = G4_Mn
  specific = 4
FEATURE [App::DocumentObjectGroupPython] Fe_element007  label="Fe_element : 004"  # scripted group (container) (typed FeaturePython)
  n = 1
  ref = Fe_element
FEATURE [App::DocumentObjectGroupPython] G4_Fe  # scripted group (container) (typed FeaturePython)
  Dunit = g/cm3
  Dvalue = 7.874
  Group = -> [Fe_element007]
  conduct = 2
  density = 1
  expand = 3
  formula = Fe
  name = G4_Fe
  specific = 4
FEATURE [App::DocumentObjectGroupPython] Co_element001  label="Co_element : 1"  # scripted group (container) (typed FeaturePython)
  n = 1
  ref = Co_element
FEATURE [App::DocumentObjectGroupPython] G4_Co  # scripted group (container) (typed FeaturePython)
  Dunit = g/cm3
  Dvalue = 8.9
  Group = -> [Co_element001]
  conduct = 2
  density = 1
  expand = 3
  formula = Co
  name = G4_Co
  specific = 4
FEATURE [App::DocumentObjectGroupPython] Ni_element001  label="Ni_element : 1"  # scripted group (container) (typed FeaturePython)
  n = 1
  ref = Ni_element
FEATURE [App::DocumentObjectGroupPython] G4_Ni  # scripted group (container) (typed FeaturePython)
  Dunit = g/cm3
  Dvalue = 8.902
  Group = -> [Ni_element001]
  conduct = 2
  density = 1
  expand = 3
  formula = Ni
  name = G4_Ni
  specific = 4
FEATURE [App::DocumentObjectGroupPython] Cu_element001  label="Cu_element : 1"  # scripted group (container) (typed FeaturePython)
  n = 1
  ref = Cu_element
FEATURE [App::DocumentObjectGroupPython] G4_Cu  # scripted group (container) (typed FeaturePython)
  Dunit = g/cm3
  Dvalue = 8.96
  Group = -> [Cu_element001]
  conduct = 2
  density = 1
  expand = 3
  formula = Cu
  name = G4_Cu
  specific = 4
FEATURE [App::DocumentObjectGroupPython] Zn_element001  label="Zn_element : 1"  # scripted group (container) (typed FeaturePython)
  n = 1
  ref = Zn_element
FEATURE [App::DocumentObjectGroupPython] G4_Zn  # scripted group (container) (typed FeaturePython)
  Dunit = g/cm3
  Dvalue = 7.133
  Group = -> [Zn_element001]
  conduct = 2
  density = 1
  expand = 3
  formula = Zn
  name = G4_Zn
  specific = 4
FEATURE [App::DocumentObjectGroupPython] Ga_element002  label="Ga_element : 002"  # scripted group (container) (typed FeaturePython)
  n = 1
  ref = Ga_element
FEATURE [App::DocumentObjectGroupPython] G4_Ga  # scripted group (container) (typed FeaturePython)
  Dunit = g/cm3
  Dvalue = 5.904
  Group = -> [Ga_element002]
  conduct = 2
  density = 1
  expand = 3
  formula = Ga
  name = G4_Ga
  specific = 4
FEATURE [App::DocumentObjectGroupPython] Ge_element002  label="Ge_element : 1"  # scripted group (container) (typed FeaturePython)
  n = 1
  ref = Ge_element
FEATURE [App::DocumentObjectGroupPython] G4_Ge  # scripted group (container) (typed FeaturePython)
  Dunit = g/cm3
  Dvalue = 5.323
  Group = -> [Ge_element002]
  conduct = 2
  density = 1
  expand = 3
  formula = Ge
  name = G4_Ge
  specific = 4
FEATURE [App::DocumentObjectGroupPython] As_element003  label="As_element : 002"  # scripted group (container) (typed FeaturePython)
  n = 1
  ref = As_element
FEATURE [App::DocumentObjectGroupPython] G4_As  # scripted group (container) (typed FeaturePython)
  Dunit = g/cm3
  Dvalue = 5.73
  Group = -> [As_element003]
  conduct = 2
  density = 1
  expand = 3
  formula = As
  name = G4_As
  specific = 4
FEATURE [App::DocumentObjectGroupPython] Se_element001  label="Se_element : 1"  # scripted group (container) (typed FeaturePython)
  n = 1
  ref = Se_element
FEATURE [App::DocumentObjectGroupPython] G4_Se  # scripted group (container) (typed FeaturePython)
  Dunit = g/cm3
  Dvalue = 4.5
  Group = -> [Se_element001]
  conduct = 2
  density = 1
  expand = 3
  formula = Se
  name = G4_Se
  specific = 4
FEATURE [App::DocumentObjectGroupPython] Br_element007  label="Br_element : 004"  # scripted group (container) (typed FeaturePython)
  n = 1
  ref = Br_element
FEATURE [App::DocumentObjectGroupPython] G4_Br  # scripted group (container) (typed FeaturePython)
  Dunit = g/cm3
  Dvalue = 0.0070721
  Group = -> [Br_element007]
  conduct = 2
  density = 1
  expand = 3
  formula = Br
  name = G4_Br
  specific = 4
FEATURE [App::DocumentObjectGroupPython] Kr_element001  label="Kr_element : 1"  # scripted group (container) (typed FeaturePython)
  n = 1
  ref = Kr_element
FEATURE [App::DocumentObjectGroupPython] G4_Kr  # scripted group (container) (typed FeaturePython)
  Dunit = g/cm3
  Dvalue = 0.00347832
  Group = -> [Kr_element001]
  conduct = 2
  density = 1
  expand = 3
  formula = Kr
  name = G4_Kr
  specific = 4
FEATURE [App::DocumentObjectGroupPython] Rb_element001  label="Rb_element : 1"  # scripted group (container) (typed FeaturePython)
  n = 1
  ref = Rb_element
FEATURE [App::DocumentObjectGroupPython] G4_Rb  # scripted group (container) (typed FeaturePython)
  Dunit = g/cm3
  Dvalue = 1.532
  Group = -> [Rb_element001]
  conduct = 2
  density = 1
  expand = 3
  formula = Rb
  name = G4_Rb
  specific = 4
FEATURE [App::DocumentObjectGroupPython] Sr_element001  label="Sr_element : 1"  # scripted group (container) (typed FeaturePython)
  n = 1
  ref = Sr_element
FEATURE [App::DocumentObjectGroupPython] G4_Sr  # scripted group (container) (typed FeaturePython)
  Dunit = g/cm3
  Dvalue = 2.54
  Group = -> [Sr_element001]
  conduct = 2
  density = 1
  expand = 3
  formula = Sr
  name = G4_Sr
  specific = 4
FEATURE [App::DocumentObjectGroupPython] Y_element001  label="Y_element : 1"  # scripted group (container) (typed FeaturePython)
  n = 1
  ref = Y_element
FEATURE [App::DocumentObjectGroupPython] G4_Y  # scripted group (container) (typed FeaturePython)
  Dunit = g/cm3
  Dvalue = 4.469
  Group = -> [Y_element001]
  conduct = 2
  density = 1
  expand = 3
  formula = Y
  name = G4_Y
  specific = 4
FEATURE [App::DocumentObjectGroupPython] Zr_element001  label="Zr_element : 1"  # scripted group (container) (typed FeaturePython)
  n = 1
  ref = Zr_element
FEATURE [App::DocumentObjectGroupPython] G4_Zr  # scripted group (container) (typed FeaturePython)
  Dunit = g/cm3
  Dvalue = 6.506
  Group = -> [Zr_element001]
  conduct = 2
  density = 1
  expand = 3
  formula = Zr
  name = G4_Zr
  specific = 4
FEATURE [App::DocumentObjectGroupPython] Nb_element001  label="Nb_element : 1"  # scripted group (container) (typed FeaturePython)
  n = 1
  ref = Nb_element
FEATURE [App::DocumentObjectGroupPython] G4_Nb  # scripted group (container) (typed FeaturePython)
  Dunit = g/cm3
  Dvalue = 8.57
  Group = -> [Nb_element001]
  conduct = 2
  density = 1
  expand = 3
  formula = Nb
  name = G4_Nb
  specific = 4
FEATURE [App::DocumentObjectGroupPython] Mo_element001  label="Mo_element : 1"  # scripted group (container) (typed FeaturePython)
  n = 1
  ref = Mo_element
FEATURE [App::DocumentObjectGroupPython] G4_Mo  # scripted group (container) (typed FeaturePython)
  Dunit = g/cm3
  Dvalue = 10.22
  Group = -> [Mo_element001]
  conduct = 2
  density = 1
  expand = 3
  formula = Mo
  name = G4_Mo
  specific = 4
FEATURE [App::DocumentObjectGroupPython] Tc_element001  label="Tc_element : 1"  # scripted group (container) (typed FeaturePython)
  n = 1
  ref = Tc_element
FEATURE [App::DocumentObjectGroupPython] G4_Tc  # scripted group (container) (typed FeaturePython)
  Dunit = g/cm3
  Dvalue = 11.5
  Group = -> [Tc_element001]
  conduct = 2
  density = 1
  expand = 3
  formula = Tc
  name = G4_Tc
  specific = 4
FEATURE [App::DocumentObjectGroupPython] Ru_element001  label="Ru_element : 1"  # scripted group (container) (typed FeaturePython)
  n = 1
  ref = Ru_element
FEATURE [App::DocumentObjectGroupPython] G4_Ru  # scripted group (container) (typed FeaturePython)
  Dunit = g/cm3
  Dvalue = 12.41
  Group = -> [Ru_element001]
  conduct = 2
  density = 1
  expand = 3
  formula = Ru
  name = G4_Ru
  specific = 4
FEATURE [App::DocumentObjectGroupPython] Rh_element001  label="Rh_element : 1"  # scripted group (container) (typed FeaturePython)
  n = 1
  ref = Rh_element
FEATURE [App::DocumentObjectGroupPython] G4_Rh  # scripted group (container) (typed FeaturePython)
  Dunit = g/cm3
  Dvalue = 12.41
  Group = -> [Rh_element001]
  conduct = 2
  density = 1
  expand = 3
  formula = Rh
  name = G4_Rh
  specific = 4
FEATURE [App::DocumentObjectGroupPython] Pd_element001  label="Pd_element : 1"  # scripted group (container) (typed FeaturePython)
  n = 1
  ref = Pd_element
FEATURE [App::DocumentObjectGroupPython] G4_Pd  # scripted group (container) (typed FeaturePython)
  Dunit = g/cm3
  Dvalue = 12.02
  Group = -> [Pd_element001]
  conduct = 2
  density = 1
  expand = 3
  formula = Pd
  name = G4_Pd
  specific = 4
FEATURE [App::DocumentObjectGroupPython] Ag_element006  label="Ag_element : 004"  # scripted group (container) (typed FeaturePython)
  n = 1
  ref = Ag_element
FEATURE [App::DocumentObjectGroupPython] G4_Ag  # scripted group (container) (typed FeaturePython)
  Dunit = g/cm3
  Dvalue = 10.5
  Group = -> [Ag_element006]
  conduct = 2
  density = 1
  expand = 3
  formula = Ag
  name = G4_Ag
  specific = 4
FEATURE [App::DocumentObjectGroupPython] Cd_element003  label="Cd_element : 003"  # scripted group (container) (typed FeaturePython)
  n = 1
  ref = Cd_element
FEATURE [App::DocumentObjectGroupPython] G4_Cd  # scripted group (container) (typed FeaturePython)
  Dunit = g/cm3
  Dvalue = 8.65
  Group = -> [Cd_element003]
  conduct = 2
  density = 1
  expand = 3
  formula = Cd
  name = G4_Cd
  specific = 4
FEATURE [App::DocumentObjectGroupPython] In_element001  label="In_element : 1"  # scripted group (container) (typed FeaturePython)
  n = 1
  ref = In_element
FEATURE [App::DocumentObjectGroupPython] G4_In  # scripted group (container) (typed FeaturePython)
  Dunit = g/cm3
  Dvalue = 7.31
  Group = -> [In_element001]
  conduct = 2
  density = 1
  expand = 3
  formula = In
  name = G4_In
  specific = 4
FEATURE [App::DocumentObjectGroupPython] Sn_element001  label="Sn_element : 1"  # scripted group (container) (typed FeaturePython)
  n = 1
  ref = Sn_element
FEATURE [App::DocumentObjectGroupPython] G4_Sn  # scripted group (container) (typed FeaturePython)
  Dunit = g/cm3
  Dvalue = 7.31
  Group = -> [Sn_element001]
  conduct = 2
  density = 1
  expand = 3
  formula = Sn
  name = G4_Sn
  specific = 4
FEATURE [App::DocumentObjectGroupPython] Sb_element001  label="Sb_element : 1"  # scripted group (container) (typed FeaturePython)
  n = 1
  ref = Sb_element
FEATURE [App::DocumentObjectGroupPython] G4_Sb  # scripted group (container) (typed FeaturePython)
  Dunit = g/cm3
  Dvalue = 6.691
  Group = -> [Sb_element001]
  conduct = 2
  density = 1
  expand = 3
  formula = Sb
  name = G4_Sb
  specific = 4
FEATURE [App::DocumentObjectGroupPython] Te_element002  label="Te_element : 002"  # scripted group (container) (typed FeaturePython)
  n = 1
  ref = Te_element
FEATURE [App::DocumentObjectGroupPython] G4_Te  # scripted group (container) (typed FeaturePython)
  Dunit = g/cm3
  Dvalue = 6.24
  Group = -> [Te_element002]
  conduct = 2
  density = 1
  expand = 3
  formula = Te
  name = G4_Te
  specific = 4
FEATURE [App::DocumentObjectGroupPython] I_element010  label="I_element : 006"  # scripted group (container) (typed FeaturePython)
  n = 1
  ref = I_element
FEATURE [App::DocumentObjectGroupPython] G4_I  # scripted group (container) (typed FeaturePython)
  Dunit = g/cm3
  Dvalue = 4.93
  Group = -> [I_element010]
  conduct = 2
  density = 1
  expand = 3
  formula = I
  name = G4_I
  specific = 4
FEATURE [App::DocumentObjectGroupPython] Xe_element001  label="Xe_element : 1"  # scripted group (container) (typed FeaturePython)
  n = 1
  ref = Xe_element
FEATURE [App::DocumentObjectGroupPython] G4_Xe  # scripted group (container) (typed FeaturePython)
  Dunit = g/cm3
  Dvalue = 0.00548536
  Group = -> [Xe_element001]
  conduct = 2
  density = 1
  expand = 3
  formula = Xe
  name = G4_Xe
  specific = 4
FEATURE [App::DocumentObjectGroupPython] Cs_element003  label="Cs_element : 003"  # scripted group (container) (typed FeaturePython)
  n = 1
  ref = Cs_element
FEATURE [App::DocumentObjectGroupPython] G4_Cs  # scripted group (container) (typed FeaturePython)
  Dunit = g/cm3
  Dvalue = 1.873
  Group = -> [Cs_element003]
  conduct = 2
  density = 1
  expand = 3
  formula = Cs
  name = G4_Cs
  specific = 4
FEATURE [App::DocumentObjectGroupPython] Ba_element003  label="Ba_element : 003"  # scripted group (container) (typed FeaturePython)
  n = 1
  ref = Ba_element
FEATURE [App::DocumentObjectGroupPython] G4_Ba  # scripted group (container) (typed FeaturePython)
  Dunit = g/cm3
  Dvalue = 3.5
  Group = -> [Ba_element003]
  conduct = 2
  density = 1
  expand = 3
  formula = Ba
  name = G4_Ba
  specific = 4
FEATURE [App::DocumentObjectGroupPython] La_element003  label="La_element : 003"  # scripted group (container) (typed FeaturePython)
  n = 1
  ref = La_element
FEATURE [App::DocumentObjectGroupPython] G4_La  # scripted group (container) (typed FeaturePython)
  Dunit = g/cm3
  Dvalue = 6.154
  Group = -> [La_element003]
  conduct = 2
  density = 1
  expand = 3
  formula = La
  name = G4_La
  specific = 4
FEATURE [App::DocumentObjectGroupPython] Ce_element002  label="Ce_element : 1"  # scripted group (container) (typed FeaturePython)
  n = 1
  ref = Ce_element
FEATURE [App::DocumentObjectGroupPython] G4_Ce  # scripted group (container) (typed FeaturePython)
  Dunit = g/cm3
  Dvalue = 6.657
  Group = -> [Ce_element002]
  conduct = 2
  density = 1
  expand = 3
  formula = Ce
  name = G4_Ce
  specific = 4
FEATURE [App::DocumentObjectGroupPython] Pr_element001  label="Pr_element : 1"  # scripted group (container) (typed FeaturePython)
  n = 1
  ref = Pr_element
FEATURE [App::DocumentObjectGroupPython] G4_Pr  # scripted group (container) (typed FeaturePython)
  Dunit = g/cm3
  Dvalue = 6.71
  Group = -> [Pr_element001]
  conduct = 2
  density = 1
  expand = 3
  formula = Pr
  name = G4_Pr
  specific = 4
FEATURE [App::DocumentObjectGroupPython] Nd_element001  label="Nd_element : 1"  # scripted group (container) (typed FeaturePython)
  n = 1
  ref = Nd_element
FEATURE [App::DocumentObjectGroupPython] G4_Nd  # scripted group (container) (typed FeaturePython)
  Dunit = g/cm3
  Dvalue = 6.9
  Group = -> [Nd_element001]
  conduct = 2
  density = 1
  expand = 3
  formula = Nd
  name = G4_Nd
  specific = 4
FEATURE [App::DocumentObjectGroupPython] Pm_element001  label="Pm_element : 1"  # scripted group (container) (typed FeaturePython)
  n = 1
  ref = Pm_element
FEATURE [App::DocumentObjectGroupPython] G4_Pm  # scripted group (container) (typed FeaturePython)
  Dunit = g/cm3
  Dvalue = 7.22
  Group = -> [Pm_element001]
  conduct = 2
  density = 1
  expand = 3
  formula = Pm
  name = G4_Pm
  specific = 4
FEATURE [App::DocumentObjectGroupPython] Sm_element001  label="Sm_element : 1"  # scripted group (container) (typed FeaturePython)
  n = 1
  ref = Sm_element
FEATURE [App::DocumentObjectGroupPython] G4_Sm  # scripted group (container) (typed FeaturePython)
  Dunit = g/cm3
  Dvalue = 7.46
  Group = -> [Sm_element001]
  conduct = 2
  density = 1
  expand = 3
  formula = Sm
  name = G4_Sm
  specific = 4
FEATURE [App::DocumentObjectGroupPython] Eu_element001  label="Eu_element : 1"  # scripted group (container) (typed FeaturePython)
  n = 1
  ref = Eu_element
FEATURE [App::DocumentObjectGroupPython] G4_Eu  # scripted group (container) (typed FeaturePython)
  Dunit = g/cm3
  Dvalue = 5.243
  Group = -> [Eu_element001]
  conduct = 2
  density = 1
  expand = 3
  formula = Eu
  name = G4_Eu
  specific = 4
FEATURE [App::DocumentObjectGroupPython] Gd_element002  label="Gd_element : 1"  # scripted group (container) (typed FeaturePython)
  n = 1
  ref = Gd_element
FEATURE [App::DocumentObjectGroupPython] G4_Gd  # scripted group (container) (typed FeaturePython)
  Dunit = g/cm3
  Dvalue = 7.9004
  Group = -> [Gd_element002]
  conduct = 2
  density = 1
  expand = 3
  formula = Gd
  name = G4_Gd
  specific = 4
FEATURE [App::DocumentObjectGroupPython] Tb_element001  label="Tb_element : 1"  # scripted group (container) (typed FeaturePython)
  n = 1
  ref = Tb_element
FEATURE [App::DocumentObjectGroupPython] G4_Tb  # scripted group (container) (typed FeaturePython)
  Dunit = g/cm3
  Dvalue = 8.229
  Group = -> [Tb_element001]
  conduct = 2
  density = 1
  expand = 3
  formula = Tb
  name = G4_Tb
  specific = 4
FEATURE [App::DocumentObjectGroupPython] Dy_element001  label="Dy_element : 1"  # scripted group (container) (typed FeaturePython)
  n = 1
  ref = Dy_element
FEATURE [App::DocumentObjectGroupPython] G4_Dy  # scripted group (container) (typed FeaturePython)
  Dunit = g/cm3
  Dvalue = 8.55
  Group = -> [Dy_element001]
  conduct = 2
  density = 1
  expand = 3
  formula = Dy
  name = G4_Dy
  specific = 4
FEATURE [App::DocumentObjectGroupPython] Ho_element001  label="Ho_element : 1"  # scripted group (container) (typed FeaturePython)
  n = 1
  ref = Ho_element
FEATURE [App::DocumentObjectGroupPython] G4_Ho  # scripted group (container) (typed FeaturePython)
  Dunit = g/cm3
  Dvalue = 8.795
  Group = -> [Ho_element001]
  conduct = 2
  density = 1
  expand = 3
  formula = Ho
  name = G4_Ho
  specific = 4
FEATURE [App::DocumentObjectGroupPython] Er_element001  label="Er_element : 1"  # scripted group (container) (typed FeaturePython)
  n = 1
  ref = Er_element
FEATURE [App::DocumentObjectGroupPython] G4_Er  # scripted group (container) (typed FeaturePython)
  Dunit = g/cm3
  Dvalue = 9.066
  Group = -> [Er_element001]
  conduct = 2
  density = 1
  expand = 3
  formula = Er
  name = G4_Er
  specific = 4
FEATURE [App::DocumentObjectGroupPython] Tm_element001  label="Tm_element : 1"  # scripted group (container) (typed FeaturePython)
  n = 1
  ref = Tm_element
FEATURE [App::DocumentObjectGroupPython] G4_Tm  # scripted group (container) (typed FeaturePython)
  Dunit = g/cm3
  Dvalue = 9.321
  Group = -> [Tm_element001]
  conduct = 2
  density = 1
  expand = 3
  formula = Tm
  name = G4_Tm
  specific = 4
FEATURE [App::DocumentObjectGroupPython] Yb_element001  label="Yb_element : 1"  # scripted group (container) (typed FeaturePython)
  n = 1
  ref = Yb_element
FEATURE [App::DocumentObjectGroupPython] G4_Yb  # scripted group (container) (typed FeaturePython)
  Dunit = g/cm3
  Dvalue = 6.73
  Group = -> [Yb_element001]
  conduct = 2
  density = 1
  expand = 3
  formula = Yb
  name = G4_Yb
  specific = 4
FEATURE [App::DocumentObjectGroupPython] Lu_element001  label="Lu_element : 1"  # scripted group (container) (typed FeaturePython)
  n = 1
  ref = Lu_element
FEATURE [App::DocumentObjectGroupPython] G4_Lu  # scripted group (container) (typed FeaturePython)
  Dunit = g/cm3
  Dvalue = 9.84
  Group = -> [Lu_element001]
  conduct = 2
  density = 1
  expand = 3
  formula = Lu
  name = G4_Lu
  specific = 4
FEATURE [App::DocumentObjectGroupPython] Hf_element001  label="Hf_element : 1"  # scripted group (container) (typed FeaturePython)
  n = 1
  ref = Hf_element
FEATURE [App::DocumentObjectGroupPython] G4_Hf  # scripted group (container) (typed FeaturePython)
  Dunit = g/cm3
  Dvalue = 13.31
  Group = -> [Hf_element001]
  conduct = 2
  density = 1
  expand = 3
  formula = Hf
  name = G4_Hf
  specific = 4
FEATURE [App::DocumentObjectGroupPython] Ta_element001  label="Ta_element : 1"  # scripted group (container) (typed FeaturePython)
  n = 1
  ref = Ta_element
FEATURE [App::DocumentObjectGroupPython] G4_Ta  # scripted group (container) (typed FeaturePython)
  Dunit = g/cm3
  Dvalue = 16.654
  Group = -> [Ta_element001]
  conduct = 2
  density = 1
  expand = 3
  formula = Ta
  name = G4_Ta
  specific = 4
FEATURE [App::DocumentObjectGroupPython] W_element004  label="W_element : 004"  # scripted group (container) (typed FeaturePython)
  n = 1
  ref = W_element
FEATURE [App::DocumentObjectGroupPython] G4_W  # scripted group (container) (typed FeaturePython)
  Dunit = g/cm3
  Dvalue = 19.3
  Group = -> [W_element004]
  conduct = 2
  density = 1
  expand = 3
  formula = W
  name = G4_W
  specific = 4
FEATURE [App::DocumentObjectGroupPython] Re_element001  label="Re_element : 1"  # scripted group (container) (typed FeaturePython)
  n = 1
  ref = Re_element
FEATURE [App::DocumentObjectGroupPython] G4_Re  # scripted group (container) (typed FeaturePython)
  Dunit = g/cm3
  Dvalue = 21.02
  Group = -> [Re_element001]
  conduct = 2
  density = 1
  expand = 3
  formula = Re
  name = G4_Re
  specific = 4
FEATURE [App::DocumentObjectGroupPython] Os_element001  label="Os_element : 1"  # scripted group (container) (typed FeaturePython)
  n = 1
  ref = Os_element
FEATURE [App::DocumentObjectGroupPython] G4_Os  # scripted group (container) (typed FeaturePython)
  Dunit = g/cm3
  Dvalue = 22.57
  Group = -> [Os_element001]
  conduct = 2
  density = 1
  expand = 3
  formula = Os
  name = G4_Os
  specific = 4
FEATURE [App::DocumentObjectGroupPython] Ir_element001  label="Ir_element : 1"  # scripted group (container) (typed FeaturePython)
  n = 1
  ref = Ir_element
FEATURE [App::DocumentObjectGroupPython] G4_Ir  # scripted group (container) (typed FeaturePython)
  Dunit = g/cm3
  Dvalue = 22.42
  Group = -> [Ir_element001]
  conduct = 2
  density = 1
  expand = 3
  formula = Ir
  name = G4_Ir
  specific = 4
FEATURE [App::DocumentObjectGroupPython] Pt_element001  label="Pt_element : 1"  # scripted group (container) (typed FeaturePython)
  n = 1
  ref = Pt_element
FEATURE [App::DocumentObjectGroupPython] G4_Pt  # scripted group (container) (typed FeaturePython)
  Dunit = g/cm3
  Dvalue = 21.45
  Group = -> [Pt_element001]
  conduct = 2
  density = 1
  expand = 3
  formula = Pt
  name = G4_Pt
  specific = 4
FEATURE [App::DocumentObjectGroupPython] Au_element001  label="Au_element : 1"  # scripted group (container) (typed FeaturePython)
  n = 1
  ref = Au_element
FEATURE [App::DocumentObjectGroupPython] G4_Au  # scripted group (container) (typed FeaturePython)
  Dunit = g/cm3
  Dvalue = 19.32
  Group = -> [Au_element001]
  conduct = 2
  density = 1
  expand = 3
  formula = Au
  name = G4_Au
  specific = 4
FEATURE [App::DocumentObjectGroupPython] Hg_element002  label="Hg_element : 002"  # scripted group (container) (typed FeaturePython)
  n = 1
  ref = Hg_element
FEATURE [App::DocumentObjectGroupPython] G4_Hg  # scripted group (container) (typed FeaturePython)
  Dunit = g/cm3
  Dvalue = 13.546
  Group = -> [Hg_element002]
  conduct = 2
  density = 1
  expand = 3
  formula = Hg
  name = G4_Hg
  specific = 4
FEATURE [App::DocumentObjectGroupPython] Tl_element002  label="Tl_element : 002"  # scripted group (container) (typed FeaturePython)
  n = 1
  ref = Tl_element
FEATURE [App::DocumentObjectGroupPython] G4_Tl  # scripted group (container) (typed FeaturePython)
  Dunit = g/cm3
  Dvalue = 11.72
  Group = -> [Tl_element002]
  conduct = 2
  density = 1
  expand = 3
  formula = Tl
  name = G4_Tl
  specific = 4
FEATURE [App::DocumentObjectGroupPython] Pb_element003  label="Pb_element : 1"  # scripted group (container) (typed FeaturePython)
  n = 1
  ref = Pb_element
FEATURE [App::DocumentObjectGroupPython] G4_Pb  # scripted group (container) (typed FeaturePython)
  Dunit = g/cm3
  Dvalue = 11.35
  Group = -> [Pb_element003]
  conduct = 2
  density = 1
  expand = 3
  formula = Pb
  name = G4_Pb
  specific = 4
FEATURE [App::DocumentObjectGroupPython] Bi_element002  label="Bi_element : 1"  # scripted group (container) (typed FeaturePython)
  n = 1
  ref = Bi_element
FEATURE [App::DocumentObjectGroupPython] G4_Bi  # scripted group (container) (typed FeaturePython)
  Dunit = g/cm3
  Dvalue = 9.747
  Group = -> [Bi_element002]
  conduct = 2
  density = 1
  expand = 3
  formula = Bi
  name = G4_Bi
  specific = 4
FEATURE [App::DocumentObjectGroupPython] Po_element001  label="Po_element : 1"  # scripted group (container) (typed FeaturePython)
  n = 1
  ref = Po_element
FEATURE [App::DocumentObjectGroupPython] G4_Po  # scripted group (container) (typed FeaturePython)
  Dunit = g/cm3
  Dvalue = 9.32
  Group = -> [Po_element001]
  conduct = 2
  density = 1
  expand = 3
  formula = Po
  name = G4_Po
  specific = 4
FEATURE [App::DocumentObjectGroupPython] At_element001  label="At_element : 1"  # scripted group (container) (typed FeaturePython)
  n = 1
  ref = At_element
FEATURE [App::DocumentObjectGroupPython] G4_At  # scripted group (container) (typed FeaturePython)
  Dunit = g/cm3
  Dvalue = 9.32
  Group = -> [At_element001]
  conduct = 2
  density = 1
  expand = 3
  formula = At
  name = G4_At
  specific = 4
FEATURE [App::DocumentObjectGroupPython] Rn_element001  label="Rn_element : 1"  # scripted group (container) (typed FeaturePython)
  n = 1
  ref = Rn_element
FEATURE [App::DocumentObjectGroupPython] G4_Rn  # scripted group (container) (typed FeaturePython)
  Dunit = g/cm3
  Dvalue = 0.00900662
  Group = -> [Rn_element001]
  conduct = 2
  density = 1
  expand = 3
  formula = Rn
  name = G4_Rn
  specific = 4
FEATURE [App::DocumentObjectGroupPython] Fr_element001  label="Fr_element : 1"  # scripted group (container) (typed FeaturePython)
  n = 1
  ref = Fr_element
FEATURE [App::DocumentObjectGroupPython] G4_Fr  # scripted group (container) (typed FeaturePython)
  Dunit = g/cm3
  Dvalue = 1
  Group = -> [Fr_element001]
  conduct = 2
  density = 1
  expand = 3
  formula = Fr
  name = G4_Fr
  specific = 4
FEATURE [App::DocumentObjectGroupPython] Ra_element001  label="Ra_element : 1"  # scripted group (container) (typed FeaturePython)
  n = 1
  ref = Ra_element
FEATURE [App::DocumentObjectGroupPython] G4_Ra  # scripted group (container) (typed FeaturePython)
  Dunit = g/cm3
  Dvalue = 5
  Group = -> [Ra_element001]
  conduct = 2
  density = 1
  expand = 3
  formula = Ra
  name = G4_Ra
  specific = 4
FEATURE [App::DocumentObjectGroupPython] Ac_element001  label="Ac_element : 1"  # scripted group (container) (typed FeaturePython)
  n = 1
  ref = Ac_element
FEATURE [App::DocumentObjectGroupPython] G4_Ac  # scripted group (container) (typed FeaturePython)
  Dunit = g/cm3
  Dvalue = 10.07
  Group = -> [Ac_element001]
  conduct = 2
  density = 1
  expand = 3
  formula = Ac
  name = G4_Ac
  specific = 4
FEATURE [App::DocumentObjectGroupPython] Th_element001  label="Th_element : 1"  # scripted group (container) (typed FeaturePython)
  n = 1
  ref = Th_element
FEATURE [App::DocumentObjectGroupPython] G4_Th  # scripted group (container) (typed FeaturePython)
  Dunit = g/cm3
  Dvalue = 11.72
  Group = -> [Th_element001]
  conduct = 2
  density = 1
  expand = 3
  formula = Th
  name = G4_Th
  specific = 4
FEATURE [App::DocumentObjectGroupPython] Pa_element001  label="Pa_element : 1"  # scripted group (container) (typed FeaturePython)
  n = 1
  ref = Pa_element
FEATURE [App::DocumentObjectGroupPython] G4_Pa  # scripted group (container) (typed FeaturePython)
  Dunit = g/cm3
  Dvalue = 15.37
  Group = -> [Pa_element001]
  conduct = 2
  density = 1
  expand = 3
  formula = Pa
  name = G4_Pa
  specific = 4
FEATURE [App::DocumentObjectGroupPython] U_element004  label="U_element : 004"  # scripted group (container) (typed FeaturePython)
  n = 1
  ref = U_element
FEATURE [App::DocumentObjectGroupPython] G4_U  # scripted group (container) (typed FeaturePython)
  Dunit = g/cm3
  Dvalue = 18.95
  Group = -> [U_element004]
  conduct = 2
  density = 1
  expand = 3
  formula = U
  name = G4_U
  specific = 4
FEATURE [App::DocumentObjectGroupPython] Np_element001  label="Np_element : 1"  # scripted group (container) (typed FeaturePython)
  n = 1
  ref = Np_element
FEATURE [App::DocumentObjectGroupPython] G4_Np  # scripted group (container) (typed FeaturePython)
  Dunit = g/cm3
  Dvalue = 20.25
  Group = -> [Np_element001]
  conduct = 2
  density = 1
  expand = 3
  formula = Np
  name = G4_Np
  specific = 4
FEATURE [App::DocumentObjectGroupPython] Pu_element002  label="Pu_element : 002"  # scripted group (container) (typed FeaturePython)
  n = 1
  ref = Pu_element
FEATURE [App::DocumentObjectGroupPython] G4_Pu  # scripted group (container) (typed FeaturePython)
  Dunit = g/cm3
  Dvalue = 19.84
  Group = -> [Pu_element002]
  conduct = 2
  density = 1
  expand = 3
  formula = Pu
  name = G4_Pu
  specific = 4
FEATURE [App::DocumentObjectGroupPython] Am_element001  label="Am_element : 1"  # scripted group (container) (typed FeaturePython)
  n = 1
  ref = Am_element
FEATURE [App::DocumentObjectGroupPython] G4_Am  # scripted group (container) (typed FeaturePython)
  Dunit = g/cm3
  Dvalue = 13.67
  Group = -> [Am_element001]
  conduct = 2
  density = 1
  expand = 3
  formula = Am
  name = G4_Am
  specific = 4
FEATURE [App::DocumentObjectGroupPython] Cm_element001  label="Cm_element : 1"  # scripted group (container) (typed FeaturePython)
  n = 1
  ref = Cm_element
FEATURE [App::DocumentObjectGroupPython] G4_Cm  # scripted group (container) (typed FeaturePython)
  Dunit = g/cm3
  Dvalue = 13.51
  Group = -> [Cm_element001]
  conduct = 2
  density = 1
  expand = 3
  formula = Cm
  name = G4_Cm
  specific = 4
FEATURE [App::DocumentObjectGroupPython] Bk_element001  label="Bk_element : 1"  # scripted group (container) (typed FeaturePython)
  n = 1
  ref = Bk_element
FEATURE [App::DocumentObjectGroupPython] G4_Bk  # scripted group (container) (typed FeaturePython)
  Dunit = g/cm3
  Dvalue = 14
  Group = -> [Bk_element001]
  conduct = 2
  density = 1
  expand = 3
  formula = Bk
  name = G4_Bk
  specific = 4
FEATURE [App::DocumentObjectGroupPython] Cf_element001  label="Cf_element : 1"  # scripted group (container) (typed FeaturePython)
  n = 1
  ref = Cf_element
FEATURE [App::DocumentObjectGroupPython] G4_Cf  # scripted group (container) (typed FeaturePython)
  Dunit = g/cm3
  Dvalue = 10
  Group = -> [Cf_element001]
  conduct = 2
  density = 1
  expand = 3
  formula = Cf
  name = G4_Cf
  specific = 4
FEATURE [App::DocumentObjectGroupPython] Element  # scripted group (container) (typed FeaturePython)
  Group = -> [G4_H,G4_He,G4_Li,G4_Be,G4_B,G4_C,G4_N,G4_O,G4_F,G4_Ne,G4_Na,G4_Mg,G4_Al,G4_Si,G4_P,G4_S,G4_Cl,G4_Ar,G4_K,G4_Ca,G4_Sc,G4_Ti,G4_V,G4_Cr,G4_Mn,G4_Fe,G4_Co,G4_Ni,G4_Cu,G4_Zn,G4_Ga,G4_Ge,G4_As,G4_Se,G4_Br,G4_Kr,G4_Rb,G4_Sr,G4_Y,G4_Zr,G4_Nb,G4_Mo,G4_Tc,G4_Ru,G4_Rh,G4_Pd,G4_Ag,G4_Cd,G4_In,G4_Sn,G4_Sb,G4_Te,G4_I,G4_Xe,G4_Cs,G4_Ba,G4_La,G4_Ce,G4_Pr,G4_Nd,G4_Pm,G4_Sm,G4_Eu,G4_Gd,G4_Tb,G4_Dy,G4_Ho,G4_Er,+30 more]
FEATURE [App::DocumentObjectGroupPython] H_element114  label="H_element : 063"  # scripted group (container) (typed FeaturePython)
  n = 2
  ref = H_element
FEATURE [App::DocumentObjectGroupPython] G4_lH2  # scripted group (container) (typed FeaturePython)
  Dunit = g/cm3
  Dvalue = 0.0708
  Group = -> [H_element114]
  conduct = 2
  density = 1
  expand = 3
  formula = G4_lH2
  name = G4_lH2
  specific = 4
FEATURE [App::DocumentObjectGroupPython] N_element049  label="N_element : 022"  # scripted group (container) (typed FeaturePython)
  n = 2
  ref = N_element
FEATURE [App::DocumentObjectGroupPython] G4_lN2  # scripted group (container) (typed FeaturePython)
  Dunit = g/cm3
  Dvalue = 0.807
  Group = -> [N_element049]
  conduct = 2
  density = 1
  expand = 3
  formula = G4_lN2
  name = G4_lN2
  specific = 4
FEATURE [App::DocumentObjectGroupPython] O_element106  label="O_element : 060"  # scripted group (container) (typed FeaturePython)
  n = 2
  ref = O_element
FEATURE [App::DocumentObjectGroupPython] G4_lO2  # scripted group (container) (typed FeaturePython)
  Dunit = g/cm3
  Dvalue = 1.141
  Group = -> [O_element106]
  conduct = 2
  density = 1
  expand = 3
  formula = G4_lO2
  name = G4_lO2
  specific = 4
FEATURE [App::DocumentObjectGroupPython] Ar  label="Ar : 1"  # scripted group (container) (typed FeaturePython)
  n = 1
  ref = Ar
FEATURE [App::DocumentObjectGroupPython] G4_lAr  # scripted group (container) (typed FeaturePython)
  Dunit = g/cm3
  Dvalue = 1.396
  Group = -> [Ar]
  conduct = 2
  density = 1
  expand = 3
  formula = G4_lAr
  name = G4_lAr
  specific = 4
FEATURE [App::DocumentObjectGroupPython] Br  label="Br : 1"  # scripted group (container) (typed FeaturePython)
  n = 1
  ref = Br
FEATURE [App::DocumentObjectGroupPython] G4_lBr  # scripted group (container) (typed FeaturePython)
  Dunit = g/cm3
  Dvalue = 3.1028
  Group = -> [Br]
  conduct = 2
  density = 1
  expand = 3
  formula = G4_lBr
  name = G4_lBr
  specific = 4
FEATURE [App::DocumentObjectGroupPython] Kr  label="Kr : 1"  # scripted group (container) (typed FeaturePython)
  n = 1
  ref = Kr
FEATURE [App::DocumentObjectGroupPython] G4_lKr  # scripted group (container) (typed FeaturePython)
  Dunit = g/cm3
  Dvalue = 2.418
  Group = -> [Kr]
  conduct = 2
  density = 1
  expand = 3
  formula = G4_lKr
  name = G4_lKr
  specific = 4
FEATURE [App::DocumentObjectGroupPython] Xe  label="Xe : 1"  # scripted group (container) (typed FeaturePython)
  n = 1
  ref = Xe
FEATURE [App::DocumentObjectGroupPython] G4_lXe  # scripted group (container) (typed FeaturePython)
  Dunit = g/cm3
  Dvalue = 2.953
  Group = -> [Xe]
  conduct = 2
  density = 1
  expand = 3
  formula = G4_lXe
  name = G4_lXe
  specific = 4
FEATURE [App::DocumentObjectGroupPython] O_element107  label="O_element : 061"  # scripted group (container) (typed FeaturePython)
  n = 4
  ref = O_element
FEATURE [App::DocumentObjectGroupPython] Pb_element004  label="Pb_element : 002"  # scripted group (container) (typed FeaturePython)
  n = 1
  ref = Pb_element
FEATURE [App::DocumentObjectGroupPython] W_element005  label="W_element : 005"  # scripted group (container) (typed FeaturePython)
  n = 1
  ref = W_element
FEATURE [App::DocumentObjectGroupPython] G4_PbWO4  # scripted group (container) (typed FeaturePython)
  Dunit = g/cm3
  Dvalue = 8.28
  Group = -> [O_element107,Pb_element004,W_element005]
  conduct = 2
  density = 1
  expand = 3
  formula = G4_PbWO4
  name = G4_PbWO4
  specific = 4
FEATURE [App::DocumentObjectGroupPython] alactic  label="alactic : 1"  # scripted group (container) (typed FeaturePython)
  n = 1
  ref = alactic
FEATURE [App::DocumentObjectGroupPython] G4_Galactic  # scripted group (container) (typed FeaturePython)
  Dunit = g/cm3
  Dvalue = 0
  Group = -> [alactic]
  conduct = 2
  density = 1
  expand = 3
  formula = G4_Galactic
  name = G4_Galactic
  specific = 4
FEATURE [App::DocumentObjectGroupPython] RAPHITE_POROUS  label="RAPHITE_POROUS : 1"  # scripted group (container) (typed FeaturePython)
  n = 1
  ref = RAPHITE_POROUS
FEATURE [App::DocumentObjectGroupPython] G4_GRAPHITE_POROUS  # scripted group (container) (typed FeaturePython)
  Dunit = g/cm3
  Dvalue = 1.7
  Group = -> [RAPHITE_POROUS]
  conduct = 2
  density = 1
  expand = 3
  formula = G4_GRAPHITE_POROUS
  name = G4_GRAPHITE_POROUS
  specific = 4
FEATURE [App::DocumentObjectGroupPython] H_element115  label="H_element : 0.150"  # scripted group (container) (typed FeaturePython)
  n = 0.080538
FEATURE [App::DocumentObjectGroupPython] C_element125  label="C_element : 0.600"  # scripted group (container) (typed FeaturePython)
  n = 0.599848
FEATURE [App::DocumentObjectGroupPython] O_element108  label="O_element : 0.320"  # scripted group (container) (typed FeaturePython)
  n = 0.319614
FEATURE [App::DocumentObjectGroupPython] G4_LUCITE  # scripted group (container) (typed FeaturePython)
  Dunit = g/cm3
  Dvalue = 1.19
  Group = -> [H_element115,C_element125,O_element108]
  conduct = 2
  density = 1
  expand = 3
  formula = G4_LUCITE
  name = G4_LUCITE
  specific = 4
FEATURE [App::DocumentObjectGroupPython] Cu_element002  label="Cu_element : 62"  # scripted group (container) (typed FeaturePython)
  n = 62
  ref = Cu_element
FEATURE [App::DocumentObjectGroupPython] Zn_element002  label="Zn_element : 35"  # scripted group (container) (typed FeaturePython)
  n = 35
  ref = Zn_element
FEATURE [App::DocumentObjectGroupPython] Pb_element005  label="Pb_element : 3"  # scripted group (container) (typed FeaturePython)
  n = 3
  ref = Pb_element
FEATURE [App::DocumentObjectGroupPython] G4_BRASS  # scripted group (container) (typed FeaturePython)
  Dunit = g/cm3
  Dvalue = 8.52
  Group = -> [Cu_element002,Zn_element002,Pb_element005]
  conduct = 2
  density = 1
  expand = 3
  formula = G4_BRASS
  name = G4_BRASS
  specific = 4
FEATURE [App::DocumentObjectGroupPython] Cu_element003  label="Cu_element : 89"  # scripted group (container) (typed FeaturePython)
  n = 89
  ref = Cu_element
FEATURE [App::DocumentObjectGroupPython] Zn_element003  label="Zn_element : 9"  # scripted group (container) (typed FeaturePython)
  n = 9
  ref = Zn_element
FEATURE [App::DocumentObjectGroupPython] Pb_element006  label="Pb_element : 2"  # scripted group (container) (typed FeaturePython)
  n = 2
  ref = Pb_element
FEATURE [App::DocumentObjectGroupPython] G4_BRONZE  # scripted group (container) (typed FeaturePython)
  Dunit = g/cm3
  Dvalue = 8.82
  Group = -> [Cu_element003,Zn_element003,Pb_element006]
  conduct = 2
  density = 1
  expand = 3
  formula = G4_BRONZE
  name = G4_BRONZE
  specific = 4
FEATURE [App::DocumentObjectGroupPython] Fe_element008  label="Fe_element : 74"  # scripted group (container) (typed FeaturePython)
  n = 74
  ref = Fe_element
FEATURE [App::DocumentObjectGroupPython] Cr_element002  label="Cr_element : 18"  # scripted group (container) (typed FeaturePython)
  n = 18
  ref = Cr_element
FEATURE [App::DocumentObjectGroupPython] Ni_element002  label="Ni_element : 8"  # scripted group (container) (typed FeaturePython)
  n = 8
  ref = Ni_element
FEATURE [App::DocumentObjectGroupPython] G4_STAINLESS_STEEL  label="G4_STAINLESS-STEEL"  # scripted group (container) (typed FeaturePython)
  Dunit = g/cm3
  Dvalue = 8
  Group = -> [Fe_element008,Cr_element002,Ni_element002]
  conduct = 2
  density = 1
  expand = 3
  formula = G4_STAINLESS-STEEL
  name = G4_STAINLESS-STEEL
  specific = 4
FEATURE [App::DocumentObjectGroupPython] H_element116  label="H_element : 064"  # scripted group (container) (typed FeaturePython)
  n = 18
  ref = H_element
FEATURE [App::DocumentObjectGroupPython] C_element126  label="C_element : 071"  # scripted group (container) (typed FeaturePython)
  n = 12
  ref = C_element
FEATURE [App::DocumentObjectGroupPython] O_element109  label="O_element : 062"  # scripted group (container) (typed FeaturePython)
  n = 7
  ref = O_element
FEATURE [App::DocumentObjectGroupPython] G4_CR39  # scripted group (container) (typed FeaturePython)
  Dunit = g/cm3
  Dvalue = 1.32
  Group = -> [H_element116,C_element126,O_element109]
  conduct = 2
  density = 1
  expand = 3
  formula = G4_CR39
  name = G4_CR39
  specific = 4
FEATURE [App::DocumentObjectGroupPython] H_element117  label="H_element : 38"  # scripted group (container) (typed FeaturePython)
  n = 38
  ref = H_element
FEATURE [App::DocumentObjectGroupPython] C_element127  label="C_element : 072"  # scripted group (container) (typed FeaturePython)
  n = 18
  ref = C_element
FEATURE [App::DocumentObjectGroupPython] O_element110  label="O_element : 063"  # scripted group (container) (typed FeaturePython)
  n = 1
  ref = O_element
FEATURE [App::DocumentObjectGroupPython] G4_OCTADECANOL  # scripted group (container) (typed FeaturePython)
  Dunit = g/cm3
  Dvalue = 0.812
  Group = -> [H_element117,C_element127,O_element110]
  conduct = 2
  density = 1
  expand = 3
  formula = G4_OCTADECANOL
  name = G4_OCTADECANOL
  specific = 4
FEATURE [App::DocumentObjectGroupPython] HEP  # scripted group (container) (typed FeaturePython)
  Group = -> [G4_lH2,G4_lN2,G4_lO2,G4_lAr,G4_lBr,G4_lKr,G4_lXe,G4_PbWO4,G4_Galactic,G4_GRAPHITE_POROUS,G4_LUCITE,G4_BRASS,G4_BRONZE,G4_STAINLESS_STEEL,G4_CR39,G4_OCTADECANOL]
FEATURE [App::DocumentObjectGroupPython] C_element128  label="C_element : 073"  # scripted group (container) (typed FeaturePython)
  n = 14
  ref = C_element
FEATURE [App::DocumentObjectGroupPython] H_element118  label="H_element : 065"  # scripted group (container) (typed FeaturePython)
  n = 10
  ref = H_element
FEATURE [App::DocumentObjectGroupPython] O_element111  label="O_element : 064"  # scripted group (container) (typed FeaturePython)
  n = 2
  ref = O_element
FEATURE [App::DocumentObjectGroupPython] N_element050  label="N_element : 023"  # scripted group (container) (typed FeaturePython)
  n = 2
  ref = N_element
FEATURE [App::DocumentObjectGroupPython] G4_KEVLAR  # scripted group (container) (typed FeaturePython)
  Dunit = g/cm3
  Dvalue = 1.44
  Group = -> [C_element128,H_element118,O_element111,N_element050]
  conduct = 2
  density = 1
  expand = 3
  formula = G4_KEVLAR
  name = G4_KEVLAR
  specific = 4
FEATURE [App::DocumentObjectGroupPython] C_element129  label="C_element : 074"  # scripted group (container) (typed FeaturePython)
  n = 10
  ref = C_element
FEATURE [App::DocumentObjectGroupPython] H_element119  label="H_element : 066"  # scripted group (container) (typed FeaturePython)
  n = 8
  ref = H_element
FEATURE [App::DocumentObjectGroupPython] O_element112  label="O_element : 065"  # scripted group (container) (typed FeaturePython)
  n = 4
  ref = O_element
FEATURE [App::DocumentObjectGroupPython] G4_DACRON  # scripted group (container) (typed FeaturePython)
  Dunit = g/cm3
  Dvalue = 1.4
  Group = -> [C_element129,H_element119,O_element112]
  conduct = 2
  density = 1
  expand = 3
  formula = G4_DACRON
  name = G4_DACRON
  specific = 4
FEATURE [App::DocumentObjectGroupPython] C_element130  label="C_element : 075"  # scripted group (container) (typed FeaturePython)
  n = 4
  ref = C_element
FEATURE [App::DocumentObjectGroupPython] H_element120  label="H_element : 067"  # scripted group (container) (typed FeaturePython)
  n = 5
  ref = H_element
FEATURE [App::DocumentObjectGroupPython] Cl_element030  label="Cl_element : 016"  # scripted group (container) (typed FeaturePython)
  n = 1
  ref = Cl_element
FEATURE [App::DocumentObjectGroupPython] G4_NEOPRENE  # scripted group (container) (typed FeaturePython)
  Dunit = g/cm3
  Dvalue = 1.23
  Group = -> [C_element130,H_element120,Cl_element030]
  conduct = 2
  density = 1
  expand = 3
  formula = G4_NEOPRENE
  name = G4_NEOPRENE
  specific = 4
FEATURE [App::DocumentObjectGroupPython] Space  # scripted group (container) (typed FeaturePython)
  Group = -> [G4_KEVLAR,G4_DACRON,G4_NEOPRENE]
FEATURE [App::DocumentObjectGroupPython] H_element121  label="H_element : 068"  # scripted group (container) (typed FeaturePython)
  n = 5
  ref = H_element
FEATURE [App::DocumentObjectGroupPython] C_element131  label="C_element : 076"  # scripted group (container) (typed FeaturePython)
  n = 4
  ref = C_element
FEATURE [App::DocumentObjectGroupPython] N_element051  label="N_element : 3"  # scripted group (container) (typed FeaturePython)
  n = 3
  ref = N_element
FEATURE [App::DocumentObjectGroupPython] O_element113  label="O_element : 066"  # scripted group (container) (typed FeaturePython)
  n = 1
  ref = O_element
FEATURE [App::DocumentObjectGroupPython] G4_CYTOSINE  # scripted group (container) (typed FeaturePython)
  Dunit = g/cm3
  Dvalue = 1.55
  Group = -> [H_element121,C_element131,N_element051,O_element113]
  conduct = 2
  density = 1
  expand = 3
  formula = G4_CYTOSINE
  name = G4_CYTOSINE
  specific = 4
FEATURE [App::DocumentObjectGroupPython] H_element122  label="H_element : 069"  # scripted group (container) (typed FeaturePython)
  n = 6
  ref = H_element
FEATURE [App::DocumentObjectGroupPython] C_element132  label="C_element : 077"  # scripted group (container) (typed FeaturePython)
  n = 5
  ref = C_element
FEATURE [App::DocumentObjectGroupPython] N_element052  label="N_element : 024"  # scripted group (container) (typed FeaturePython)
  n = 2
  ref = N_element
FEATURE [App::DocumentObjectGroupPython] O_element114  label="O_element : 067"  # scripted group (container) (typed FeaturePython)
  n = 2
  ref = O_element
FEATURE [App::DocumentObjectGroupPython] G4_THYMINE  # scripted group (container) (typed FeaturePython)
  Dunit = g/cm3
  Dvalue = 1.23
  Group = -> [H_element122,C_element132,N_element052,O_element114]
  conduct = 2
  density = 1
  expand = 3
  formula = G4_THYMINE
  name = G4_THYMINE
  specific = 4
FEATURE [App::DocumentObjectGroupPython] H_element123  label="H_element : 070"  # scripted group (container) (typed FeaturePython)
  n = 4
  ref = H_element
FEATURE [App::DocumentObjectGroupPython] C_element133  label="C_element : 078"  # scripted group (container) (typed FeaturePython)
  n = 4
  ref = C_element
FEATURE [App::DocumentObjectGroupPython] N_element053  label="N_element : 025"  # scripted group (container) (typed FeaturePython)
  n = 2
  ref = N_element
FEATURE [App::DocumentObjectGroupPython] O_element115  label="O_element : 068"  # scripted group (container) (typed FeaturePython)
  n = 2
  ref = O_element
FEATURE [App::DocumentObjectGroupPython] G4_URACIL  # scripted group (container) (typed FeaturePython)
  Dunit = g/cm3
  Dvalue = 1.32
  Group = -> [H_element123,C_element133,N_element053,O_element115]
  conduct = 2
  density = 1
  expand = 3
  formula = G4_URACIL
  name = G4_URACIL
  specific = 4
FEATURE [App::DocumentObjectGroupPython] H_element124  label="H_element : 071"  # scripted group (container) (typed FeaturePython)
  n = 4
  ref = H_element
FEATURE [App::DocumentObjectGroupPython] C_element134  label="C_element : 079"  # scripted group (container) (typed FeaturePython)
  n = 5
  ref = C_element
FEATURE [App::DocumentObjectGroupPython] N_element054  label="N_element : 026"  # scripted group (container) (typed FeaturePython)
  n = 5
  ref = N_element
FEATURE [App::DocumentObjectGroupPython] G4_DNA_ADENINE  # scripted group (container) (typed FeaturePython)
  Dunit = g/cm3
  Dvalue = 1
  Group = -> [H_element124,C_element134,N_element054]
  conduct = 2
  density = 1
  expand = 3
  formula = G4_DNA_ADENINE
  name = G4_DNA_ADENINE
  specific = 4
FEATURE [App::DocumentObjectGroupPython] H_element125  label="H_element : 072"  # scripted group (container) (typed FeaturePython)
  n = 4
  ref = H_element
FEATURE [App::DocumentObjectGroupPython] C_element135  label="C_element : 080"  # scripted group (container) (typed FeaturePython)
  n = 5
  ref = C_element
FEATURE [App::DocumentObjectGroupPython] N_element055  label="N_element : 027"  # scripted group (container) (typed FeaturePython)
  n = 5
  ref = N_element
FEATURE [App::DocumentObjectGroupPython] O_element116  label="O_element : 069"  # scripted group (container) (typed FeaturePython)
  n = 1
  ref = O_element
FEATURE [App::DocumentObjectGroupPython] G4_DNA_GUANINE  # scripted group (container) (typed FeaturePython)
  Dunit = g/cm3
  Dvalue = 1
  Group = -> [H_element125,C_element135,N_element055,O_element116]
  conduct = 2
  density = 1
  expand = 3
  formula = G4_DNA_GUANINE
  name = G4_DNA_GUANINE
  specific = 4
FEATURE [App::DocumentObjectGroupPython] H_element126  label="H_element : 073"  # scripted group (container) (typed FeaturePython)
  n = 4
  ref = H_element
FEATURE [App::DocumentObjectGroupPython] C_element136  label="C_element : 081"  # scripted group (container) (typed FeaturePython)
  n = 4
  ref = C_element
FEATURE [App::DocumentObjectGroupPython] N_element056  label="N_element : 028"  # scripted group (container) (typed FeaturePython)
  n = 3
  ref = N_element
FEATURE [App::DocumentObjectGroupPython] O_element117  label="O_element : 070"  # scripted group (container) (typed FeaturePython)
  n = 1
  ref = O_element
FEATURE [App::DocumentObjectGroupPython] G4_DNA_CYTOSINE  # scripted group (container) (typed FeaturePython)
  Dunit = g/cm3
  Dvalue = 1
  Group = -> [H_element126,C_element136,N_element056,O_element117]
  conduct = 2
  density = 1
  expand = 3
  formula = G4_DNA_CYTOSINE
  name = G4_DNA_CYTOSINE
  specific = 4
FEATURE [App::DocumentObjectGroupPython] H_element127  label="H_element : 074"  # scripted group (container) (typed FeaturePython)
  n = 5
  ref = H_element
FEATURE [App::DocumentObjectGroupPython] C_element137  label="C_element : 082"  # scripted group (container) (typed FeaturePython)
  n = 5
  ref = C_element
FEATURE [App::DocumentObjectGroupPython] N_element057  label="N_element : 029"  # scripted group (container) (typed FeaturePython)
  n = 2
  ref = N_element
FEATURE [App::DocumentObjectGroupPython] O_element118  label="O_element : 071"  # scripted group (container) (typed FeaturePython)
  n = 2
  ref = O_element
FEATURE [App::DocumentObjectGroupPython] G4_DNA_THYMINE  # scripted group (container) (typed FeaturePython)
  Dunit = g/cm3
  Dvalue = 1
  Group = -> [H_element127,C_element137,N_element057,O_element118]
  conduct = 2
  density = 1
  expand = 3
  formula = G4_DNA_THYMINE
  name = G4_DNA_THYMINE
  specific = 4
FEATURE [App::DocumentObjectGroupPython] H_element128  label="H_element : 075"  # scripted group (container) (typed FeaturePython)
  n = 3
  ref = H_element
FEATURE [App::DocumentObjectGroupPython] C_element138  label="C_element : 083"  # scripted group (container) (typed FeaturePython)
  n = 4
  ref = C_element
FEATURE [App::DocumentObjectGroupPython] N_element058  label="N_element : 030"  # scripted group (container) (typed FeaturePython)
  n = 2
  ref = N_element
FEATURE [App::DocumentObjectGroupPython] O_element119  label="O_element : 072"  # scripted group (container) (typed FeaturePython)
  n = 2
  ref = O_element
FEATURE [App::DocumentObjectGroupPython] G4_DNA_URACIL  # scripted group (container) (typed FeaturePython)
  Dunit = g/cm3
  Dvalue = 1
  Group = -> [H_element128,C_element138,N_element058,O_element119]
  conduct = 2
  density = 1
  expand = 3
  formula = G4_DNA_URACIL
  name = G4_DNA_URACIL
  specific = 4
FEATURE [App::DocumentObjectGroupPython] H_element129  label="H_element : 076"  # scripted group (container) (typed FeaturePython)
  n = 10
  ref = H_element
FEATURE [App::DocumentObjectGroupPython] C_element139  label="C_element : 084"  # scripted group (container) (typed FeaturePython)
  n = 10
  ref = C_element
FEATURE [App::DocumentObjectGroupPython] N_element059  label="N_element : 031"  # scripted group (container) (typed FeaturePython)
  n = 5
  ref = N_element
FEATURE [App::DocumentObjectGroupPython] O_element120  label="O_element : 073"  # scripted group (container) (typed FeaturePython)
  n = 4
  ref = O_element
FEATURE [App::DocumentObjectGroupPython] G4_DNA_ADENOSINE  # scripted group (container) (typed FeaturePython)
  Dunit = g/cm3
  Dvalue = 1
  Group = -> [H_element129,C_element139,N_element059,O_element120]
  conduct = 2
  density = 1
  expand = 3
  formula = G4_DNA_ADENOSINE
  name = G4_DNA_ADENOSINE
  specific = 4
FEATURE [App::DocumentObjectGroupPython] H_element130  label="H_element : 077"  # scripted group (container) (typed FeaturePython)
  n = 10
  ref = H_element
FEATURE [App::DocumentObjectGroupPython] C_element140  label="C_element : 085"  # scripted group (container) (typed FeaturePython)
  n = 10
  ref = C_element
FEATURE [App::DocumentObjectGroupPython] N_element060  label="N_element : 032"  # scripted group (container) (typed FeaturePython)
  n = 5
  ref = N_element
FEATURE [App::DocumentObjectGroupPython] O_element121  label="O_element : 074"  # scripted group (container) (typed FeaturePython)
  n = 5
  ref = O_element
FEATURE [App::DocumentObjectGroupPython] G4_DNA_GUANOSINE  # scripted group (container) (typed FeaturePython)
  Dunit = g/cm3
  Dvalue = 1
  Group = -> [H_element130,C_element140,N_element060,O_element121]
  conduct = 2
  density = 1
  expand = 3
  formula = G4_DNA_GUANOSINE
  name = G4_DNA_GUANOSINE
  specific = 4
FEATURE [App::DocumentObjectGroupPython] H_element131  label="H_element : 078"  # scripted group (container) (typed FeaturePython)
  n = 10
  ref = H_element
FEATURE [App::DocumentObjectGroupPython] C_element141  label="C_element : 086"  # scripted group (container) (typed FeaturePython)
  n = 9
  ref = C_element
FEATURE [App::DocumentObjectGroupPython] N_element061  label="N_element : 033"  # scripted group (container) (typed FeaturePython)
  n = 3
  ref = N_element
FEATURE [App::DocumentObjectGroupPython] O_element122  label="O_element : 075"  # scripted group (container) (typed FeaturePython)
  n = 5
  ref = O_element
FEATURE [App::DocumentObjectGroupPython] G4_DNA_CYTIDINE  # scripted group (container) (typed FeaturePython)
  Dunit = g/cm3
  Dvalue = 1
  Group = -> [H_element131,C_element141,N_element061,O_element122]
  conduct = 2
  density = 1
  expand = 3
  formula = G4_DNA_CYTIDINE
  name = G4_DNA_CYTIDINE
  specific = 4
FEATURE [App::DocumentObjectGroupPython] H_element132  label="H_element : 079"  # scripted group (container) (typed FeaturePython)
  n = 9
  ref = H_element
FEATURE [App::DocumentObjectGroupPython] C_element142  label="C_element : 087"  # scripted group (container) (typed FeaturePython)
  n = 9
  ref = C_element
FEATURE [App::DocumentObjectGroupPython] N_element062  label="N_element : 034"  # scripted group (container) (typed FeaturePython)
  n = 2
  ref = N_element
FEATURE [App::DocumentObjectGroupPython] O_element123  label="O_element : 076"  # scripted group (container) (typed FeaturePython)
  n = 6
  ref = O_element
FEATURE [App::DocumentObjectGroupPython] G4_DNA_URIDINE  # scripted group (container) (typed FeaturePython)
  Dunit = g/cm3
  Dvalue = 1
  Group = -> [H_element132,C_element142,N_element062,O_element123]
  conduct = 2
  density = 1
  expand = 3
  formula = G4_DNA_URIDINE
  name = G4_DNA_URIDINE
  specific = 4
FEATURE [App::DocumentObjectGroupPython] H_element133  label="H_element : 080"  # scripted group (container) (typed FeaturePython)
  n = 11
  ref = H_element
FEATURE [App::DocumentObjectGroupPython] C_element143  label="C_element : 088"  # scripted group (container) (typed FeaturePython)
  n = 10
  ref = C_element
FEATURE [App::DocumentObjectGroupPython] N_element063  label="N_element : 035"  # scripted group (container) (typed FeaturePython)
  n = 2
  ref = N_element
FEATURE [App::DocumentObjectGroupPython] O_element124  label="O_element : 077"  # scripted group (container) (typed FeaturePython)
  n = 6
  ref = O_element
FEATURE [App::DocumentObjectGroupPython] G4_DNA_METHYLURIDINE  # scripted group (container) (typed FeaturePython)
  Dunit = g/cm3
  Dvalue = 1
  Group = -> [H_element133,C_element143,N_element063,O_element124]
  conduct = 2
  density = 1
  expand = 3
  formula = G4_DNA_METHYLURIDINE
  name = G4_DNA_METHYLURIDINE
  specific = 4
FEATURE [App::DocumentObjectGroupPython] P_element014  label="P_element : 003"  # scripted group (container) (typed FeaturePython)
  n = 1
  ref = P_element
FEATURE [App::DocumentObjectGroupPython] O_element125  label="O_element : 078"  # scripted group (container) (typed FeaturePython)
  n = 3
  ref = O_element
FEATURE [App::DocumentObjectGroupPython] G4_DNA_MONOPHOSPHATE  # scripted group (container) (typed FeaturePython)
  Dunit = g/cm3
  Dvalue = 1
  Group = -> [P_element014,O_element125]
  conduct = 2
  density = 1
  expand = 3
  formula = G4_DNA_MONOPHOSPHATE
  name = G4_DNA_MONOPHOSPHATE
  specific = 4
FEATURE [App::DocumentObjectGroupPython] H_element134  label="H_element : 081"  # scripted group (container) (typed FeaturePython)
  n = 10
  ref = H_element
FEATURE [App::DocumentObjectGroupPython] C_element144  label="C_element : 089"  # scripted group (container) (typed FeaturePython)
  n = 10
  ref = C_element
FEATURE [App::DocumentObjectGroupPython] N_element064  label="N_element : 036"  # scripted group (container) (typed FeaturePython)
  n = 5
  ref = N_element
FEATURE [App::DocumentObjectGroupPython] O_element126  label="O_element : 079"  # scripted group (container) (typed FeaturePython)
  n = 7
  ref = O_element
FEATURE [App::DocumentObjectGroupPython] P_element015  label="P_element : 004"  # scripted group (container) (typed FeaturePython)
  n = 1
  ref = P_element
FEATURE [App::DocumentObjectGroupPython] G4_DNA_A  # scripted group (container) (typed FeaturePython)
  Dunit = g/cm3
  Dvalue = 1
  Group = -> [H_element134,C_element144,N_element064,O_element126,P_element015]
  conduct = 2
  density = 1
  expand = 3
  formula = G4_DNA_A
  name = G4_DNA_A
  specific = 4
FEATURE [App::DocumentObjectGroupPython] H_element135  label="H_element : 082"  # scripted group (container) (typed FeaturePython)
  n = 10
  ref = H_element
FEATURE [App::DocumentObjectGroupPython] C_element145  label="C_element : 090"  # scripted group (container) (typed FeaturePython)
  n = 10
  ref = C_element
FEATURE [App::DocumentObjectGroupPython] N_element065  label="N_element : 037"  # scripted group (container) (typed FeaturePython)
  n = 5
  ref = N_element
FEATURE [App::DocumentObjectGroupPython] O_element127  label="O_element : 8"  # scripted group (container) (typed FeaturePython)
  n = 8
  ref = O_element
FEATURE [App::DocumentObjectGroupPython] P_element016  label="P_element : 005"  # scripted group (container) (typed FeaturePython)
  n = 1
  ref = P_element
FEATURE [App::DocumentObjectGroupPython] G4_DNA_G  # scripted group (container) (typed FeaturePython)
  Dunit = g/cm3
  Dvalue = 1
  Group = -> [H_element135,C_element145,N_element065,O_element127,P_element016]
  conduct = 2
  density = 1
  expand = 3
  formula = G4_DNA_G
  name = G4_DNA_G
  specific = 4
FEATURE [App::DocumentObjectGroupPython] H_element136  label="H_element : 083"  # scripted group (container) (typed FeaturePython)
  n = 10
  ref = H_element
FEATURE [App::DocumentObjectGroupPython] C_element146  label="C_element : 091"  # scripted group (container) (typed FeaturePython)
  n = 9
  ref = C_element
FEATURE [App::DocumentObjectGroupPython] N_element066  label="N_element : 038"  # scripted group (container) (typed FeaturePython)
  n = 3
  ref = N_element
FEATURE [App::DocumentObjectGroupPython] O_element128  label="O_element : 080"  # scripted group (container) (typed FeaturePython)
  n = 8
  ref = O_element
FEATURE [App::DocumentObjectGroupPython] P_element017  label="P_element : 006"  # scripted group (container) (typed FeaturePython)
  n = 1
  ref = P_element
FEATURE [App::DocumentObjectGroupPython] G4_DNA_C  # scripted group (container) (typed FeaturePython)
  Dunit = g/cm3
  Dvalue = 1
  Group = -> [H_element136,C_element146,N_element066,O_element128,P_element017]
  conduct = 2
  density = 1
  expand = 3
  formula = G4_DNA_C
  name = G4_DNA_C
  specific = 4
FEATURE [App::DocumentObjectGroupPython] H_element137  label="H_element : 084"  # scripted group (container) (typed FeaturePython)
  n = 9
  ref = H_element
FEATURE [App::DocumentObjectGroupPython] C_element147  label="C_element : 092"  # scripted group (container) (typed FeaturePython)
  n = 9
  ref = C_element
FEATURE [App::DocumentObjectGroupPython] N_element067  label="N_element : 039"  # scripted group (container) (typed FeaturePython)
  n = 2
  ref = N_element
FEATURE [App::DocumentObjectGroupPython] O_element129  label="O_element : 9"  # scripted group (container) (typed FeaturePython)
  n = 9
  ref = O_element
FEATURE [App::DocumentObjectGroupPython] P_element018  label="P_element : 007"  # scripted group (container) (typed FeaturePython)
  n = 1
  ref = P_element
FEATURE [App::DocumentObjectGroupPython] G4_DNA_U  # scripted group (container) (typed FeaturePython)
  Dunit = g/cm3
  Dvalue = 1
  Group = -> [H_element137,C_element147,N_element067,O_element129,P_element018]
  conduct = 2
  density = 1
  expand = 3
  formula = G4_DNA_U
  name = G4_DNA_U
  specific = 4
FEATURE [App::DocumentObjectGroupPython] H_element138  label="H_element : 085"  # scripted group (container) (typed FeaturePython)
  n = 11
  ref = H_element
FEATURE [App::DocumentObjectGroupPython] C_element148  label="C_element : 093"  # scripted group (container) (typed FeaturePython)
  n = 10
  ref = C_element
FEATURE [App::DocumentObjectGroupPython] N_element068  label="N_element : 040"  # scripted group (container) (typed FeaturePython)
  n = 2
  ref = N_element
FEATURE [App::DocumentObjectGroupPython] O_element130  label="O_element : 081"  # scripted group (container) (typed FeaturePython)
  n = 9
  ref = O_element
FEATURE [App::DocumentObjectGroupPython] P_element019  label="P_element : 008"  # scripted group (container) (typed FeaturePython)
  n = 1
  ref = P_element
FEATURE [App::DocumentObjectGroupPython] G4_DNA_MU  # scripted group (container) (typed FeaturePython)
  Dunit = g/cm3
  Dvalue = 1
  Group = -> [H_element138,C_element148,N_element068,O_element130,P_element019]
  conduct = 2
  density = 1
  expand = 3
  formula = G4_DNA_MU
  name = G4_DNA_MU
  specific = 4
FEATURE [App::DocumentObjectGroupPython] BioChemical  # scripted group (container) (typed FeaturePython)
  Group = -> [G4_CYTOSINE,G4_THYMINE,G4_URACIL,G4_DNA_ADENINE,G4_DNA_GUANINE,G4_DNA_CYTOSINE,G4_DNA_THYMINE,G4_DNA_URACIL,G4_DNA_ADENOSINE,G4_DNA_GUANOSINE,G4_DNA_CYTIDINE,G4_DNA_URIDINE,G4_DNA_METHYLURIDINE,G4_DNA_MONOPHOSPHATE,G4_DNA_A,G4_DNA_G,G4_DNA_C,G4_DNA_U,G4_DNA_MU]
FEATURE [App::DocumentObjectGroupPython] G4Materials  # scripted group (container) (typed FeaturePython)
  Group = -> [NIST,Element,HEP,Space,BioChemical]
  version = 1
FEATURE [App::DocumentObjectGroupPython] Geant4  # scripted group (container) (typed FeaturePython)
  Group = -> [G4Isotopes,G4Elements,G4Materials]
FEATURE [App::DocumentObjectGroupPython] Materials  # scripted group (container) (typed FeaturePython)
  Group = -> [Geant4]
FEATURE [Part::FeaturePython] GDMLBox_WorldBox  # WARN: FeaturePython — macro-defined, semantics opaque (R4)
  lunit = 2
  material = 5
  x = 100
  y = 100
  z = 100
FEATURE [Sketcher::SketchObject] Sketch
  FullyConstrained = false
  sketch-geometry (15):
    g0-g5: Circle x6 (B-spline internal-alignment scaffolding for g6; pole/knot coordinates omitted)
    g6: BSplineCurve PolesCount=7 KnotsCount=5 Degree=3 IsPeriodic=0
    g7-g10: GeomPoint x4 (B-spline internal-alignment scaffolding for g6; pole/knot coordinates omitted)
    g11: LineSegment StartX=-4.39557 StartY=8.39124 StartZ=0 EndX=-5.2662 EndY=10.5884 EndZ=0
    g12: LineSegment StartX=-5.2662 StartY=10.5884 StartZ=0 EndX=-7.82152 EndY=9.89481 EndZ=0
    g13: LineSegment StartX=-7.82152 StartY=9.89481 StartZ=0 EndX=-9.50073 EndY=7.63152 EndZ=0
    g14: ArcOfCircle CenterX=-7.8377 CenterY=5.34547 CenterZ=0 NormalX=0 NormalY=0 NormalZ=1 AngleXU=0 Radius=2.82696 StartAngle=4.84147 EndAngle=8.48291
  constraints (9):
    c: Weight(g0) = 1
    c: Equal(g0, g1-g5) x5
    c: InternalAlignment(g0-g5 -> g6) x6
    c: InternalAlignment(g7-g10 -> g6) x4
    c: Coincident(g11,g6)
    c: Coincident(g11,g12)
    c: Coincident(g12,g13)
    c: Coincident(g14,g13)
    c: Coincident(g14,g6)
FEATURE [Part::Extrusion] Extrude
  Base = -> Sketch
  Dir = (0,0,1)
  DirMode = 2
  FaceMakerClass = Part::FaceMakerBullseye
  LengthFwd = 10
  LengthRev = 0
  Placement = pos=(13,12,0) rot=(0,0,1;0rad)
  Solid = true
  Symmetric = false
  material = 1
FEATURE [Part::Mirroring] Part__Mirroring  label="mirror1"
  Base = (0,0,0)
  Normal = (1,0,0)
  Placement = pos=(0,21,0) rot=(0,0,1;0rad)
  Source = -> Extrude
  material = 261
FEATURE [Part::Mirroring] Part__Mirroring002  label="mirror2"
  Base = (0,0,0)
  Normal = (0,1,0)
  Placement = pos=(0,0,0) rot=(0,0,1;0.523599rad)
  Source = -> Part__Mirroring
FEATURE [App::Part] Part
  Group = -> [Sketch,Extrude,Part__Mirroring,Part__Mirroring002]
  Origin = -> Origin001
FEATURE [App::Part] worldVOL
  Group = -> [GDMLBox_WorldBox,Part]
  Origin = -> Origin
